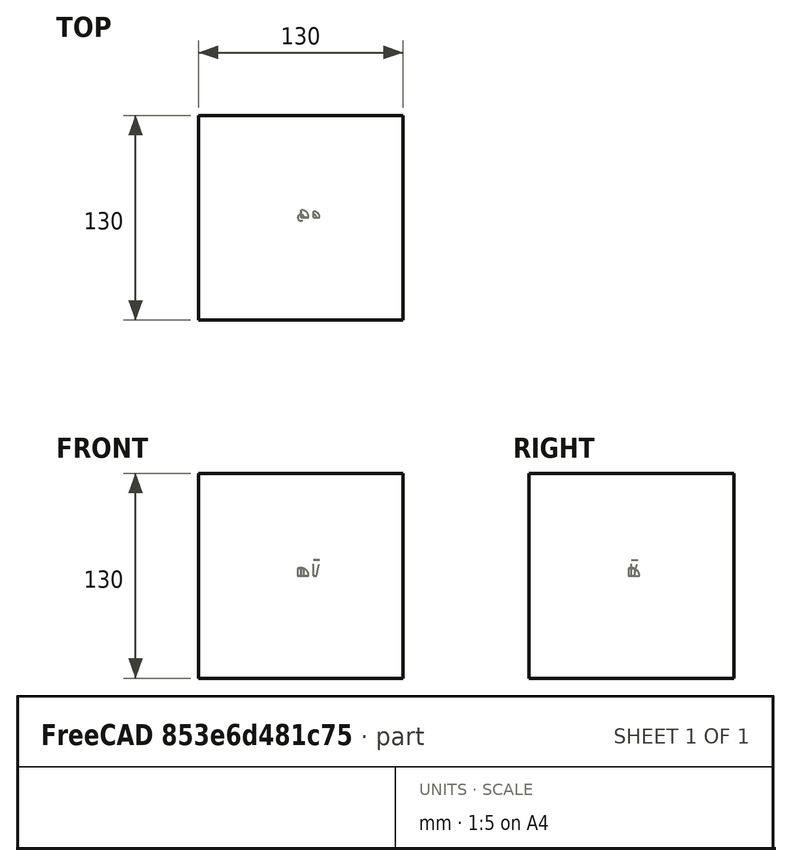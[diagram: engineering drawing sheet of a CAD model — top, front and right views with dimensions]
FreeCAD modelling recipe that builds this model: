
FCSTD DOCUMENT  (FreeCAD 1.0R39109 (Git))
Label: MultiCommon
License: All rights reserved
objects: App::DocumentObjectGroupPython×1252, App::Part×3, Spreadsheet::Sheet×2, Part::Box×2, Part::FeaturePython×1, Part::Cylinder×1, Part::Sphere×1, Part::Cone×1, Part::Common×1, Part::MultiCommon×1
note: 8 computed .brp shape members not serialized (recipe doc carries the construction recipe); baked Part::Feature solids carry a one-line shape summary decoded from their .brp

FEATURE [Spreadsheet::Sheet] defines
  cells = A1='constant; B1='HALFPI; C1(HALFPI)==pi / 2; A2='constant; B2='PI; C2(PI)==1 * pi; A3='constant; B3='TWOPI; C3(TWOPI)==2 * pi
FEATURE [Spreadsheet::Sheet] gdmlInfo
FEATURE [App::DocumentObjectGroupPython] Define  # scripted group (container) (typed FeaturePython)
  Group = -> [defines,gdmlInfo]
FEATURE [App::DocumentObjectGroupPython] HALFPI  # scripted group (container) (typed FeaturePython)
  name = HALFPI
  value = pi/2.
FEATURE [App::DocumentObjectGroupPython] PI  # scripted group (container) (typed FeaturePython)
  name = PI
  value = 1.*pi
FEATURE [App::DocumentObjectGroupPython] TWOPI  # scripted group (container) (typed FeaturePython)
  name = TWOPI
  value = 2.*pi
FEATURE [App::DocumentObjectGroupPython] Constants  # scripted group (container) (typed FeaturePython)
  Group = -> [HALFPI,PI,TWOPI]
FEATURE [App::DocumentObjectGroupPython] Quantities  # scripted group (container) (typed FeaturePython)
FEATURE [App::DocumentObjectGroupPython] Variables  # scripted group (container) (typed FeaturePython)
FEATURE [App::DocumentObjectGroupPython] Isotopes  # scripted group (container) (typed FeaturePython)
FEATURE [App::DocumentObjectGroupPython] Elements  # scripted group (container) (typed FeaturePython)
FEATURE [App::DocumentObjectGroupPython] Matrix  # scripted group (container) (typed FeaturePython)
FEATURE [App::DocumentObjectGroupPython] Surfaces  # scripted group (container) (typed FeaturePython)
FEATURE [App::DocumentObjectGroupPython] Opticals  # scripted group (container) (typed FeaturePython)
  Group = -> [Matrix,Surfaces]
FEATURE [App::DocumentObjectGroupPython] G4Isotopes  # scripted group (container) (typed FeaturePython)
FEATURE [App::DocumentObjectGroupPython] H_element  # scripted group (container) (typed FeaturePython)
  Z = 1
  atom_value = 1.008
  formula = H
  name = H_element
FEATURE [App::DocumentObjectGroupPython] He_element  # scripted group (container) (typed FeaturePython)
  Z = 2
  atom_value = 4.0026
  formula = He
  name = He_element
FEATURE [App::DocumentObjectGroupPython] Li_element  # scripted group (container) (typed FeaturePython)
  Z = 3
  atom_value = 6.94
  formula = Li
  name = Li_element
FEATURE [App::DocumentObjectGroupPython] Be_element  # scripted group (container) (typed FeaturePython)
  Z = 4
  atom_value = 9.01218
  formula = Be
  name = Be_element
FEATURE [App::DocumentObjectGroupPython] B_element  # scripted group (container) (typed FeaturePython)
  Z = 5
  atom_value = 10.81
  formula = B
  name = B_element
FEATURE [App::DocumentObjectGroupPython] C_element  # scripted group (container) (typed FeaturePython)
  Z = 6
  atom_value = 12.011
  formula = C
  name = C_element
FEATURE [App::DocumentObjectGroupPython] N_element  # scripted group (container) (typed FeaturePython)
  Z = 7
  atom_value = 14.007
  formula = N
  name = N_element
FEATURE [App::DocumentObjectGroupPython] O_element  # scripted group (container) (typed FeaturePython)
  Z = 8
  atom_value = 15.999
  formula = O
  name = O_element
FEATURE [App::DocumentObjectGroupPython] F_element  # scripted group (container) (typed FeaturePython)
  Z = 9
  atom_value = 18.9984
  formula = F
  name = F_element
FEATURE [App::DocumentObjectGroupPython] Ne_element  # scripted group (container) (typed FeaturePython)
  Z = 10
  atom_value = 20.1797
  formula = Ne
  name = Ne_element
FEATURE [App::DocumentObjectGroupPython] Na_element  # scripted group (container) (typed FeaturePython)
  Z = 11
  atom_value = 22.9898
  formula = Na
  name = Na_element
FEATURE [App::DocumentObjectGroupPython] Mg_element  # scripted group (container) (typed FeaturePython)
  Z = 12
  atom_value = 24.305
  formula = Mg
  name = Mg_element
FEATURE [App::DocumentObjectGroupPython] Al_element  # scripted group (container) (typed FeaturePython)
  Z = 13
  atom_value = 26.9815
  formula = Al
  name = Al_element
FEATURE [App::DocumentObjectGroupPython] Si_element  # scripted group (container) (typed FeaturePython)
  Z = 14
  atom_value = 28.085
  formula = Si
  name = Si_element
FEATURE [App::DocumentObjectGroupPython] P_element  # scripted group (container) (typed FeaturePython)
  Z = 15
  atom_value = 30.9738
  formula = P
  name = P_element
FEATURE [App::DocumentObjectGroupPython] S_element  # scripted group (container) (typed FeaturePython)
  Z = 16
  atom_value = 32.06
  formula = S
  name = S_element
FEATURE [App::DocumentObjectGroupPython] Cl_element  # scripted group (container) (typed FeaturePython)
  Z = 17
  atom_value = 35.45
  formula = Cl
  name = Cl_element
FEATURE [App::DocumentObjectGroupPython] Ar_element  # scripted group (container) (typed FeaturePython)
  Z = 18
  atom_value = 39.95
  formula = Ar
  name = Ar_element
FEATURE [App::DocumentObjectGroupPython] K_element  # scripted group (container) (typed FeaturePython)
  Z = 19
  atom_value = 39.0983
  formula = K
  name = K_element
FEATURE [App::DocumentObjectGroupPython] Ca_element  # scripted group (container) (typed FeaturePython)
  Z = 20
  atom_value = 40.078
  formula = Ca
  name = Ca_element
FEATURE [App::DocumentObjectGroupPython] Sc_element  # scripted group (container) (typed FeaturePython)
  Z = 21
  atom_value = 44.9559
  formula = Sc
  name = Sc_element
FEATURE [App::DocumentObjectGroupPython] Ti_element  # scripted group (container) (typed FeaturePython)
  Z = 22
  atom_value = 47.867
  formula = Ti
  name = Ti_element
FEATURE [App::DocumentObjectGroupPython] V_element  # scripted group (container) (typed FeaturePython)
  Z = 23
  atom_value = 50.9415
  formula = V
  name = V_element
FEATURE [App::DocumentObjectGroupPython] Cr_element  # scripted group (container) (typed FeaturePython)
  Z = 24
  atom_value = 51.9961
  formula = Cr
  name = Cr_element
FEATURE [App::DocumentObjectGroupPython] Mn_element  # scripted group (container) (typed FeaturePython)
  Z = 25
  atom_value = 54.938
  formula = Mn
  name = Mn_element
FEATURE [App::DocumentObjectGroupPython] Fe_element  # scripted group (container) (typed FeaturePython)
  Z = 26
  atom_value = 55.845
  formula = Fe
  name = Fe_element
FEATURE [App::DocumentObjectGroupPython] Co_element  # scripted group (container) (typed FeaturePython)
  Z = 27
  atom_value = 58.9332
  formula = Co
  name = Co_element
FEATURE [App::DocumentObjectGroupPython] Ni_element  # scripted group (container) (typed FeaturePython)
  Z = 28
  atom_value = 58.6934
  formula = Ni
  name = Ni_element
FEATURE [App::DocumentObjectGroupPython] Cu_element  # scripted group (container) (typed FeaturePython)
  Z = 29
  atom_value = 63.546
  formula = Cu
  name = Cu_element
FEATURE [App::DocumentObjectGroupPython] Zn_element  # scripted group (container) (typed FeaturePython)
  Z = 30
  atom_value = 65.38
  formula = Zn
  name = Zn_element
FEATURE [App::DocumentObjectGroupPython] Ga_element  # scripted group (container) (typed FeaturePython)
  Z = 31
  atom_value = 69.723
  formula = Ga
  name = Ga_element
FEATURE [App::DocumentObjectGroupPython] Ge_element  # scripted group (container) (typed FeaturePython)
  Z = 32
  atom_value = 72.63
  formula = Ge
  name = Ge_element
FEATURE [App::DocumentObjectGroupPython] As_element  # scripted group (container) (typed FeaturePython)
  Z = 33
  atom_value = 74.9216
  formula = As
  name = As_element
FEATURE [App::DocumentObjectGroupPython] Se_element  # scripted group (container) (typed FeaturePython)
  Z = 34
  atom_value = 78.971
  formula = Se
  name = Se_element
FEATURE [App::DocumentObjectGroupPython] Br_element  # scripted group (container) (typed FeaturePython)
  Z = 35
  atom_value = 79.904
  formula = Br
  name = Br_element
FEATURE [App::DocumentObjectGroupPython] Kr_element  # scripted group (container) (typed FeaturePython)
  Z = 36
  atom_value = 83.798
  formula = Kr
  name = Kr_element
FEATURE [App::DocumentObjectGroupPython] Rb_element  # scripted group (container) (typed FeaturePython)
  Z = 37
  atom_value = 85.4678
  formula = Rb
  name = Rb_element
FEATURE [App::DocumentObjectGroupPython] Sr_element  # scripted group (container) (typed FeaturePython)
  Z = 38
  atom_value = 87.62
  formula = Sr
  name = Sr_element
FEATURE [App::DocumentObjectGroupPython] Y_element  # scripted group (container) (typed FeaturePython)
  Z = 39
  atom_value = 88.9058
  formula = Y
  name = Y_element
FEATURE [App::DocumentObjectGroupPython] Zr_element  # scripted group (container) (typed FeaturePython)
  Z = 40
  atom_value = 91.224
  formula = Zr
  name = Zr_element
FEATURE [App::DocumentObjectGroupPython] Nb_element  # scripted group (container) (typed FeaturePython)
  Z = 41
  atom_value = 92.9064
  formula = Nb
  name = Nb_element
FEATURE [App::DocumentObjectGroupPython] Mo_element  # scripted group (container) (typed FeaturePython)
  Z = 42
  atom_value = 95.95
  formula = Mo
  name = Mo_element
FEATURE [App::DocumentObjectGroupPython] Tc_element  # scripted group (container) (typed FeaturePython)
  Z = 43
  atom_value = 97
  formula = Tc
  name = Tc_element
FEATURE [App::DocumentObjectGroupPython] Ru_element  # scripted group (container) (typed FeaturePython)
  Z = 44
  atom_value = 101.07
  formula = Ru
  name = Ru_element
FEATURE [App::DocumentObjectGroupPython] Rh_element  # scripted group (container) (typed FeaturePython)
  Z = 45
  atom_value = 102.905
  formula = Rh
  name = Rh_element
FEATURE [App::DocumentObjectGroupPython] Pd_element  # scripted group (container) (typed FeaturePython)
  Z = 46
  atom_value = 106.42
  formula = Pd
  name = Pd_element
FEATURE [App::DocumentObjectGroupPython] Ag_element  # scripted group (container) (typed FeaturePython)
  Z = 47
  atom_value = 107.868
  formula = Ag
  name = Ag_element
FEATURE [App::DocumentObjectGroupPython] Cd_element  # scripted group (container) (typed FeaturePython)
  Z = 48
  atom_value = 112.414
  formula = Cd
  name = Cd_element
FEATURE [App::DocumentObjectGroupPython] In_element  # scripted group (container) (typed FeaturePython)
  Z = 49
  atom_value = 114.818
  formula = In
  name = In_element
FEATURE [App::DocumentObjectGroupPython] Sn_element  # scripted group (container) (typed FeaturePython)
  Z = 50
  atom_value = 118.71
  formula = Sn
  name = Sn_element
FEATURE [App::DocumentObjectGroupPython] Sb_element  # scripted group (container) (typed FeaturePython)
  Z = 51
  atom_value = 121.76
  formula = Sb
  name = Sb_element
FEATURE [App::DocumentObjectGroupPython] Te_element  # scripted group (container) (typed FeaturePython)
  Z = 52
  atom_value = 127.6
  formula = Te
  name = Te_element
FEATURE [App::DocumentObjectGroupPython] I_element  # scripted group (container) (typed FeaturePython)
  Z = 53
  atom_value = 126.904
  formula = I
  name = I_element
FEATURE [App::DocumentObjectGroupPython] Xe_element  # scripted group (container) (typed FeaturePython)
  Z = 54
  atom_value = 131.293
  formula = Xe
  name = Xe_element
FEATURE [App::DocumentObjectGroupPython] Cs_element  # scripted group (container) (typed FeaturePython)
  Z = 55
  atom_value = 132.905
  formula = Cs
  name = Cs_element
FEATURE [App::DocumentObjectGroupPython] Ba_element  # scripted group (container) (typed FeaturePython)
  Z = 56
  atom_value = 137.327
  formula = Ba
  name = Ba_element
FEATURE [App::DocumentObjectGroupPython] La_element  # scripted group (container) (typed FeaturePython)
  Z = 57
  atom_value = 138.905
  formula = La
  name = La_element
FEATURE [App::DocumentObjectGroupPython] Ce_element  # scripted group (container) (typed FeaturePython)
  Z = 58
  atom_value = 140.116
  formula = Ce
  name = Ce_element
FEATURE [App::DocumentObjectGroupPython] Pr_element  # scripted group (container) (typed FeaturePython)
  Z = 59
  atom_value = 140.908
  formula = Pr
  name = Pr_element
FEATURE [App::DocumentObjectGroupPython] Nd_element  # scripted group (container) (typed FeaturePython)
  Z = 60
  atom_value = 144.242
  formula = Nd
  name = Nd_element
FEATURE [App::DocumentObjectGroupPython] Pm_element  # scripted group (container) (typed FeaturePython)
  Z = 61
  atom_value = 145
  formula = Pm
  name = Pm_element
FEATURE [App::DocumentObjectGroupPython] Sm_element  # scripted group (container) (typed FeaturePython)
  Z = 62
  atom_value = 150.36
  formula = Sm
  name = Sm_element
FEATURE [App::DocumentObjectGroupPython] Eu_element  # scripted group (container) (typed FeaturePython)
  Z = 63
  atom_value = 151.964
  formula = Eu
  name = Eu_element
FEATURE [App::DocumentObjectGroupPython] Gd_element  # scripted group (container) (typed FeaturePython)
  Z = 64
  atom_value = 157.25
  formula = Gd
  name = Gd_element
FEATURE [App::DocumentObjectGroupPython] Tb_element  # scripted group (container) (typed FeaturePython)
  Z = 65
  atom_value = 158.925
  formula = Tb
  name = Tb_element
FEATURE [App::DocumentObjectGroupPython] Dy_element  # scripted group (container) (typed FeaturePython)
  Z = 66
  atom_value = 162.5
  formula = Dy
  name = Dy_element
FEATURE [App::DocumentObjectGroupPython] Ho_element  # scripted group (container) (typed FeaturePython)
  Z = 67
  atom_value = 164.93
  formula = Ho
  name = Ho_element
FEATURE [App::DocumentObjectGroupPython] Er_element  # scripted group (container) (typed FeaturePython)
  Z = 68
  atom_value = 167.259
  formula = Er
  name = Er_element
FEATURE [App::DocumentObjectGroupPython] Tm_element  # scripted group (container) (typed FeaturePython)
  Z = 69
  atom_value = 168.934
  formula = Tm
  name = Tm_element
FEATURE [App::DocumentObjectGroupPython] Yb_element  # scripted group (container) (typed FeaturePython)
  Z = 70
  atom_value = 173.045
  formula = Yb
  name = Yb_element
FEATURE [App::DocumentObjectGroupPython] Lu_element  # scripted group (container) (typed FeaturePython)
  Z = 71
  atom_value = 174.967
  formula = Lu
  name = Lu_element
FEATURE [App::DocumentObjectGroupPython] Hf_element  # scripted group (container) (typed FeaturePython)
  Z = 72
  atom_value = 178.49
  formula = Hf
  name = Hf_element
FEATURE [App::DocumentObjectGroupPython] Ta_element  # scripted group (container) (typed FeaturePython)
  Z = 73
  atom_value = 180.948
  formula = Ta
  name = Ta_element
FEATURE [App::DocumentObjectGroupPython] W_element  # scripted group (container) (typed FeaturePython)
  Z = 74
  atom_value = 183.84
  formula = W
  name = W_element
FEATURE [App::DocumentObjectGroupPython] Re_element  # scripted group (container) (typed FeaturePython)
  Z = 75
  atom_value = 186.207
  formula = Re
  name = Re_element
FEATURE [App::DocumentObjectGroupPython] Os_element  # scripted group (container) (typed FeaturePython)
  Z = 76
  atom_value = 190.23
  formula = Os
  name = Os_element
FEATURE [App::DocumentObjectGroupPython] Ir_element  # scripted group (container) (typed FeaturePython)
  Z = 77
  atom_value = 192.217
  formula = Ir
  name = Ir_element
FEATURE [App::DocumentObjectGroupPython] Pt_element  # scripted group (container) (typed FeaturePython)
  Z = 78
  atom_value = 195.084
  formula = Pt
  name = Pt_element
FEATURE [App::DocumentObjectGroupPython] Au_element  # scripted group (container) (typed FeaturePython)
  Z = 79
  atom_value = 196.967
  formula = Au
  name = Au_element
FEATURE [App::DocumentObjectGroupPython] Hg_element  # scripted group (container) (typed FeaturePython)
  Z = 80
  atom_value = 200.592
  formula = Hg
  name = Hg_element
FEATURE [App::DocumentObjectGroupPython] Tl_element  # scripted group (container) (typed FeaturePython)
  Z = 81
  atom_value = 204.38
  formula = Tl
  name = Tl_element
FEATURE [App::DocumentObjectGroupPython] Pb_element  # scripted group (container) (typed FeaturePython)
  Z = 82
  atom_value = 207.2
  formula = Pb
  name = Pb_element
FEATURE [App::DocumentObjectGroupPython] Bi_element  # scripted group (container) (typed FeaturePython)
  Z = 83
  atom_value = 208.98
  formula = Bi
  name = Bi_element
FEATURE [App::DocumentObjectGroupPython] Po_element  # scripted group (container) (typed FeaturePython)
  Z = 84
  atom_value = 209
  formula = Po
  name = Po_element
FEATURE [App::DocumentObjectGroupPython] At_element  # scripted group (container) (typed FeaturePython)
  Z = 85
  atom_value = 210
  formula = At
  name = At_element
FEATURE [App::DocumentObjectGroupPython] Rn_element  # scripted group (container) (typed FeaturePython)
  Z = 86
  atom_value = 222
  formula = Rn
  name = Rn_element
FEATURE [App::DocumentObjectGroupPython] Fr_element  # scripted group (container) (typed FeaturePython)
  Z = 87
  atom_value = 223
  formula = Fr
  name = Fr_element
FEATURE [App::DocumentObjectGroupPython] Ra_element  # scripted group (container) (typed FeaturePython)
  Z = 88
  atom_value = 226
  formula = Ra
  name = Ra_element
FEATURE [App::DocumentObjectGroupPython] Ac_element  # scripted group (container) (typed FeaturePython)
  Z = 89
  atom_value = 227
  formula = Ac
  name = Ac_element
FEATURE [App::DocumentObjectGroupPython] Th_element  # scripted group (container) (typed FeaturePython)
  Z = 90
  atom_value = 232.038
  formula = Th
  name = Th_element
FEATURE [App::DocumentObjectGroupPython] Pa_element  # scripted group (container) (typed FeaturePython)
  Z = 91
  atom_value = 231.036
  formula = Pa
  name = Pa_element
FEATURE [App::DocumentObjectGroupPython] U_element  # scripted group (container) (typed FeaturePython)
  Z = 92
  atom_value = 238.029
  formula = U
  name = U_element
FEATURE [App::DocumentObjectGroupPython] Np_element  # scripted group (container) (typed FeaturePython)
  Z = 93
  atom_value = 237
  formula = Np
  name = Np_element
FEATURE [App::DocumentObjectGroupPython] Pu_element  # scripted group (container) (typed FeaturePython)
  Z = 94
  atom_value = 244
  formula = Pu
  name = Pu_element
FEATURE [App::DocumentObjectGroupPython] Am_element  # scripted group (container) (typed FeaturePython)
  Z = 95
  atom_value = 243
  formula = Am
  name = Am_element
FEATURE [App::DocumentObjectGroupPython] Cm_element  # scripted group (container) (typed FeaturePython)
  Z = 96
  atom_value = 247
  formula = Cm
  name = Cm_element
FEATURE [App::DocumentObjectGroupPython] Bk_element  # scripted group (container) (typed FeaturePython)
  Z = 97
  atom_value = 247
  formula = Bk
  name = Bk_element
FEATURE [App::DocumentObjectGroupPython] Cf_element  # scripted group (container) (typed FeaturePython)
  Z = 98
  atom_value = 251
  formula = Cf
  name = Cf_element
FEATURE [App::DocumentObjectGroupPython] G4Elements  # scripted group (container) (typed FeaturePython)
  Group = -> [H_element,He_element,Li_element,Be_element,B_element,C_element,N_element,O_element,F_element,Ne_element,Na_element,Mg_element,Al_element,Si_element,P_element,S_element,Cl_element,Ar_element,K_element,Ca_element,Sc_element,Ti_element,V_element,Cr_element,Mn_element,Fe_element,Co_element,Ni_element,Cu_element,Zn_element,Ga_element,Ge_element,As_element,Se_element,Br_element,Kr_element,Rb_element,+61 more]
FEATURE [App::DocumentObjectGroupPython] H_element001  label="H_element : 0.101"  # scripted group (container) (typed FeaturePython)
  n = 0.101327
FEATURE [App::DocumentObjectGroupPython] C_element001  label="C_element : 0.775"  # scripted group (container) (typed FeaturePython)
  n = 0.7755
FEATURE [App::DocumentObjectGroupPython] N_element001  label="N_element : 0.035"  # scripted group (container) (typed FeaturePython)
  n = 0.035057
FEATURE [App::DocumentObjectGroupPython] O_element001  label="O_element : 0.052"  # scripted group (container) (typed FeaturePython)
  n = 0.0523159
FEATURE [App::DocumentObjectGroupPython] F_element001  label="F_element : 0.017"  # scripted group (container) (typed FeaturePython)
  n = 0.017422
FEATURE [App::DocumentObjectGroupPython] Ca_element001  label="Ca_element : 0.018"  # scripted group (container) (typed FeaturePython)
  n = 0.018378
FEATURE [App::DocumentObjectGroupPython] G4_A_150_TISSUE  label="G4_A-150_TISSUE"  # scripted group (container) (typed FeaturePython)
  Dunit = g/cm3
  Dvalue = 1.127
  Group = -> [H_element001,C_element001,N_element001,O_element001,F_element001,Ca_element001]
  conduct = 2
  density = 1
  expand = 3
  formula = G4_A-150_TISSUE
  name = G4_A-150_TISSUE
  specific = 4
FEATURE [App::DocumentObjectGroupPython] C_element002  label="C_element : 3"  # scripted group (container) (typed FeaturePython)
  n = 3
  ref = C_element
FEATURE [App::DocumentObjectGroupPython] H_element002  label="H_element : 6"  # scripted group (container) (typed FeaturePython)
  n = 6
  ref = H_element
FEATURE [App::DocumentObjectGroupPython] O_element002  label="O_element : 1"  # scripted group (container) (typed FeaturePython)
  n = 1
  ref = O_element
FEATURE [App::DocumentObjectGroupPython] G4_ACETONE  # scripted group (container) (typed FeaturePython)
  Dunit = g/cm3
  Dvalue = 0.7899
  Group = -> [C_element002,H_element002,O_element002]
  conduct = 2
  density = 1
  expand = 3
  formula = G4_ACETONE
  name = G4_ACETONE
  specific = 4
FEATURE [App::DocumentObjectGroupPython] C_element003  label="C_element : 2"  # scripted group (container) (typed FeaturePython)
  n = 2
  ref = C_element
FEATURE [App::DocumentObjectGroupPython] H_element003  label="H_element : 2"  # scripted group (container) (typed FeaturePython)
  n = 2
  ref = H_element
FEATURE [App::DocumentObjectGroupPython] G4_ACETYLENE  # scripted group (container) (typed FeaturePython)
  Dunit = g/cm3
  Dvalue = 0.0010967
  Group = -> [C_element003,H_element003]
  conduct = 2
  density = 1
  expand = 3
  formula = G4_ACETYLENE
  name = G4_ACETYLENE
  specific = 4
FEATURE [App::DocumentObjectGroupPython] C_element004  label="C_element : 5"  # scripted group (container) (typed FeaturePython)
  n = 5
  ref = C_element
FEATURE [App::DocumentObjectGroupPython] H_element004  label="H_element : 5"  # scripted group (container) (typed FeaturePython)
  n = 5
  ref = H_element
FEATURE [App::DocumentObjectGroupPython] N_element002  label="N_element : 5"  # scripted group (container) (typed FeaturePython)
  n = 5
  ref = N_element
FEATURE [App::DocumentObjectGroupPython] G4_ADENINE  # scripted group (container) (typed FeaturePython)
  Dunit = g/cm3
  Dvalue = 1.6
  Group = -> [C_element004,H_element004,N_element002]
  conduct = 2
  density = 1
  expand = 3
  formula = G4_ADENINE
  name = G4_ADENINE
  specific = 4
FEATURE [App::DocumentObjectGroupPython] H_element005  label="H_element : 0.114"  # scripted group (container) (typed FeaturePython)
  n = 0.114
FEATURE [App::DocumentObjectGroupPython] C_element005  label="C_element : 0.598"  # scripted group (container) (typed FeaturePython)
  n = 0.598
FEATURE [App::DocumentObjectGroupPython] N_element003  label="N_element : 0.007"  # scripted group (container) (typed FeaturePython)
  n = 0.007
FEATURE [App::DocumentObjectGroupPython] O_element003  label="O_element : 0.278"  # scripted group (container) (typed FeaturePython)
  n = 0.278
FEATURE [App::DocumentObjectGroupPython] Na_element001  label="Na_element : 0.001"  # scripted group (container) (typed FeaturePython)
  n = 0.001
FEATURE [App::DocumentObjectGroupPython] S_element001  label="S_element : 0.001"  # scripted group (container) (typed FeaturePython)
  n = 0.001
FEATURE [App::DocumentObjectGroupPython] Cl_element001  label="Cl_element : 0.001"  # scripted group (container) (typed FeaturePython)
  n = 0.001
FEATURE [App::DocumentObjectGroupPython] G4_ADIPOSE_TISSUE_ICRP  # scripted group (container) (typed FeaturePython)
  Dunit = g/cm3
  Dvalue = 0.95
  Group = -> [H_element005,C_element005,N_element003,O_element003,Na_element001,S_element001,Cl_element001]
  conduct = 2
  density = 1
  expand = 3
  formula = G4_ADIPOSE_TISSUE_ICRP
  name = G4_ADIPOSE_TISSUE_ICRP
  specific = 4
FEATURE [App::DocumentObjectGroupPython] C_element006  label="C_element : 0.000"  # scripted group (container) (typed FeaturePython)
  n = 0.000124
FEATURE [App::DocumentObjectGroupPython] N_element004  label="N_element : 0.755"  # scripted group (container) (typed FeaturePython)
  n = 0.755268
FEATURE [App::DocumentObjectGroupPython] O_element004  label="O_element : 0.232"  # scripted group (container) (typed FeaturePython)
  n = 0.231781
FEATURE [App::DocumentObjectGroupPython] Ar_element001  label="Ar_element : 0.013"  # scripted group (container) (typed FeaturePython)
  n = 0.012827
FEATURE [App::DocumentObjectGroupPython] G4_AIR  # scripted group (container) (typed FeaturePython)
  Dunit = g/cm3
  Dvalue = 0.00120479
  Group = -> [C_element006,N_element004,O_element004,Ar_element001]
  conduct = 2
  density = 1
  expand = 3
  formula = G4_AIR
  name = G4_AIR
  specific = 4
FEATURE [App::DocumentObjectGroupPython] C_element007  label="C_element : 006"  # scripted group (container) (typed FeaturePython)
  n = 3
  ref = C_element
FEATURE [App::DocumentObjectGroupPython] H_element006  label="H_element : 7"  # scripted group (container) (typed FeaturePython)
  n = 7
  ref = H_element
FEATURE [App::DocumentObjectGroupPython] N_element005  label="N_element : 1"  # scripted group (container) (typed FeaturePython)
  n = 1
  ref = N_element
FEATURE [App::DocumentObjectGroupPython] O_element005  label="O_element : 2"  # scripted group (container) (typed FeaturePython)
  n = 2
  ref = O_element
FEATURE [App::DocumentObjectGroupPython] G4_ALANINE  # scripted group (container) (typed FeaturePython)
  Dunit = g/cm3
  Dvalue = 1.42
  Group = -> [C_element007,H_element006,N_element005,O_element005]
  conduct = 2
  density = 1
  expand = 3
  formula = G4_ALANINE
  name = G4_ALANINE
  specific = 4
FEATURE [App::DocumentObjectGroupPython] Al_element001  label="Al_element : 2"  # scripted group (container) (typed FeaturePython)
  n = 2
  ref = Al_element
FEATURE [App::DocumentObjectGroupPython] O_element006  label="O_element : 3"  # scripted group (container) (typed FeaturePython)
  n = 3
  ref = O_element
FEATURE [App::DocumentObjectGroupPython] G4_ALUMINUM_OXIDE  # scripted group (container) (typed FeaturePython)
  Dunit = g/cm3
  Dvalue = 3.97
  Group = -> [Al_element001,O_element006]
  conduct = 2
  density = 1
  expand = 3
  formula = G4_ALUMINUM_OXIDE
  name = G4_ALUMINUM_OXIDE
  specific = 4
FEATURE [App::DocumentObjectGroupPython] H_element007  label="H_element : 0.106"  # scripted group (container) (typed FeaturePython)
  n = 0.10593
FEATURE [App::DocumentObjectGroupPython] C_element008  label="C_element : 0.789"  # scripted group (container) (typed FeaturePython)
  n = 0.788974
FEATURE [App::DocumentObjectGroupPython] O_element007  label="O_element : 0.105"  # scripted group (container) (typed FeaturePython)
  n = 0.105096
FEATURE [App::DocumentObjectGroupPython] G4_AMBER  # scripted group (container) (typed FeaturePython)
  Dunit = g/cm3
  Dvalue = 1.1
  Group = -> [H_element007,C_element008,O_element007]
  conduct = 2
  density = 1
  expand = 3
  formula = G4_AMBER
  name = G4_AMBER
  specific = 4
FEATURE [App::DocumentObjectGroupPython] N_element006  label="N_element : 006"  # scripted group (container) (typed FeaturePython)
  n = 1
  ref = N_element
FEATURE [App::DocumentObjectGroupPython] H_element008  label="H_element : 3"  # scripted group (container) (typed FeaturePython)
  n = 3
  ref = H_element
FEATURE [App::DocumentObjectGroupPython] G4_AMMONIA  # scripted group (container) (typed FeaturePython)
  Dunit = g/cm3
  Dvalue = 0.000826019
  Group = -> [N_element006,H_element008]
  conduct = 2
  density = 1
  expand = 3
  formula = G4_AMMONIA
  name = G4_AMMONIA
  specific = 4
FEATURE [App::DocumentObjectGroupPython] C_element009  label="C_element : 6"  # scripted group (container) (typed FeaturePython)
  n = 6
  ref = C_element
FEATURE [App::DocumentObjectGroupPython] H_element009  label="H_element : 008"  # scripted group (container) (typed FeaturePython)
  n = 7
  ref = H_element
FEATURE [App::DocumentObjectGroupPython] N_element007  label="N_element : 007"  # scripted group (container) (typed FeaturePython)
  n = 1
  ref = N_element
FEATURE [App::DocumentObjectGroupPython] G4_ANILINE  # scripted group (container) (typed FeaturePython)
  Dunit = g/cm3
  Dvalue = 1.0235
  Group = -> [C_element009,H_element009,N_element007]
  conduct = 2
  density = 1
  expand = 3
  formula = G4_ANILINE
  name = G4_ANILINE
  specific = 4
FEATURE [App::DocumentObjectGroupPython] C_element010  label="C_element : 14"  # scripted group (container) (typed FeaturePython)
  n = 14
  ref = C_element
FEATURE [App::DocumentObjectGroupPython] H_element010  label="H_element : 10"  # scripted group (container) (typed FeaturePython)
  n = 10
  ref = H_element
FEATURE [App::DocumentObjectGroupPython] G4_ANTHRACENE  # scripted group (container) (typed FeaturePython)
  Dunit = g/cm3
  Dvalue = 1.283
  Group = -> [C_element010,H_element010]
  conduct = 2
  density = 1
  expand = 3
  formula = G4_ANTHRACENE
  name = G4_ANTHRACENE
  specific = 4
FEATURE [App::DocumentObjectGroupPython] H_element011  label="H_element : 0.065"  # scripted group (container) (typed FeaturePython)
  n = 0.0654709
FEATURE [App::DocumentObjectGroupPython] C_element011  label="C_element : 0.537"  # scripted group (container) (typed FeaturePython)
  n = 0.536944
FEATURE [App::DocumentObjectGroupPython] N_element008  label="N_element : 0.021"  # scripted group (container) (typed FeaturePython)
  n = 0.0215
FEATURE [App::DocumentObjectGroupPython] O_element008  label="O_element : 0.032"  # scripted group (container) (typed FeaturePython)
  n = 0.032085
FEATURE [App::DocumentObjectGroupPython] F_element002  label="F_element : 0.167"  # scripted group (container) (typed FeaturePython)
  n = 0.167411
FEATURE [App::DocumentObjectGroupPython] Ca_element002  label="Ca_element : 0.177"  # scripted group (container) (typed FeaturePython)
  n = 0.176589
FEATURE [App::DocumentObjectGroupPython] G4_B_100_BONE  label="G4_B-100_BONE"  # scripted group (container) (typed FeaturePython)
  Dunit = g/cm3
  Dvalue = 1.45
  Group = -> [H_element011,C_element011,N_element008,O_element008,F_element002,Ca_element002]
  conduct = 2
  density = 1
  expand = 3
  formula = G4_B-100_BONE
  name = G4_B-100_BONE
  specific = 4
FEATURE [App::DocumentObjectGroupPython] H_element012  label="H_element : 0.057"  # scripted group (container) (typed FeaturePython)
  n = 0.057441
FEATURE [App::DocumentObjectGroupPython] C_element012  label="C_element : 0.790"  # scripted group (container) (typed FeaturePython)
  n = 0.774591
FEATURE [App::DocumentObjectGroupPython] O_element009  label="O_element : 0.168"  # scripted group (container) (typed FeaturePython)
  n = 0.167968
FEATURE [App::DocumentObjectGroupPython] G4_BAKELITE  # scripted group (container) (typed FeaturePython)
  Dunit = g/cm3
  Dvalue = 1.25
  Group = -> [H_element012,C_element012,O_element009]
  conduct = 2
  density = 1
  expand = 3
  formula = G4_BAKELITE
  name = G4_BAKELITE
  specific = 4
FEATURE [App::DocumentObjectGroupPython] Ba_element001  label="Ba_element : 1"  # scripted group (container) (typed FeaturePython)
  n = 1
  ref = Ba_element
FEATURE [App::DocumentObjectGroupPython] F_element003  label="F_element : 2"  # scripted group (container) (typed FeaturePython)
  n = 2
  ref = F_element
FEATURE [App::DocumentObjectGroupPython] G4_BARIUM_FLUORIDE  # scripted group (container) (typed FeaturePython)
  Dunit = g/cm3
  Dvalue = 4.89
  Group = -> [Ba_element001,F_element003]
  conduct = 2
  density = 1
  expand = 3
  formula = G4_BARIUM_FLUORIDE
  name = G4_BARIUM_FLUORIDE
  specific = 4
FEATURE [App::DocumentObjectGroupPython] Ba_element002  label="Ba_element : 002"  # scripted group (container) (typed FeaturePython)
  n = 1
  ref = Ba_element
FEATURE [App::DocumentObjectGroupPython] S_element002  label="S_element : 1"  # scripted group (container) (typed FeaturePython)
  n = 1
  ref = S_element
FEATURE [App::DocumentObjectGroupPython] O_element010  label="O_element : 4"  # scripted group (container) (typed FeaturePython)
  n = 4
  ref = O_element
FEATURE [App::DocumentObjectGroupPython] G4_BARIUM_SULFATE  # scripted group (container) (typed FeaturePython)
  Dunit = g/cm3
  Dvalue = 4.5
  Group = -> [Ba_element002,S_element002,O_element010]
  conduct = 2
  density = 1
  expand = 3
  formula = G4_BARIUM_SULFATE
  name = G4_BARIUM_SULFATE
  specific = 4
FEATURE [App::DocumentObjectGroupPython] C_element013  label="C_element : 007"  # scripted group (container) (typed FeaturePython)
  n = 6
  ref = C_element
FEATURE [App::DocumentObjectGroupPython] H_element013  label="H_element : 009"  # scripted group (container) (typed FeaturePython)
  n = 6
  ref = H_element
FEATURE [App::DocumentObjectGroupPython] G4_BENZENE  # scripted group (container) (typed FeaturePython)
  Dunit = g/cm3
  Dvalue = 0.87865
  Group = -> [C_element013,H_element013]
  conduct = 2
  density = 1
  expand = 3
  formula = G4_BENZENE
  name = G4_BENZENE
  specific = 4
FEATURE [App::DocumentObjectGroupPython] Be_element001  label="Be_element : 1"  # scripted group (container) (typed FeaturePython)
  n = 1
  ref = Be_element
FEATURE [App::DocumentObjectGroupPython] O_element011  label="O_element : 005"  # scripted group (container) (typed FeaturePython)
  n = 1
  ref = O_element
FEATURE [App::DocumentObjectGroupPython] G4_BERYLLIUM_OXIDE  # scripted group (container) (typed FeaturePython)
  Dunit = g/cm3
  Dvalue = 3.01
  Group = -> [Be_element001,O_element011]
  conduct = 2
  density = 1
  expand = 3
  formula = G4_BERYLLIUM_OXIDE
  name = G4_BERYLLIUM_OXIDE
  specific = 4
FEATURE [App::DocumentObjectGroupPython] Bi_element001  label="Bi_element : 4"  # scripted group (container) (typed FeaturePython)
  n = 4
  ref = Bi_element
FEATURE [App::DocumentObjectGroupPython] Ge_element001  label="Ge_element : 3"  # scripted group (container) (typed FeaturePython)
  n = 3
  ref = Ge_element
FEATURE [App::DocumentObjectGroupPython] O_element012  label="O_element : 12"  # scripted group (container) (typed FeaturePython)
  n = 12
  ref = O_element
FEATURE [App::DocumentObjectGroupPython] G4_BGO  # scripted group (container) (typed FeaturePython)
  Dunit = g/cm3
  Dvalue = 7.13
  Group = -> [Bi_element001,Ge_element001,O_element012]
  conduct = 2
  density = 1
  expand = 3
  formula = G4_BGO
  name = G4_BGO
  specific = 4
FEATURE [App::DocumentObjectGroupPython] H_element014  label="H_element : 0.102"  # scripted group (container) (typed FeaturePython)
  n = 0.102
FEATURE [App::DocumentObjectGroupPython] C_element014  label="C_element : 0.110"  # scripted group (container) (typed FeaturePython)
  n = 0.11
FEATURE [App::DocumentObjectGroupPython] N_element009  label="N_element : 0.033"  # scripted group (container) (typed FeaturePython)
  n = 0.033
FEATURE [App::DocumentObjectGroupPython] O_element013  label="O_element : 0.745"  # scripted group (container) (typed FeaturePython)
  n = 0.745
FEATURE [App::DocumentObjectGroupPython] Na_element002  label="Na_element : 0.002"  # scripted group (container) (typed FeaturePython)
  n = 0.001
FEATURE [App::DocumentObjectGroupPython] P_element001  label="P_element : 0.001"  # scripted group (container) (typed FeaturePython)
  n = 0.001
FEATURE [App::DocumentObjectGroupPython] S_element003  label="S_element : 0.002"  # scripted group (container) (typed FeaturePython)
  n = 0.002
FEATURE [App::DocumentObjectGroupPython] Cl_element002  label="Cl_element : 0.003"  # scripted group (container) (typed FeaturePython)
  n = 0.003
FEATURE [App::DocumentObjectGroupPython] K_element001  label="K_element : 0.002"  # scripted group (container) (typed FeaturePython)
  n = 0.002
FEATURE [App::DocumentObjectGroupPython] Fe_element001  label="Fe_element : 0.001"  # scripted group (container) (typed FeaturePython)
  n = 0.001
FEATURE [App::DocumentObjectGroupPython] G4_BLOOD_ICRP  # scripted group (container) (typed FeaturePython)
  Dunit = g/cm3
  Dvalue = 1.06
  Group = -> [H_element014,C_element014,N_element009,O_element013,Na_element002,P_element001,S_element003,Cl_element002,K_element001,Fe_element001]
  conduct = 2
  density = 1
  expand = 3
  formula = G4_BLOOD_ICRP
  name = G4_BLOOD_ICRP
  specific = 4
FEATURE [App::DocumentObjectGroupPython] H_element015  label="H_element : 0.064"  # scripted group (container) (typed FeaturePython)
  n = 0.064
FEATURE [App::DocumentObjectGroupPython] C_element015  label="C_element : 0.278"  # scripted group (container) (typed FeaturePython)
  n = 0.278
FEATURE [App::DocumentObjectGroupPython] N_element010  label="N_element : 0.027"  # scripted group (container) (typed FeaturePython)
  n = 0.027
FEATURE [App::DocumentObjectGroupPython] O_element014  label="O_element : 0.410"  # scripted group (container) (typed FeaturePython)
  n = 0.41
FEATURE [App::DocumentObjectGroupPython] Mg_element001  label="Mg_element : 0.002"  # scripted group (container) (typed FeaturePython)
  n = 0.002
FEATURE [App::DocumentObjectGroupPython] P_element002  label="P_element : 0.070"  # scripted group (container) (typed FeaturePython)
  n = 0.07
FEATURE [App::DocumentObjectGroupPython] S_element004  label="S_element : 0.003"  # scripted group (container) (typed FeaturePython)
  n = 0.002
FEATURE [App::DocumentObjectGroupPython] Ca_element003  label="Ca_element : 0.147"  # scripted group (container) (typed FeaturePython)
  n = 0.147
FEATURE [App::DocumentObjectGroupPython] G4_BONE_COMPACT_ICRU  # scripted group (container) (typed FeaturePython)
  Dunit = g/cm3
  Dvalue = 1.85
  Group = -> [H_element015,C_element015,N_element010,O_element014,Mg_element001,P_element002,S_element004,Ca_element003]
  conduct = 2
  density = 1
  expand = 3
  formula = G4_BONE_COMPACT_ICRU
  name = G4_BONE_COMPACT_ICRU
  specific = 4
FEATURE [App::DocumentObjectGroupPython] H_element016  label="H_element : 0.034"  # scripted group (container) (typed FeaturePython)
  n = 0.034
FEATURE [App::DocumentObjectGroupPython] C_element016  label="C_element : 0.155"  # scripted group (container) (typed FeaturePython)
  n = 0.155
FEATURE [App::DocumentObjectGroupPython] N_element011  label="N_element : 0.042"  # scripted group (container) (typed FeaturePython)
  n = 0.042
FEATURE [App::DocumentObjectGroupPython] O_element015  label="O_element : 0.435"  # scripted group (container) (typed FeaturePython)
  n = 0.435
FEATURE [App::DocumentObjectGroupPython] Na_element003  label="Na_element : 0.003"  # scripted group (container) (typed FeaturePython)
  n = 0.001
FEATURE [App::DocumentObjectGroupPython] Mg_element002  label="Mg_element : 0.003"  # scripted group (container) (typed FeaturePython)
  n = 0.002
FEATURE [App::DocumentObjectGroupPython] P_element003  label="P_element : 0.103"  # scripted group (container) (typed FeaturePython)
  n = 0.103
FEATURE [App::DocumentObjectGroupPython] S_element005  label="S_element : 0.004"  # scripted group (container) (typed FeaturePython)
  n = 0.003
FEATURE [App::DocumentObjectGroupPython] Ca_element004  label="Ca_element : 0.225"  # scripted group (container) (typed FeaturePython)
  n = 0.225
FEATURE [App::DocumentObjectGroupPython] G4_BONE_CORTICAL_ICRP  # scripted group (container) (typed FeaturePython)
  Dunit = g/cm3
  Dvalue = 1.92
  Group = -> [H_element016,C_element016,N_element011,O_element015,Na_element003,Mg_element002,P_element003,S_element005,Ca_element004]
  conduct = 2
  density = 1
  expand = 3
  formula = G4_BONE_CORTICAL_ICRP
  name = G4_BONE_CORTICAL_ICRP
  specific = 4
FEATURE [App::DocumentObjectGroupPython] B_element001  label="B_element : 4"  # scripted group (container) (typed FeaturePython)
  n = 4
  ref = B_element
FEATURE [App::DocumentObjectGroupPython] C_element017  label="C_element : 1"  # scripted group (container) (typed FeaturePython)
  n = 1
  ref = C_element
FEATURE [App::DocumentObjectGroupPython] G4_BORON_CARBIDE  # scripted group (container) (typed FeaturePython)
  Dunit = g/cm3
  Dvalue = 2.52
  Group = -> [B_element001,C_element017]
  conduct = 2
  density = 1
  expand = 3
  formula = G4_BORON_CARBIDE
  name = G4_BORON_CARBIDE
  specific = 4
FEATURE [App::DocumentObjectGroupPython] B_element002  label="B_element : 2"  # scripted group (container) (typed FeaturePython)
  n = 2
  ref = B_element
FEATURE [App::DocumentObjectGroupPython] O_element016  label="O_element : 006"  # scripted group (container) (typed FeaturePython)
  n = 3
  ref = O_element
FEATURE [App::DocumentObjectGroupPython] G4_BORON_OXIDE  # scripted group (container) (typed FeaturePython)
  Dunit = g/cm3
  Dvalue = 1.812
  Group = -> [B_element002,O_element016]
  conduct = 2
  density = 1
  expand = 3
  formula = G4_BORON_OXIDE
  name = G4_BORON_OXIDE
  specific = 4
FEATURE [App::DocumentObjectGroupPython] H_element017  label="H_element : 0.107"  # scripted group (container) (typed FeaturePython)
  n = 0.107
FEATURE [App::DocumentObjectGroupPython] C_element018  label="C_element : 0.145"  # scripted group (container) (typed FeaturePython)
  n = 0.145
FEATURE [App::DocumentObjectGroupPython] N_element012  label="N_element : 0.022"  # scripted group (container) (typed FeaturePython)
  n = 0.022
FEATURE [App::DocumentObjectGroupPython] O_element017  label="O_element : 0.712"  # scripted group (container) (typed FeaturePython)
  n = 0.712
FEATURE [App::DocumentObjectGroupPython] Na_element004  label="Na_element : 0.004"  # scripted group (container) (typed FeaturePython)
  n = 0.002
FEATURE [App::DocumentObjectGroupPython] P_element004  label="P_element : 0.004"  # scripted group (container) (typed FeaturePython)
  n = 0.004
FEATURE [App::DocumentObjectGroupPython] S_element006  label="S_element : 0.005"  # scripted group (container) (typed FeaturePython)
  n = 0.002
FEATURE [App::DocumentObjectGroupPython] Cl_element003  label="Cl_element : 0.004"  # scripted group (container) (typed FeaturePython)
  n = 0.003
FEATURE [App::DocumentObjectGroupPython] K_element002  label="K_element : 0.003"  # scripted group (container) (typed FeaturePython)
  n = 0.003
FEATURE [App::DocumentObjectGroupPython] G4_BRAIN_ICRP  # scripted group (container) (typed FeaturePython)
  Dunit = g/cm3
  Dvalue = 1.04
  Group = -> [H_element017,C_element018,N_element012,O_element017,Na_element004,P_element004,S_element006,Cl_element003,K_element002]
  conduct = 2
  density = 1
  expand = 3
  formula = G4_BRAIN_ICRP
  name = G4_BRAIN_ICRP
  specific = 4
FEATURE [App::DocumentObjectGroupPython] C_element019  label="C_element : 4"  # scripted group (container) (typed FeaturePython)
  n = 4
  ref = C_element
FEATURE [App::DocumentObjectGroupPython] H_element018  label="H_element : 010"  # scripted group (container) (typed FeaturePython)
  n = 10
  ref = H_element
FEATURE [App::DocumentObjectGroupPython] G4_BUTANE  # scripted group (container) (typed FeaturePython)
  Dunit = g/cm3
  Dvalue = 0.00249343
  Group = -> [C_element019,H_element018]
  conduct = 2
  density = 1
  expand = 3
  formula = G4_BUTANE
  name = G4_BUTANE
  specific = 4
FEATURE [App::DocumentObjectGroupPython] C_element020  label="C_element : 008"  # scripted group (container) (typed FeaturePython)
  n = 4
  ref = C_element
FEATURE [App::DocumentObjectGroupPython] H_element019  label="H_element : 011"  # scripted group (container) (typed FeaturePython)
  n = 10
  ref = H_element
FEATURE [App::DocumentObjectGroupPython] O_element018  label="O_element : 007"  # scripted group (container) (typed FeaturePython)
  n = 1
  ref = O_element
FEATURE [App::DocumentObjectGroupPython] G4_N_BUTYL_ALCOHOL  label="G4_N-BUTYL_ALCOHOL"  # scripted group (container) (typed FeaturePython)
  Dunit = g/cm3
  Dvalue = 0.8098
  Group = -> [C_element020,H_element019,O_element018]
  conduct = 2
  density = 1
  expand = 3
  formula = G4_N-BUTYL_ALCOHOL
  name = G4_N-BUTYL_ALCOHOL
  specific = 4
FEATURE [App::DocumentObjectGroupPython] H_element020  label="H_element : 0.025"  # scripted group (container) (typed FeaturePython)
  n = 0.02468
FEATURE [App::DocumentObjectGroupPython] C_element021  label="C_element : 0.502"  # scripted group (container) (typed FeaturePython)
  n = 0.501611
FEATURE [App::DocumentObjectGroupPython] O_element019  label="O_element : 0.005"  # scripted group (container) (typed FeaturePython)
  n = 0.004527
FEATURE [App::DocumentObjectGroupPython] F_element004  label="F_element : 0.465"  # scripted group (container) (typed FeaturePython)
  n = 0.465209
FEATURE [App::DocumentObjectGroupPython] Si_element001  label="Si_element : 0.004"  # scripted group (container) (typed FeaturePython)
  n = 0.003973
FEATURE [App::DocumentObjectGroupPython] G4_C_552  label="G4_C-552"  # scripted group (container) (typed FeaturePython)
  Dunit = g/cm3
  Dvalue = 1.76
  Group = -> [H_element020,C_element021,O_element019,F_element004,Si_element001]
  conduct = 2
  density = 1
  expand = 3
  formula = G4_C-552
  name = G4_C-552
  specific = 4
FEATURE [App::DocumentObjectGroupPython] Cd_element001  label="Cd_element : 1"  # scripted group (container) (typed FeaturePython)
  n = 1
  ref = Cd_element
FEATURE [App::DocumentObjectGroupPython] Te_element001  label="Te_element : 1"  # scripted group (container) (typed FeaturePython)
  n = 1
  ref = Te_element
FEATURE [App::DocumentObjectGroupPython] G4_CADMIUM_TELLURIDE  # scripted group (container) (typed FeaturePython)
  Dunit = g/cm3
  Dvalue = 6.2
  Group = -> [Cd_element001,Te_element001]
  conduct = 2
  density = 1
  expand = 3
  formula = G4_CADMIUM_TELLURIDE
  name = G4_CADMIUM_TELLURIDE
  specific = 4
FEATURE [App::DocumentObjectGroupPython] Cd_element002  label="Cd_element : 002"  # scripted group (container) (typed FeaturePython)
  n = 1
  ref = Cd_element
FEATURE [App::DocumentObjectGroupPython] W_element001  label="W_element : 1"  # scripted group (container) (typed FeaturePython)
  n = 1
  ref = W_element
FEATURE [App::DocumentObjectGroupPython] O_element020  label="O_element : 008"  # scripted group (container) (typed FeaturePython)
  n = 4
  ref = O_element
FEATURE [App::DocumentObjectGroupPython] G4_CADMIUM_TUNGSTATE  # scripted group (container) (typed FeaturePython)
  Dunit = g/cm3
  Dvalue = 7.9
  Group = -> [Cd_element002,W_element001,O_element020]
  conduct = 2
  density = 1
  expand = 3
  formula = G4_CADMIUM_TUNGSTATE
  name = G4_CADMIUM_TUNGSTATE
  specific = 4
FEATURE [App::DocumentObjectGroupPython] Ca_element005  label="Ca_element : 1"  # scripted group (container) (typed FeaturePython)
  n = 1
  ref = Ca_element
FEATURE [App::DocumentObjectGroupPython] C_element022  label="C_element : 009"  # scripted group (container) (typed FeaturePython)
  n = 1
  ref = C_element
FEATURE [App::DocumentObjectGroupPython] O_element021  label="O_element : 009"  # scripted group (container) (typed FeaturePython)
  n = 3
  ref = O_element
FEATURE [App::DocumentObjectGroupPython] G4_CALCIUM_CARBONATE  # scripted group (container) (typed FeaturePython)
  Dunit = g/cm3
  Dvalue = 2.8
  Group = -> [Ca_element005,C_element022,O_element021]
  conduct = 2
  density = 1
  expand = 3
  formula = G4_CALCIUM_CARBONATE
  name = G4_CALCIUM_CARBONATE
  specific = 4
FEATURE [App::DocumentObjectGroupPython] Ca_element006  label="Ca_element : 002"  # scripted group (container) (typed FeaturePython)
  n = 1
  ref = Ca_element
FEATURE [App::DocumentObjectGroupPython] F_element005  label="F_element : 003"  # scripted group (container) (typed FeaturePython)
  n = 2
  ref = F_element
FEATURE [App::DocumentObjectGroupPython] G4_CALCIUM_FLUORIDE  # scripted group (container) (typed FeaturePython)
  Dunit = g/cm3
  Dvalue = 3.18
  Group = -> [Ca_element006,F_element005]
  conduct = 2
  density = 1
  expand = 3
  formula = G4_CALCIUM_FLUORIDE
  name = G4_CALCIUM_FLUORIDE
  specific = 4
FEATURE [App::DocumentObjectGroupPython] Ca_element007  label="Ca_element : 003"  # scripted group (container) (typed FeaturePython)
  n = 1
  ref = Ca_element
FEATURE [App::DocumentObjectGroupPython] O_element022  label="O_element : 010"  # scripted group (container) (typed FeaturePython)
  n = 1
  ref = O_element
FEATURE [App::DocumentObjectGroupPython] G4_CALCIUM_OXIDE  # scripted group (container) (typed FeaturePython)
  Dunit = g/cm3
  Dvalue = 3.3
  Group = -> [Ca_element007,O_element022]
  conduct = 2
  density = 1
  expand = 3
  formula = G4_CALCIUM_OXIDE
  name = G4_CALCIUM_OXIDE
  specific = 4
FEATURE [App::DocumentObjectGroupPython] Ca_element008  label="Ca_element : 004"  # scripted group (container) (typed FeaturePython)
  n = 1
  ref = Ca_element
FEATURE [App::DocumentObjectGroupPython] S_element007  label="S_element : 002"  # scripted group (container) (typed FeaturePython)
  n = 1
  ref = S_element
FEATURE [App::DocumentObjectGroupPython] O_element023  label="O_element : 011"  # scripted group (container) (typed FeaturePython)
  n = 4
  ref = O_element
FEATURE [App::DocumentObjectGroupPython] G4_CALCIUM_SULFATE  # scripted group (container) (typed FeaturePython)
  Dunit = g/cm3
  Dvalue = 2.96
  Group = -> [Ca_element008,S_element007,O_element023]
  conduct = 2
  density = 1
  expand = 3
  formula = G4_CALCIUM_SULFATE
  name = G4_CALCIUM_SULFATE
  specific = 4
FEATURE [App::DocumentObjectGroupPython] Ca_element009  label="Ca_element : 005"  # scripted group (container) (typed FeaturePython)
  n = 1
  ref = Ca_element
FEATURE [App::DocumentObjectGroupPython] W_element002  label="W_element : 002"  # scripted group (container) (typed FeaturePython)
  n = 1
  ref = W_element
FEATURE [App::DocumentObjectGroupPython] O_element024  label="O_element : 012"  # scripted group (container) (typed FeaturePython)
  n = 4
  ref = O_element
FEATURE [App::DocumentObjectGroupPython] G4_CALCIUM_TUNGSTATE  # scripted group (container) (typed FeaturePython)
  Dunit = g/cm3
  Dvalue = 6.062
  Group = -> [Ca_element009,W_element002,O_element024]
  conduct = 2
  density = 1
  expand = 3
  formula = G4_CALCIUM_TUNGSTATE
  name = G4_CALCIUM_TUNGSTATE
  specific = 4
FEATURE [App::DocumentObjectGroupPython] C_element023  label="C_element : 010"  # scripted group (container) (typed FeaturePython)
  n = 1
  ref = C_element
FEATURE [App::DocumentObjectGroupPython] O_element025  label="O_element : 013"  # scripted group (container) (typed FeaturePython)
  n = 2
  ref = O_element
FEATURE [App::DocumentObjectGroupPython] G4_CARBON_DIOXIDE  # scripted group (container) (typed FeaturePython)
  Dunit = g/cm3
  Dvalue = 0.00184212
  Group = -> [C_element023,O_element025]
  conduct = 2
  density = 1
  expand = 3
  formula = G4_CARBON_DIOXIDE
  name = G4_CARBON_DIOXIDE
  specific = 4
FEATURE [App::DocumentObjectGroupPython] C_element024  label="C_element : 011"  # scripted group (container) (typed FeaturePython)
  n = 1
  ref = C_element
FEATURE [App::DocumentObjectGroupPython] Cl_element004  label="Cl_element : 4"  # scripted group (container) (typed FeaturePython)
  n = 4
  ref = Cl_element
FEATURE [App::DocumentObjectGroupPython] G4_CARBON_TETRACHLORIDE  # scripted group (container) (typed FeaturePython)
  Dunit = g/cm3
  Dvalue = 1.594
  Group = -> [C_element024,Cl_element004]
  conduct = 2
  density = 1
  expand = 3
  formula = G4_CARBON_TETRACHLORIDE
  name = G4_CARBON_TETRACHLORIDE
  specific = 4
FEATURE [App::DocumentObjectGroupPython] C_element025  label="C_element : 012"  # scripted group (container) (typed FeaturePython)
  n = 6
  ref = C_element
FEATURE [App::DocumentObjectGroupPython] H_element021  label="H_element : 012"  # scripted group (container) (typed FeaturePython)
  n = 10
  ref = H_element
FEATURE [App::DocumentObjectGroupPython] O_element026  label="O_element : 5"  # scripted group (container) (typed FeaturePython)
  n = 5
  ref = O_element
FEATURE [App::DocumentObjectGroupPython] G4_CELLULOSE_CELLOPHANE  # scripted group (container) (typed FeaturePython)
  Dunit = g/cm3
  Dvalue = 1.42
  Group = -> [C_element025,H_element021,O_element026]
  conduct = 2
  density = 1
  expand = 3
  formula = G4_CELLULOSE_CELLOPHANE
  name = G4_CELLULOSE_CELLOPHANE
  specific = 4
FEATURE [App::DocumentObjectGroupPython] H_element022  label="H_element : 0.067"  # scripted group (container) (typed FeaturePython)
  n = 0.067125
FEATURE [App::DocumentObjectGroupPython] C_element026  label="C_element : 0.545"  # scripted group (container) (typed FeaturePython)
  n = 0.545403
FEATURE [App::DocumentObjectGroupPython] O_element027  label="O_element : 0.387"  # scripted group (container) (typed FeaturePython)
  n = 0.387472
FEATURE [App::DocumentObjectGroupPython] G4_CELLULOSE_BUTYRATE  # scripted group (container) (typed FeaturePython)
  Dunit = g/cm3
  Dvalue = 1.2
  Group = -> [H_element022,C_element026,O_element027]
  conduct = 2
  density = 1
  expand = 3
  formula = G4_CELLULOSE_BUTYRATE
  name = G4_CELLULOSE_BUTYRATE
  specific = 4
FEATURE [App::DocumentObjectGroupPython] H_element023  label="H_element : 0.029"  # scripted group (container) (typed FeaturePython)
  n = 0.029216
FEATURE [App::DocumentObjectGroupPython] C_element027  label="C_element : 0.271"  # scripted group (container) (typed FeaturePython)
  n = 0.271296
FEATURE [App::DocumentObjectGroupPython] N_element013  label="N_element : 0.121"  # scripted group (container) (typed FeaturePython)
  n = 0.121276
FEATURE [App::DocumentObjectGroupPython] O_element028  label="O_element : 0.578"  # scripted group (container) (typed FeaturePython)
  n = 0.578212
FEATURE [App::DocumentObjectGroupPython] G4_CELLULOSE_NITRATE  # scripted group (container) (typed FeaturePython)
  Dunit = g/cm3
  Dvalue = 1.49
  Group = -> [H_element023,C_element027,N_element013,O_element028]
  conduct = 2
  density = 1
  expand = 3
  formula = G4_CELLULOSE_NITRATE
  name = G4_CELLULOSE_NITRATE
  specific = 4
FEATURE [App::DocumentObjectGroupPython] H_element024  label="H_element : 0.108"  # scripted group (container) (typed FeaturePython)
  n = 0.107596
FEATURE [App::DocumentObjectGroupPython] N_element014  label="N_element : 0.001"  # scripted group (container) (typed FeaturePython)
  n = 0.0008
FEATURE [App::DocumentObjectGroupPython] O_element029  label="O_element : 0.875"  # scripted group (container) (typed FeaturePython)
  n = 0.874976
FEATURE [App::DocumentObjectGroupPython] S_element008  label="S_element : 0.015"  # scripted group (container) (typed FeaturePython)
  n = 0.014627
FEATURE [App::DocumentObjectGroupPython] Ce_element001  label="Ce_element : 0.002"  # scripted group (container) (typed FeaturePython)
  n = 0.002001
FEATURE [App::DocumentObjectGroupPython] G4_CERIC_SULFATE  # scripted group (container) (typed FeaturePython)
  Dunit = g/cm3
  Dvalue = 1.03
  Group = -> [H_element024,N_element014,O_element029,S_element008,Ce_element001]
  conduct = 2
  density = 1
  expand = 3
  formula = G4_CERIC_SULFATE
  name = G4_CERIC_SULFATE
  specific = 4
FEATURE [App::DocumentObjectGroupPython] Cs_element001  label="Cs_element : 1"  # scripted group (container) (typed FeaturePython)
  n = 1
  ref = Cs_element
FEATURE [App::DocumentObjectGroupPython] F_element006  label="F_element : 1"  # scripted group (container) (typed FeaturePython)
  n = 1
  ref = F_element
FEATURE [App::DocumentObjectGroupPython] G4_CESIUM_FLUORIDE  # scripted group (container) (typed FeaturePython)
  Dunit = g/cm3
  Dvalue = 4.115
  Group = -> [Cs_element001,F_element006]
  conduct = 2
  density = 1
  expand = 3
  formula = G4_CESIUM_FLUORIDE
  name = G4_CESIUM_FLUORIDE
  specific = 4
FEATURE [App::DocumentObjectGroupPython] Cs_element002  label="Cs_element : 002"  # scripted group (container) (typed FeaturePython)
  n = 1
  ref = Cs_element
FEATURE [App::DocumentObjectGroupPython] I_element001  label="I_element : 1"  # scripted group (container) (typed FeaturePython)
  n = 1
  ref = I_element
FEATURE [App::DocumentObjectGroupPython] G4_CESIUM_IODIDE  # scripted group (container) (typed FeaturePython)
  Dunit = g/cm3
  Dvalue = 4.51
  Group = -> [Cs_element002,I_element001]
  conduct = 2
  density = 1
  expand = 3
  formula = G4_CESIUM_IODIDE
  name = G4_CESIUM_IODIDE
  specific = 4
FEATURE [App::DocumentObjectGroupPython] C_element028  label="C_element : 013"  # scripted group (container) (typed FeaturePython)
  n = 6
  ref = C_element
FEATURE [App::DocumentObjectGroupPython] H_element025  label="H_element : 013"  # scripted group (container) (typed FeaturePython)
  n = 5
  ref = H_element
FEATURE [App::DocumentObjectGroupPython] Cl_element005  label="Cl_element : 1"  # scripted group (container) (typed FeaturePython)
  n = 1
  ref = Cl_element
FEATURE [App::DocumentObjectGroupPython] G4_CHLOROBENZENE  # scripted group (container) (typed FeaturePython)
  Dunit = g/cm3
  Dvalue = 1.1058
  Group = -> [C_element028,H_element025,Cl_element005]
  conduct = 2
  density = 1
  expand = 3
  formula = G4_CHLOROBENZENE
  name = G4_CHLOROBENZENE
  specific = 4
FEATURE [App::DocumentObjectGroupPython] C_element029  label="C_element : 014"  # scripted group (container) (typed FeaturePython)
  n = 1
  ref = C_element
FEATURE [App::DocumentObjectGroupPython] H_element026  label="H_element : 1"  # scripted group (container) (typed FeaturePython)
  n = 1
  ref = H_element
FEATURE [App::DocumentObjectGroupPython] Cl_element006  label="Cl_element : 3"  # scripted group (container) (typed FeaturePython)
  n = 3
  ref = Cl_element
FEATURE [App::DocumentObjectGroupPython] G4_CHLOROFORM  # scripted group (container) (typed FeaturePython)
  Dunit = g/cm3
  Dvalue = 1.4832
  Group = -> [C_element029,H_element026,Cl_element006]
  conduct = 2
  density = 1
  expand = 3
  formula = G4_CHLOROFORM
  name = G4_CHLOROFORM
  specific = 4
FEATURE [App::DocumentObjectGroupPython] H_element027  label="H_element : 0.010"  # scripted group (container) (typed FeaturePython)
  n = 0.01
FEATURE [App::DocumentObjectGroupPython] C_element030  label="C_element : 0.001"  # scripted group (container) (typed FeaturePython)
  n = 0.001
FEATURE [App::DocumentObjectGroupPython] O_element030  label="O_element : 0.529"  # scripted group (container) (typed FeaturePython)
  n = 0.529107
FEATURE [App::DocumentObjectGroupPython] Na_element005  label="Na_element : 0.016"  # scripted group (container) (typed FeaturePython)
  n = 0.016
FEATURE [App::DocumentObjectGroupPython] Mg_element003  label="Mg_element : 0.004"  # scripted group (container) (typed FeaturePython)
  n = 0.002
FEATURE [App::DocumentObjectGroupPython] Al_element002  label="Al_element : 0.034"  # scripted group (container) (typed FeaturePython)
  n = 0.033872
FEATURE [App::DocumentObjectGroupPython] Si_element002  label="Si_element : 0.337"  # scripted group (container) (typed FeaturePython)
  n = 0.337021
FEATURE [App::DocumentObjectGroupPython] K_element003  label="K_element : 0.013"  # scripted group (container) (typed FeaturePython)
  n = 0.013
FEATURE [App::DocumentObjectGroupPython] Ca_element010  label="Ca_element : 0.044"  # scripted group (container) (typed FeaturePython)
  n = 0.044
FEATURE [App::DocumentObjectGroupPython] Fe_element002  label="Fe_element : 0.014"  # scripted group (container) (typed FeaturePython)
  n = 0.014
FEATURE [App::DocumentObjectGroupPython] G4_CONCRETE  # scripted group (container) (typed FeaturePython)
  Dunit = g/cm3
  Dvalue = 2.3
  Group = -> [H_element027,C_element030,O_element030,Na_element005,Mg_element003,Al_element002,Si_element002,K_element003,Ca_element010,Fe_element002]
  conduct = 2
  density = 1
  expand = 3
  formula = G4_CONCRETE
  name = G4_CONCRETE
  specific = 4
FEATURE [App::DocumentObjectGroupPython] C_element031  label="C_element : 015"  # scripted group (container) (typed FeaturePython)
  n = 6
  ref = C_element
FEATURE [App::DocumentObjectGroupPython] H_element028  label="H_element : 12"  # scripted group (container) (typed FeaturePython)
  n = 12
  ref = H_element
FEATURE [App::DocumentObjectGroupPython] G4_CYCLOHEXANE  # scripted group (container) (typed FeaturePython)
  Dunit = g/cm3
  Dvalue = 0.779
  Group = -> [C_element031,H_element028]
  conduct = 2
  density = 1
  expand = 3
  formula = G4_CYCLOHEXANE
  name = G4_CYCLOHEXANE
  specific = 4
FEATURE [App::DocumentObjectGroupPython] C_element032  label="C_element : 016"  # scripted group (container) (typed FeaturePython)
  n = 6
  ref = C_element
FEATURE [App::DocumentObjectGroupPython] H_element029  label="H_element : 4"  # scripted group (container) (typed FeaturePython)
  n = 4
  ref = H_element
FEATURE [App::DocumentObjectGroupPython] Cl_element007  label="Cl_element : 2"  # scripted group (container) (typed FeaturePython)
  n = 2
  ref = Cl_element
FEATURE [App::DocumentObjectGroupPython] G4_1_2_DICHLOROBENZENE  label="G4_1.2-DICHLOROBENZENE"  # scripted group (container) (typed FeaturePython)
  Dunit = g/cm3
  Dvalue = 1.3048
  Group = -> [C_element032,H_element029,Cl_element007]
  conduct = 2
  density = 1
  expand = 3
  formula = G4_1.2-DICHLOROBENZENE
  name = G4_1.2-DICHLOROBENZENE
  specific = 4
FEATURE [App::DocumentObjectGroupPython] C_element033  label="C_element : 017"  # scripted group (container) (typed FeaturePython)
  n = 4
  ref = C_element
FEATURE [App::DocumentObjectGroupPython] H_element030  label="H_element : 8"  # scripted group (container) (typed FeaturePython)
  n = 8
  ref = H_element
FEATURE [App::DocumentObjectGroupPython] O_element031  label="O_element : 014"  # scripted group (container) (typed FeaturePython)
  n = 1
  ref = O_element
FEATURE [App::DocumentObjectGroupPython] Cl_element008  label="Cl_element : 005"  # scripted group (container) (typed FeaturePython)
  n = 2
  ref = Cl_element
FEATURE [App::DocumentObjectGroupPython] G4_DICHLORODIETHYL_ETHER  # scripted group (container) (typed FeaturePython)
  Dunit = g/cm3
  Dvalue = 1.2199
  Group = -> [C_element033,H_element030,O_element031,Cl_element008]
  conduct = 2
  density = 1
  expand = 3
  formula = G4_DICHLORODIETHYL_ETHER
  name = G4_DICHLORODIETHYL_ETHER
  specific = 4
FEATURE [App::DocumentObjectGroupPython] C_element034  label="C_element : 018"  # scripted group (container) (typed FeaturePython)
  n = 2
  ref = C_element
FEATURE [App::DocumentObjectGroupPython] H_element031  label="H_element : 014"  # scripted group (container) (typed FeaturePython)
  n = 4
  ref = H_element
FEATURE [App::DocumentObjectGroupPython] Cl_element009  label="Cl_element : 006"  # scripted group (container) (typed FeaturePython)
  n = 2
  ref = Cl_element
FEATURE [App::DocumentObjectGroupPython] G4_1_2_DICHLOROETHANE  label="G4_1.2-DICHLOROETHANE"  # scripted group (container) (typed FeaturePython)
  Dunit = g/cm3
  Dvalue = 1.2351
  Group = -> [C_element034,H_element031,Cl_element009]
  conduct = 2
  density = 1
  expand = 3
  formula = G4_1.2-DICHLOROETHANE
  name = G4_1.2-DICHLOROETHANE
  specific = 4
FEATURE [App::DocumentObjectGroupPython] C_element035  label="C_element : 019"  # scripted group (container) (typed FeaturePython)
  n = 4
  ref = C_element
FEATURE [App::DocumentObjectGroupPython] H_element032  label="H_element : 015"  # scripted group (container) (typed FeaturePython)
  n = 10
  ref = H_element
FEATURE [App::DocumentObjectGroupPython] O_element032  label="O_element : 015"  # scripted group (container) (typed FeaturePython)
  n = 1
  ref = O_element
FEATURE [App::DocumentObjectGroupPython] G4_DIETHYL_ETHER  # scripted group (container) (typed FeaturePython)
  Dunit = g/cm3
  Dvalue = 0.71378
  Group = -> [C_element035,H_element032,O_element032]
  conduct = 2
  density = 1
  expand = 3
  formula = G4_DIETHYL_ETHER
  name = G4_DIETHYL_ETHER
  specific = 4
FEATURE [App::DocumentObjectGroupPython] C_element036  label="C_element : 020"  # scripted group (container) (typed FeaturePython)
  n = 3
  ref = C_element
FEATURE [App::DocumentObjectGroupPython] H_element033  label="H_element : 016"  # scripted group (container) (typed FeaturePython)
  n = 7
  ref = H_element
FEATURE [App::DocumentObjectGroupPython] N_element015  label="N_element : 008"  # scripted group (container) (typed FeaturePython)
  n = 1
  ref = N_element
FEATURE [App::DocumentObjectGroupPython] O_element033  label="O_element : 016"  # scripted group (container) (typed FeaturePython)
  n = 1
  ref = O_element
FEATURE [App::DocumentObjectGroupPython] G4_N_N_DIMETHYL_FORMAMIDE  label="G4_N.N-DIMETHYL_FORMAMIDE"  # scripted group (container) (typed FeaturePython)
  Dunit = g/cm3
  Dvalue = 0.9487
  Group = -> [C_element036,H_element033,N_element015,O_element033]
  conduct = 2
  density = 1
  expand = 3
  formula = G4_N.N-DIMETHYL_FORMAMIDE
  name = G4_N.N-DIMETHYL_FORMAMIDE
  specific = 4
FEATURE [App::DocumentObjectGroupPython] C_element037  label="C_element : 021"  # scripted group (container) (typed FeaturePython)
  n = 2
  ref = C_element
FEATURE [App::DocumentObjectGroupPython] H_element034  label="H_element : 017"  # scripted group (container) (typed FeaturePython)
  n = 6
  ref = H_element
FEATURE [App::DocumentObjectGroupPython] O_element034  label="O_element : 017"  # scripted group (container) (typed FeaturePython)
  n = 1
  ref = O_element
FEATURE [App::DocumentObjectGroupPython] S_element009  label="S_element : 003"  # scripted group (container) (typed FeaturePython)
  n = 1
  ref = S_element
FEATURE [App::DocumentObjectGroupPython] G4_DIMETHYL_SULFOXIDE  # scripted group (container) (typed FeaturePython)
  Dunit = g/cm3
  Dvalue = 1.1014
  Group = -> [C_element037,H_element034,O_element034,S_element009]
  conduct = 2
  density = 1
  expand = 3
  formula = G4_DIMETHYL_SULFOXIDE
  name = G4_DIMETHYL_SULFOXIDE
  specific = 4
FEATURE [App::DocumentObjectGroupPython] C_element038  label="C_element : 022"  # scripted group (container) (typed FeaturePython)
  n = 2
  ref = C_element
FEATURE [App::DocumentObjectGroupPython] H_element035  label="H_element : 018"  # scripted group (container) (typed FeaturePython)
  n = 6
  ref = H_element
FEATURE [App::DocumentObjectGroupPython] G4_ETHANE  # scripted group (container) (typed FeaturePython)
  Dunit = g/cm3
  Dvalue = 0.00125324
  Group = -> [C_element038,H_element035]
  conduct = 2
  density = 1
  expand = 3
  formula = G4_ETHANE
  name = G4_ETHANE
  specific = 4
FEATURE [App::DocumentObjectGroupPython] C_element039  label="C_element : 023"  # scripted group (container) (typed FeaturePython)
  n = 2
  ref = C_element
FEATURE [App::DocumentObjectGroupPython] H_element036  label="H_element : 019"  # scripted group (container) (typed FeaturePython)
  n = 6
  ref = H_element
FEATURE [App::DocumentObjectGroupPython] O_element035  label="O_element : 018"  # scripted group (container) (typed FeaturePython)
  n = 1
  ref = O_element
FEATURE [App::DocumentObjectGroupPython] G4_ETHYL_ALCOHOL  # scripted group (container) (typed FeaturePython)
  Dunit = g/cm3
  Dvalue = 0.7893
  Group = -> [C_element039,H_element036,O_element035]
  conduct = 2
  density = 1
  expand = 3
  formula = G4_ETHYL_ALCOHOL
  name = G4_ETHYL_ALCOHOL
  specific = 4
FEATURE [App::DocumentObjectGroupPython] H_element037  label="H_element : 0.090"  # scripted group (container) (typed FeaturePython)
  n = 0.090027
FEATURE [App::DocumentObjectGroupPython] C_element040  label="C_element : 0.585"  # scripted group (container) (typed FeaturePython)
  n = 0.585182
FEATURE [App::DocumentObjectGroupPython] O_element036  label="O_element : 0.325"  # scripted group (container) (typed FeaturePython)
  n = 0.324791
FEATURE [App::DocumentObjectGroupPython] G4_ETHYL_CELLULOSE  # scripted group (container) (typed FeaturePython)
  Dunit = g/cm3
  Dvalue = 1.13
  Group = -> [H_element037,C_element040,O_element036]
  conduct = 2
  density = 1
  expand = 3
  formula = G4_ETHYL_CELLULOSE
  name = G4_ETHYL_CELLULOSE
  specific = 4
FEATURE [App::DocumentObjectGroupPython] C_element041  label="C_element : 024"  # scripted group (container) (typed FeaturePython)
  n = 2
  ref = C_element
FEATURE [App::DocumentObjectGroupPython] H_element038  label="H_element : 020"  # scripted group (container) (typed FeaturePython)
  n = 4
  ref = H_element
FEATURE [App::DocumentObjectGroupPython] G4_ETHYLENE  # scripted group (container) (typed FeaturePython)
  Dunit = g/cm3
  Dvalue = 0.00117497
  Group = -> [C_element041,H_element038]
  conduct = 2
  density = 1
  expand = 3
  formula = G4_ETHYLENE
  name = G4_ETHYLENE
  specific = 4
FEATURE [App::DocumentObjectGroupPython] H_element039  label="H_element : 0.096"  # scripted group (container) (typed FeaturePython)
  n = 0.096
FEATURE [App::DocumentObjectGroupPython] C_element042  label="C_element : 0.195"  # scripted group (container) (typed FeaturePython)
  n = 0.195
FEATURE [App::DocumentObjectGroupPython] N_element016  label="N_element : 0.057"  # scripted group (container) (typed FeaturePython)
  n = 0.057
FEATURE [App::DocumentObjectGroupPython] O_element037  label="O_element : 0.646"  # scripted group (container) (typed FeaturePython)
  n = 0.646
FEATURE [App::DocumentObjectGroupPython] Na_element006  label="Na_element : 0.017"  # scripted group (container) (typed FeaturePython)
  n = 0.001
FEATURE [App::DocumentObjectGroupPython] P_element005  label="P_element : 0.104"  # scripted group (container) (typed FeaturePython)
  n = 0.001
FEATURE [App::DocumentObjectGroupPython] S_element010  label="S_element : 0.016"  # scripted group (container) (typed FeaturePython)
  n = 0.003
FEATURE [App::DocumentObjectGroupPython] Cl_element010  label="Cl_element : 0.005"  # scripted group (container) (typed FeaturePython)
  n = 0.001
FEATURE [App::DocumentObjectGroupPython] G4_EYE_LENS_ICRP  # scripted group (container) (typed FeaturePython)
  Dunit = g/cm3
  Dvalue = 1.07
  Group = -> [H_element039,C_element042,N_element016,O_element037,Na_element006,P_element005,S_element010,Cl_element010]
  conduct = 2
  density = 1
  expand = 3
  formula = G4_EYE_LENS_ICRP
  name = G4_EYE_LENS_ICRP
  specific = 4
FEATURE [App::DocumentObjectGroupPython] Fe_element003  label="Fe_element : 2"  # scripted group (container) (typed FeaturePython)
  n = 2
  ref = Fe_element
FEATURE [App::DocumentObjectGroupPython] O_element038  label="O_element : 019"  # scripted group (container) (typed FeaturePython)
  n = 3
  ref = O_element
FEATURE [App::DocumentObjectGroupPython] G4_FERRIC_OXIDE  # scripted group (container) (typed FeaturePython)
  Dunit = g/cm3
  Dvalue = 5.2
  Group = -> [Fe_element003,O_element038]
  conduct = 2
  density = 1
  expand = 3
  formula = G4_FERRIC_OXIDE
  name = G4_FERRIC_OXIDE
  specific = 4
FEATURE [App::DocumentObjectGroupPython] Fe_element004  label="Fe_element : 1"  # scripted group (container) (typed FeaturePython)
  n = 1
  ref = Fe_element
FEATURE [App::DocumentObjectGroupPython] B_element003  label="B_element : 1"  # scripted group (container) (typed FeaturePython)
  n = 1
  ref = B_element
FEATURE [App::DocumentObjectGroupPython] G4_FERROBORIDE  # scripted group (container) (typed FeaturePython)
  Dunit = g/cm3
  Dvalue = 7.15
  Group = -> [Fe_element004,B_element003]
  conduct = 2
  density = 1
  expand = 3
  formula = G4_FERROBORIDE
  name = G4_FERROBORIDE
  specific = 4
FEATURE [App::DocumentObjectGroupPython] Fe_element005  label="Fe_element : 003"  # scripted group (container) (typed FeaturePython)
  n = 1
  ref = Fe_element
FEATURE [App::DocumentObjectGroupPython] O_element039  label="O_element : 020"  # scripted group (container) (typed FeaturePython)
  n = 1
  ref = O_element
FEATURE [App::DocumentObjectGroupPython] G4_FERROUS_OXIDE  # scripted group (container) (typed FeaturePython)
  Dunit = g/cm3
  Dvalue = 5.7
  Group = -> [Fe_element005,O_element039]
  conduct = 2
  density = 1
  expand = 3
  formula = G4_FERROUS_OXIDE
  name = G4_FERROUS_OXIDE
  specific = 4
FEATURE [App::DocumentObjectGroupPython] H_element040  label="H_element : 0.115"  # scripted group (container) (typed FeaturePython)
  n = 0.108259
FEATURE [App::DocumentObjectGroupPython] N_element017  label="N_element : 0.000"  # scripted group (container) (typed FeaturePython)
  n = 2.7e-05
FEATURE [App::DocumentObjectGroupPython] O_element040  label="O_element : 0.879"  # scripted group (container) (typed FeaturePython)
  n = 0.878636
FEATURE [App::DocumentObjectGroupPython] Na_element007  label="Na_element : 0.000"  # scripted group (container) (typed FeaturePython)
  n = 2.2e-05
FEATURE [App::DocumentObjectGroupPython] S_element011  label="S_element : 0.013"  # scripted group (container) (typed FeaturePython)
  n = 0.012968
FEATURE [App::DocumentObjectGroupPython] Cl_element011  label="Cl_element : 0.000"  # scripted group (container) (typed FeaturePython)
  n = 3.4e-05
FEATURE [App::DocumentObjectGroupPython] Fe_element006  label="Fe_element : 0.000"  # scripted group (container) (typed FeaturePython)
  n = 5.4e-05
FEATURE [App::DocumentObjectGroupPython] G4_FERROUS_SULFATE  # scripted group (container) (typed FeaturePython)
  Dunit = g/cm3
  Dvalue = 1.024
  Group = -> [H_element040,N_element017,O_element040,Na_element007,S_element011,Cl_element011,Fe_element006]
  conduct = 2
  density = 1
  expand = 3
  formula = G4_FERROUS_SULFATE
  name = G4_FERROUS_SULFATE
  specific = 4
FEATURE [App::DocumentObjectGroupPython] C_element043  label="C_element : 0.099"  # scripted group (container) (typed FeaturePython)
  n = 0.099335
FEATURE [App::DocumentObjectGroupPython] F_element007  label="F_element : 0.314"  # scripted group (container) (typed FeaturePython)
  n = 0.314247
FEATURE [App::DocumentObjectGroupPython] Cl_element012  label="Cl_element : 0.586"  # scripted group (container) (typed FeaturePython)
  n = 0.586418
FEATURE [App::DocumentObjectGroupPython] G4_FREON_12  label="G4_FREON-12"  # scripted group (container) (typed FeaturePython)
  Dunit = g/cm3
  Dvalue = 1.12
  Group = -> [C_element043,F_element007,Cl_element012]
  conduct = 2
  density = 1
  expand = 3
  formula = G4_FREON-12
  name = G4_FREON-12
  specific = 4
FEATURE [App::DocumentObjectGroupPython] C_element044  label="C_element : 0.057"  # scripted group (container) (typed FeaturePython)
  n = 0.057245
FEATURE [App::DocumentObjectGroupPython] F_element008  label="F_element : 0.181"  # scripted group (container) (typed FeaturePython)
  n = 0.181096
FEATURE [App::DocumentObjectGroupPython] Br_element001  label="Br_element : 0.762"  # scripted group (container) (typed FeaturePython)
  n = 0.761659
FEATURE [App::DocumentObjectGroupPython] G4_FREON_12B2  label="G4_FREON-12B2"  # scripted group (container) (typed FeaturePython)
  Dunit = g/cm3
  Dvalue = 1.8
  Group = -> [C_element044,F_element008,Br_element001]
  conduct = 2
  density = 1
  expand = 3
  formula = G4_FREON-12B2
  name = G4_FREON-12B2
  specific = 4
FEATURE [App::DocumentObjectGroupPython] C_element045  label="C_element : 0.115"  # scripted group (container) (typed FeaturePython)
  n = 0.114983
FEATURE [App::DocumentObjectGroupPython] F_element009  label="F_element : 0.546"  # scripted group (container) (typed FeaturePython)
  n = 0.545621
FEATURE [App::DocumentObjectGroupPython] Cl_element013  label="Cl_element : 0.339"  # scripted group (container) (typed FeaturePython)
  n = 0.339396
FEATURE [App::DocumentObjectGroupPython] G4_FREON_13  label="G4_FREON-13"  # scripted group (container) (typed FeaturePython)
  Dunit = g/cm3
  Dvalue = 0.95
  Group = -> [C_element045,F_element009,Cl_element013]
  conduct = 2
  density = 1
  expand = 3
  formula = G4_FREON-13
  name = G4_FREON-13
  specific = 4
FEATURE [App::DocumentObjectGroupPython] C_element046  label="C_element : 025"  # scripted group (container) (typed FeaturePython)
  n = 1
  ref = C_element
FEATURE [App::DocumentObjectGroupPython] F_element010  label="F_element : 3"  # scripted group (container) (typed FeaturePython)
  n = 3
  ref = F_element
FEATURE [App::DocumentObjectGroupPython] Br_element002  label="Br_element : 1"  # scripted group (container) (typed FeaturePython)
  n = 1
  ref = Br_element
FEATURE [App::DocumentObjectGroupPython] G4_FREON_13B1  label="G4_FREON-13B1"  # scripted group (container) (typed FeaturePython)
  Dunit = g/cm3
  Dvalue = 1.5
  Group = -> [C_element046,F_element010,Br_element002]
  conduct = 2
  density = 1
  expand = 3
  formula = G4_FREON-13B1
  name = G4_FREON-13B1
  specific = 4
FEATURE [App::DocumentObjectGroupPython] C_element047  label="C_element : 0.061"  # scripted group (container) (typed FeaturePython)
  n = 0.061309
FEATURE [App::DocumentObjectGroupPython] F_element011  label="F_element : 0.291"  # scripted group (container) (typed FeaturePython)
  n = 0.290924
FEATURE [App::DocumentObjectGroupPython] I_element002  label="I_element : 0.648"  # scripted group (container) (typed FeaturePython)
  n = 0.647767
FEATURE [App::DocumentObjectGroupPython] G4_FREON_13I1  label="G4_FREON-13I1"  # scripted group (container) (typed FeaturePython)
  Dunit = g/cm3
  Dvalue = 1.8
  Group = -> [C_element047,F_element011,I_element002]
  conduct = 2
  density = 1
  expand = 3
  formula = G4_FREON-13I1
  name = G4_FREON-13I1
  specific = 4
FEATURE [App::DocumentObjectGroupPython] Gd_element001  label="Gd_element : 2"  # scripted group (container) (typed FeaturePython)
  n = 2
  ref = Gd_element
FEATURE [App::DocumentObjectGroupPython] O_element041  label="O_element : 021"  # scripted group (container) (typed FeaturePython)
  n = 2
  ref = O_element
FEATURE [App::DocumentObjectGroupPython] S_element012  label="S_element : 004"  # scripted group (container) (typed FeaturePython)
  n = 1
  ref = S_element
FEATURE [App::DocumentObjectGroupPython] G4_GADOLINIUM_OXYSULFIDE  # scripted group (container) (typed FeaturePython)
  Dunit = g/cm3
  Dvalue = 7.44
  Group = -> [Gd_element001,O_element041,S_element012]
  conduct = 2
  density = 1
  expand = 3
  formula = G4_GADOLINIUM_OXYSULFIDE
  name = G4_GADOLINIUM_OXYSULFIDE
  specific = 4
FEATURE [App::DocumentObjectGroupPython] Ga_element001  label="Ga_element : 1"  # scripted group (container) (typed FeaturePython)
  n = 1
  ref = Ga_element
FEATURE [App::DocumentObjectGroupPython] As_element001  label="As_element : 1"  # scripted group (container) (typed FeaturePython)
  n = 1
  ref = As_element
FEATURE [App::DocumentObjectGroupPython] G4_GALLIUM_ARSENIDE  # scripted group (container) (typed FeaturePython)
  Dunit = g/cm3
  Dvalue = 5.31
  Group = -> [Ga_element001,As_element001]
  conduct = 2
  density = 1
  expand = 3
  formula = G4_GALLIUM_ARSENIDE
  name = G4_GALLIUM_ARSENIDE
  specific = 4
FEATURE [App::DocumentObjectGroupPython] H_element041  label="H_element : 0.081"  # scripted group (container) (typed FeaturePython)
  n = 0.08118
FEATURE [App::DocumentObjectGroupPython] C_element048  label="C_element : 0.416"  # scripted group (container) (typed FeaturePython)
  n = 0.41606
FEATURE [App::DocumentObjectGroupPython] N_element018  label="N_element : 0.111"  # scripted group (container) (typed FeaturePython)
  n = 0.11124
FEATURE [App::DocumentObjectGroupPython] O_element042  label="O_element : 0.381"  # scripted group (container) (typed FeaturePython)
  n = 0.38064
FEATURE [App::DocumentObjectGroupPython] S_element013  label="S_element : 0.011"  # scripted group (container) (typed FeaturePython)
  n = 0.01088
FEATURE [App::DocumentObjectGroupPython] G4_GEL_PHOTO_EMULSION  # scripted group (container) (typed FeaturePython)
  Dunit = g/cm3
  Dvalue = 1.2914
  Group = -> [H_element041,C_element048,N_element018,O_element042,S_element013]
  conduct = 2
  density = 1
  expand = 3
  formula = G4_GEL_PHOTO_EMULSION
  name = G4_GEL_PHOTO_EMULSION
  specific = 4
FEATURE [App::DocumentObjectGroupPython] B_element004  label="B_element : 0.040"  # scripted group (container) (typed FeaturePython)
  n = 0.0400639
FEATURE [App::DocumentObjectGroupPython] O_element043  label="O_element : 0.540"  # scripted group (container) (typed FeaturePython)
  n = 0.539561
FEATURE [App::DocumentObjectGroupPython] Na_element008  label="Na_element : 0.028"  # scripted group (container) (typed FeaturePython)
  n = 0.0281909
FEATURE [App::DocumentObjectGroupPython] Al_element003  label="Al_element : 0.012"  # scripted group (container) (typed FeaturePython)
  n = 0.011644
FEATURE [App::DocumentObjectGroupPython] Si_element003  label="Si_element : 0.377"  # scripted group (container) (typed FeaturePython)
  n = 0.377219
FEATURE [App::DocumentObjectGroupPython] K_element004  label="K_element : 0.014"  # scripted group (container) (typed FeaturePython)
  n = 0.00332099
FEATURE [App::DocumentObjectGroupPython] G4_Pyrex_Glass  # scripted group (container) (typed FeaturePython)
  Dunit = g/cm3
  Dvalue = 2.23
  Group = -> [B_element004,O_element043,Na_element008,Al_element003,Si_element003,K_element004]
  conduct = 2
  density = 1
  expand = 3
  formula = G4_Pyrex_Glass
  name = G4_Pyrex_Glass
  specific = 4
FEATURE [App::DocumentObjectGroupPython] O_element044  label="O_element : 0.156"  # scripted group (container) (typed FeaturePython)
  n = 0.156453
FEATURE [App::DocumentObjectGroupPython] Si_element004  label="Si_element : 0.081"  # scripted group (container) (typed FeaturePython)
  n = 0.080866
FEATURE [App::DocumentObjectGroupPython] Ti_element001  label="Ti_element : 0.008"  # scripted group (container) (typed FeaturePython)
  n = 0.008092
FEATURE [App::DocumentObjectGroupPython] As_element002  label="As_element : 0.003"  # scripted group (container) (typed FeaturePython)
  n = 0.002651
FEATURE [App::DocumentObjectGroupPython] Pb_element001  label="Pb_element : 0.752"  # scripted group (container) (typed FeaturePython)
  n = 0.751938
FEATURE [App::DocumentObjectGroupPython] G4_GLASS_LEAD  # scripted group (container) (typed FeaturePython)
  Dunit = g/cm3
  Dvalue = 6.22
  Group = -> [O_element044,Si_element004,Ti_element001,As_element002,Pb_element001]
  conduct = 2
  density = 1
  expand = 3
  formula = G4_GLASS_LEAD
  name = G4_GLASS_LEAD
  specific = 4
FEATURE [App::DocumentObjectGroupPython] O_element045  label="O_element : 0.460"  # scripted group (container) (typed FeaturePython)
  n = 0.4598
FEATURE [App::DocumentObjectGroupPython] Na_element009  label="Na_element : 0.096"  # scripted group (container) (typed FeaturePython)
  n = 0.0964411
FEATURE [App::DocumentObjectGroupPython] Si_element005  label="Si_element : 0.378"  # scripted group (container) (typed FeaturePython)
  n = 0.336553
FEATURE [App::DocumentObjectGroupPython] Ca_element011  label="Ca_element : 0.107"  # scripted group (container) (typed FeaturePython)
  n = 0.107205
FEATURE [App::DocumentObjectGroupPython] G4_GLASS_PLATE  # scripted group (container) (typed FeaturePython)
  Dunit = g/cm3
  Dvalue = 2.4
  Group = -> [O_element045,Na_element009,Si_element005,Ca_element011]
  conduct = 2
  density = 1
  expand = 3
  formula = G4_GLASS_PLATE
  name = G4_GLASS_PLATE
  specific = 4
FEATURE [App::DocumentObjectGroupPython] C_element049  label="C_element : 026"  # scripted group (container) (typed FeaturePython)
  n = 5
  ref = C_element
FEATURE [App::DocumentObjectGroupPython] H_element042  label="H_element : 021"  # scripted group (container) (typed FeaturePython)
  n = 10
  ref = H_element
FEATURE [App::DocumentObjectGroupPython] N_element019  label="N_element : 2"  # scripted group (container) (typed FeaturePython)
  n = 2
  ref = N_element
FEATURE [App::DocumentObjectGroupPython] O_element046  label="O_element : 022"  # scripted group (container) (typed FeaturePython)
  n = 3
  ref = O_element
FEATURE [App::DocumentObjectGroupPython] G4_GLUTAMINE  # scripted group (container) (typed FeaturePython)
  Dunit = g/cm3
  Dvalue = 1.46
  Group = -> [C_element049,H_element042,N_element019,O_element046]
  conduct = 2
  density = 1
  expand = 3
  formula = G4_GLUTAMINE
  name = G4_GLUTAMINE
  specific = 4
FEATURE [App::DocumentObjectGroupPython] C_element050  label="C_element : 027"  # scripted group (container) (typed FeaturePython)
  n = 3
  ref = C_element
FEATURE [App::DocumentObjectGroupPython] H_element043  label="H_element : 022"  # scripted group (container) (typed FeaturePython)
  n = 8
  ref = H_element
FEATURE [App::DocumentObjectGroupPython] O_element047  label="O_element : 023"  # scripted group (container) (typed FeaturePython)
  n = 3
  ref = O_element
FEATURE [App::DocumentObjectGroupPython] G4_GLYCEROL  # scripted group (container) (typed FeaturePython)
  Dunit = g/cm3
  Dvalue = 1.2613
  Group = -> [C_element050,H_element043,O_element047]
  conduct = 2
  density = 1
  expand = 3
  formula = G4_GLYCEROL
  name = G4_GLYCEROL
  specific = 4
FEATURE [App::DocumentObjectGroupPython] C_element051  label="C_element : 028"  # scripted group (container) (typed FeaturePython)
  n = 5
  ref = C_element
FEATURE [App::DocumentObjectGroupPython] H_element044  label="H_element : 023"  # scripted group (container) (typed FeaturePython)
  n = 5
  ref = H_element
FEATURE [App::DocumentObjectGroupPython] N_element020  label="N_element : 009"  # scripted group (container) (typed FeaturePython)
  n = 5
  ref = N_element
FEATURE [App::DocumentObjectGroupPython] O_element048  label="O_element : 024"  # scripted group (container) (typed FeaturePython)
  n = 1
  ref = O_element
FEATURE [App::DocumentObjectGroupPython] G4_GUANINE  # scripted group (container) (typed FeaturePython)
  Dunit = g/cm3
  Dvalue = 2.2
  Group = -> [C_element051,H_element044,N_element020,O_element048]
  conduct = 2
  density = 1
  expand = 3
  formula = G4_GUANINE
  name = G4_GUANINE
  specific = 4
FEATURE [App::DocumentObjectGroupPython] Ca_element012  label="Ca_element : 006"  # scripted group (container) (typed FeaturePython)
  n = 1
  ref = Ca_element
FEATURE [App::DocumentObjectGroupPython] S_element014  label="S_element : 005"  # scripted group (container) (typed FeaturePython)
  n = 1
  ref = S_element
FEATURE [App::DocumentObjectGroupPython] O_element049  label="O_element : 6"  # scripted group (container) (typed FeaturePython)
  n = 6
  ref = O_element
FEATURE [App::DocumentObjectGroupPython] H_element045  label="H_element : 024"  # scripted group (container) (typed FeaturePython)
  n = 4
  ref = H_element
FEATURE [App::DocumentObjectGroupPython] G4_GYPSUM  # scripted group (container) (typed FeaturePython)
  Dunit = g/cm3
  Dvalue = 2.32
  Group = -> [Ca_element012,S_element014,O_element049,H_element045]
  conduct = 2
  density = 1
  expand = 3
  formula = G4_GYPSUM
  name = G4_GYPSUM
  specific = 4
FEATURE [App::DocumentObjectGroupPython] C_element052  label="C_element : 7"  # scripted group (container) (typed FeaturePython)
  n = 7
  ref = C_element
FEATURE [App::DocumentObjectGroupPython] H_element046  label="H_element : 16"  # scripted group (container) (typed FeaturePython)
  n = 16
  ref = H_element
FEATURE [App::DocumentObjectGroupPython] G4_N_HEPTANE  label="G4_N-HEPTANE"  # scripted group (container) (typed FeaturePython)
  Dunit = g/cm3
  Dvalue = 0.68376
  Group = -> [C_element052,H_element046]
  conduct = 2
  density = 1
  expand = 3
  formula = G4_N-HEPTANE
  name = G4_N-HEPTANE
  specific = 4
FEATURE [App::DocumentObjectGroupPython] C_element053  label="C_element : 029"  # scripted group (container) (typed FeaturePython)
  n = 6
  ref = C_element
FEATURE [App::DocumentObjectGroupPython] H_element047  label="H_element : 14"  # scripted group (container) (typed FeaturePython)
  n = 14
  ref = H_element
FEATURE [App::DocumentObjectGroupPython] G4_N_HEXANE  label="G4_N-HEXANE"  # scripted group (container) (typed FeaturePython)
  Dunit = g/cm3
  Dvalue = 0.6603
  Group = -> [C_element053,H_element047]
  conduct = 2
  density = 1
  expand = 3
  formula = G4_N-HEXANE
  name = G4_N-HEXANE
  specific = 4
FEATURE [App::DocumentObjectGroupPython] C_element054  label="C_element : 22"  # scripted group (container) (typed FeaturePython)
  n = 22
  ref = C_element
FEATURE [App::DocumentObjectGroupPython] H_element048  label="H_element : 025"  # scripted group (container) (typed FeaturePython)
  n = 10
  ref = H_element
FEATURE [App::DocumentObjectGroupPython] N_element021  label="N_element : 010"  # scripted group (container) (typed FeaturePython)
  n = 2
  ref = N_element
FEATURE [App::DocumentObjectGroupPython] O_element050  label="O_element : 025"  # scripted group (container) (typed FeaturePython)
  n = 5
  ref = O_element
FEATURE [App::DocumentObjectGroupPython] G4_KAPTON  # scripted group (container) (typed FeaturePython)
  Dunit = g/cm3
  Dvalue = 1.42
  Group = -> [C_element054,H_element048,N_element021,O_element050]
  conduct = 2
  density = 1
  expand = 3
  formula = G4_KAPTON
  name = G4_KAPTON
  specific = 4
FEATURE [App::DocumentObjectGroupPython] La_element001  label="La_element : 1"  # scripted group (container) (typed FeaturePython)
  n = 1
  ref = La_element
FEATURE [App::DocumentObjectGroupPython] Br_element003  label="Br_element : 002"  # scripted group (container) (typed FeaturePython)
  n = 1
  ref = Br_element
FEATURE [App::DocumentObjectGroupPython] O_element051  label="O_element : 026"  # scripted group (container) (typed FeaturePython)
  n = 1
  ref = O_element
FEATURE [App::DocumentObjectGroupPython] G4_LANTHANUM_OXYBROMIDE  # scripted group (container) (typed FeaturePython)
  Dunit = g/cm3
  Dvalue = 6.28
  Group = -> [La_element001,Br_element003,O_element051]
  conduct = 2
  density = 1
  expand = 3
  formula = G4_LANTHANUM_OXYBROMIDE
  name = G4_LANTHANUM_OXYBROMIDE
  specific = 4
FEATURE [App::DocumentObjectGroupPython] La_element002  label="La_element : 2"  # scripted group (container) (typed FeaturePython)
  n = 2
  ref = La_element
FEATURE [App::DocumentObjectGroupPython] O_element052  label="O_element : 027"  # scripted group (container) (typed FeaturePython)
  n = 2
  ref = O_element
FEATURE [App::DocumentObjectGroupPython] S_element015  label="S_element : 006"  # scripted group (container) (typed FeaturePython)
  n = 1
  ref = S_element
FEATURE [App::DocumentObjectGroupPython] G4_LANTHANUM_OXYSULFIDE  # scripted group (container) (typed FeaturePython)
  Dunit = g/cm3
  Dvalue = 5.86
  Group = -> [La_element002,O_element052,S_element015]
  conduct = 2
  density = 1
  expand = 3
  formula = G4_LANTHANUM_OXYSULFIDE
  name = G4_LANTHANUM_OXYSULFIDE
  specific = 4
FEATURE [App::DocumentObjectGroupPython] O_element053  label="O_element : 0.072"  # scripted group (container) (typed FeaturePython)
  n = 0.071682
FEATURE [App::DocumentObjectGroupPython] Pb_element002  label="Pb_element : 0.928"  # scripted group (container) (typed FeaturePython)
  n = 0.928318
FEATURE [App::DocumentObjectGroupPython] G4_LEAD_OXIDE  # scripted group (container) (typed FeaturePython)
  Dunit = g/cm3
  Dvalue = 9.53
  Group = -> [O_element053,Pb_element002]
  conduct = 2
  density = 1
  expand = 3
  formula = G4_LEAD_OXIDE
  name = G4_LEAD_OXIDE
  specific = 4
FEATURE [App::DocumentObjectGroupPython] Li_element001  label="Li_element : 1"  # scripted group (container) (typed FeaturePython)
  n = 1
  ref = Li_element
FEATURE [App::DocumentObjectGroupPython] N_element022  label="N_element : 011"  # scripted group (container) (typed FeaturePython)
  n = 1
  ref = N_element
FEATURE [App::DocumentObjectGroupPython] H_element049  label="H_element : 026"  # scripted group (container) (typed FeaturePython)
  n = 2
  ref = H_element
FEATURE [App::DocumentObjectGroupPython] G4_LITHIUM_AMIDE  # scripted group (container) (typed FeaturePython)
  Dunit = g/cm3
  Dvalue = 1.178
  Group = -> [Li_element001,N_element022,H_element049]
  conduct = 2
  density = 1
  expand = 3
  formula = G4_LITHIUM_AMIDE
  name = G4_LITHIUM_AMIDE
  specific = 4
FEATURE [App::DocumentObjectGroupPython] Li_element002  label="Li_element : 2"  # scripted group (container) (typed FeaturePython)
  n = 2
  ref = Li_element
FEATURE [App::DocumentObjectGroupPython] C_element055  label="C_element : 030"  # scripted group (container) (typed FeaturePython)
  n = 1
  ref = C_element
FEATURE [App::DocumentObjectGroupPython] O_element054  label="O_element : 028"  # scripted group (container) (typed FeaturePython)
  n = 3
  ref = O_element
FEATURE [App::DocumentObjectGroupPython] G4_LITHIUM_CARBONATE  # scripted group (container) (typed FeaturePython)
  Dunit = g/cm3
  Dvalue = 2.11
  Group = -> [Li_element002,C_element055,O_element054]
  conduct = 2
  density = 1
  expand = 3
  formula = G4_LITHIUM_CARBONATE
  name = G4_LITHIUM_CARBONATE
  specific = 4
FEATURE [App::DocumentObjectGroupPython] Li_element003  label="Li_element : 003"  # scripted group (container) (typed FeaturePython)
  n = 1
  ref = Li_element
FEATURE [App::DocumentObjectGroupPython] F_element012  label="F_element : 004"  # scripted group (container) (typed FeaturePython)
  n = 1
  ref = F_element
FEATURE [App::DocumentObjectGroupPython] G4_LITHIUM_FLUORIDE  # scripted group (container) (typed FeaturePython)
  Dunit = g/cm3
  Dvalue = 2.635
  Group = -> [Li_element003,F_element012]
  conduct = 2
  density = 1
  expand = 3
  formula = G4_LITHIUM_FLUORIDE
  name = G4_LITHIUM_FLUORIDE
  specific = 4
FEATURE [App::DocumentObjectGroupPython] Li_element004  label="Li_element : 004"  # scripted group (container) (typed FeaturePython)
  n = 1
  ref = Li_element
FEATURE [App::DocumentObjectGroupPython] H_element050  label="H_element : 027"  # scripted group (container) (typed FeaturePython)
  n = 1
  ref = H_element
FEATURE [App::DocumentObjectGroupPython] G4_LITHIUM_HYDRIDE  # scripted group (container) (typed FeaturePython)
  Dunit = g/cm3
  Dvalue = 0.82
  Group = -> [Li_element004,H_element050]
  conduct = 2
  density = 1
  expand = 3
  formula = G4_LITHIUM_HYDRIDE
  name = G4_LITHIUM_HYDRIDE
  specific = 4
FEATURE [App::DocumentObjectGroupPython] Li_element005  label="Li_element : 005"  # scripted group (container) (typed FeaturePython)
  n = 1
  ref = Li_element
FEATURE [App::DocumentObjectGroupPython] I_element003  label="I_element : 002"  # scripted group (container) (typed FeaturePython)
  n = 1
  ref = I_element
FEATURE [App::DocumentObjectGroupPython] G4_LITHIUM_IODIDE  # scripted group (container) (typed FeaturePython)
  Dunit = g/cm3
  Dvalue = 3.494
  Group = -> [Li_element005,I_element003]
  conduct = 2
  density = 1
  expand = 3
  formula = G4_LITHIUM_IODIDE
  name = G4_LITHIUM_IODIDE
  specific = 4
FEATURE [App::DocumentObjectGroupPython] Li_element006  label="Li_element : 006"  # scripted group (container) (typed FeaturePython)
  n = 2
  ref = Li_element
FEATURE [App::DocumentObjectGroupPython] O_element055  label="O_element : 029"  # scripted group (container) (typed FeaturePython)
  n = 1
  ref = O_element
FEATURE [App::DocumentObjectGroupPython] G4_LITHIUM_OXIDE  # scripted group (container) (typed FeaturePython)
  Dunit = g/cm3
  Dvalue = 2.013
  Group = -> [Li_element006,O_element055]
  conduct = 2
  density = 1
  expand = 3
  formula = G4_LITHIUM_OXIDE
  name = G4_LITHIUM_OXIDE
  specific = 4
FEATURE [App::DocumentObjectGroupPython] Li_element007  label="Li_element : 007"  # scripted group (container) (typed FeaturePython)
  n = 2
  ref = Li_element
FEATURE [App::DocumentObjectGroupPython] B_element005  label="B_element : 005"  # scripted group (container) (typed FeaturePython)
  n = 4
  ref = B_element
FEATURE [App::DocumentObjectGroupPython] O_element056  label="O_element : 7"  # scripted group (container) (typed FeaturePython)
  n = 7
  ref = O_element
FEATURE [App::DocumentObjectGroupPython] G4_LITHIUM_TETRABORATE  # scripted group (container) (typed FeaturePython)
  Dunit = g/cm3
  Dvalue = 2.44
  Group = -> [Li_element007,B_element005,O_element056]
  conduct = 2
  density = 1
  expand = 3
  formula = G4_LITHIUM_TETRABORATE
  name = G4_LITHIUM_TETRABORATE
  specific = 4
FEATURE [App::DocumentObjectGroupPython] H_element051  label="H_element : 0.105"  # scripted group (container) (typed FeaturePython)
  n = 0.105
FEATURE [App::DocumentObjectGroupPython] C_element056  label="C_element : 0.083"  # scripted group (container) (typed FeaturePython)
  n = 0.083
FEATURE [App::DocumentObjectGroupPython] N_element023  label="N_element : 0.023"  # scripted group (container) (typed FeaturePython)
  n = 0.023
FEATURE [App::DocumentObjectGroupPython] O_element057  label="O_element : 0.779"  # scripted group (container) (typed FeaturePython)
  n = 0.779
FEATURE [App::DocumentObjectGroupPython] Na_element010  label="Na_element : 0.097"  # scripted group (container) (typed FeaturePython)
  n = 0.002
FEATURE [App::DocumentObjectGroupPython] P_element006  label="P_element : 0.105"  # scripted group (container) (typed FeaturePython)
  n = 0.001
FEATURE [App::DocumentObjectGroupPython] S_element016  label="S_element : 0.017"  # scripted group (container) (typed FeaturePython)
  n = 0.002
FEATURE [App::DocumentObjectGroupPython] Cl_element014  label="Cl_element : 0.587"  # scripted group (container) (typed FeaturePython)
  n = 0.003
FEATURE [App::DocumentObjectGroupPython] K_element005  label="K_element : 0.015"  # scripted group (container) (typed FeaturePython)
  n = 0.002
FEATURE [App::DocumentObjectGroupPython] G4_LUNG_ICRP  # scripted group (container) (typed FeaturePython)
  Dunit = g/cm3
  Dvalue = 1.04
  Group = -> [H_element051,C_element056,N_element023,O_element057,Na_element010,P_element006,S_element016,Cl_element014,K_element005]
  conduct = 2
  density = 1
  expand = 3
  formula = G4_LUNG_ICRP
  name = G4_LUNG_ICRP
  specific = 4
FEATURE [App::DocumentObjectGroupPython] H_element052  label="H_element : 0.116"  # scripted group (container) (typed FeaturePython)
  n = 0.114318
FEATURE [App::DocumentObjectGroupPython] C_element057  label="C_element : 0.656"  # scripted group (container) (typed FeaturePython)
  n = 0.655824
FEATURE [App::DocumentObjectGroupPython] O_element058  label="O_element : 0.092"  # scripted group (container) (typed FeaturePython)
  n = 0.0921831
FEATURE [App::DocumentObjectGroupPython] Mg_element004  label="Mg_element : 0.135"  # scripted group (container) (typed FeaturePython)
  n = 0.134792
FEATURE [App::DocumentObjectGroupPython] Ca_element013  label="Ca_element : 0.003"  # scripted group (container) (typed FeaturePython)
  n = 0.002883
FEATURE [App::DocumentObjectGroupPython] G4_M3_WAX  # scripted group (container) (typed FeaturePython)
  Dunit = g/cm3
  Dvalue = 1.05
  Group = -> [H_element052,C_element057,O_element058,Mg_element004,Ca_element013]
  conduct = 2
  density = 1
  expand = 3
  formula = G4_M3_WAX
  name = G4_M3_WAX
  specific = 4
FEATURE [App::DocumentObjectGroupPython] Mg_element005  label="Mg_element : 1"  # scripted group (container) (typed FeaturePython)
  n = 1
  ref = Mg_element
FEATURE [App::DocumentObjectGroupPython] C_element058  label="C_element : 031"  # scripted group (container) (typed FeaturePython)
  n = 1
  ref = C_element
FEATURE [App::DocumentObjectGroupPython] O_element059  label="O_element : 030"  # scripted group (container) (typed FeaturePython)
  n = 3
  ref = O_element
FEATURE [App::DocumentObjectGroupPython] G4_MAGNESIUM_CARBONATE  # scripted group (container) (typed FeaturePython)
  Dunit = g/cm3
  Dvalue = 2.958
  Group = -> [Mg_element005,C_element058,O_element059]
  conduct = 2
  density = 1
  expand = 3
  formula = G4_MAGNESIUM_CARBONATE
  name = G4_MAGNESIUM_CARBONATE
  specific = 4
FEATURE [App::DocumentObjectGroupPython] Mg_element006  label="Mg_element : 002"  # scripted group (container) (typed FeaturePython)
  n = 1
  ref = Mg_element
FEATURE [App::DocumentObjectGroupPython] F_element013  label="F_element : 005"  # scripted group (container) (typed FeaturePython)
  n = 2
  ref = F_element
FEATURE [App::DocumentObjectGroupPython] G4_MAGNESIUM_FLUORIDE  # scripted group (container) (typed FeaturePython)
  Dunit = g/cm3
  Dvalue = 3
  Group = -> [Mg_element006,F_element013]
  conduct = 2
  density = 1
  expand = 3
  formula = G4_MAGNESIUM_FLUORIDE
  name = G4_MAGNESIUM_FLUORIDE
  specific = 4
FEATURE [App::DocumentObjectGroupPython] Mg_element007  label="Mg_element : 003"  # scripted group (container) (typed FeaturePython)
  n = 1
  ref = Mg_element
FEATURE [App::DocumentObjectGroupPython] O_element060  label="O_element : 031"  # scripted group (container) (typed FeaturePython)
  n = 1
  ref = O_element
FEATURE [App::DocumentObjectGroupPython] G4_MAGNESIUM_OXIDE  # scripted group (container) (typed FeaturePython)
  Dunit = g/cm3
  Dvalue = 3.58
  Group = -> [Mg_element007,O_element060]
  conduct = 2
  density = 1
  expand = 3
  formula = G4_MAGNESIUM_OXIDE
  name = G4_MAGNESIUM_OXIDE
  specific = 4
FEATURE [App::DocumentObjectGroupPython] Mg_element008  label="Mg_element : 004"  # scripted group (container) (typed FeaturePython)
  n = 1
  ref = Mg_element
FEATURE [App::DocumentObjectGroupPython] B_element006  label="B_element : 006"  # scripted group (container) (typed FeaturePython)
  n = 4
  ref = B_element
FEATURE [App::DocumentObjectGroupPython] O_element061  label="O_element : 032"  # scripted group (container) (typed FeaturePython)
  n = 7
  ref = O_element
FEATURE [App::DocumentObjectGroupPython] G4_MAGNESIUM_TETRABORATE  # scripted group (container) (typed FeaturePython)
  Dunit = g/cm3
  Dvalue = 2.53
  Group = -> [Mg_element008,B_element006,O_element061]
  conduct = 2
  density = 1
  expand = 3
  formula = G4_MAGNESIUM_TETRABORATE
  name = G4_MAGNESIUM_TETRABORATE
  specific = 4
FEATURE [App::DocumentObjectGroupPython] Hg_element001  label="Hg_element : 1"  # scripted group (container) (typed FeaturePython)
  n = 1
  ref = Hg_element
FEATURE [App::DocumentObjectGroupPython] I_element004  label="I_element : 2"  # scripted group (container) (typed FeaturePython)
  n = 2
  ref = I_element
FEATURE [App::DocumentObjectGroupPython] G4_MERCURIC_IODIDE  # scripted group (container) (typed FeaturePython)
  Dunit = g/cm3
  Dvalue = 6.36
  Group = -> [Hg_element001,I_element004]
  conduct = 2
  density = 1
  expand = 3
  formula = G4_MERCURIC_IODIDE
  name = G4_MERCURIC_IODIDE
  specific = 4
FEATURE [App::DocumentObjectGroupPython] C_element059  label="C_element : 032"  # scripted group (container) (typed FeaturePython)
  n = 1
  ref = C_element
FEATURE [App::DocumentObjectGroupPython] H_element053  label="H_element : 028"  # scripted group (container) (typed FeaturePython)
  n = 4
  ref = H_element
FEATURE [App::DocumentObjectGroupPython] G4_METHANE  # scripted group (container) (typed FeaturePython)
  Dunit = g/cm3
  Dvalue = 0.000667151
  Group = -> [C_element059,H_element053]
  conduct = 2
  density = 1
  expand = 3
  formula = G4_METHANE
  name = G4_METHANE
  specific = 4
FEATURE [App::DocumentObjectGroupPython] C_element060  label="C_element : 033"  # scripted group (container) (typed FeaturePython)
  n = 1
  ref = C_element
FEATURE [App::DocumentObjectGroupPython] H_element054  label="H_element : 029"  # scripted group (container) (typed FeaturePython)
  n = 4
  ref = H_element
FEATURE [App::DocumentObjectGroupPython] O_element062  label="O_element : 033"  # scripted group (container) (typed FeaturePython)
  n = 1
  ref = O_element
FEATURE [App::DocumentObjectGroupPython] G4_METHANOL  # scripted group (container) (typed FeaturePython)
  Dunit = g/cm3
  Dvalue = 0.7914
  Group = -> [C_element060,H_element054,O_element062]
  conduct = 2
  density = 1
  expand = 3
  formula = G4_METHANOL
  name = G4_METHANOL
  specific = 4
FEATURE [App::DocumentObjectGroupPython] H_element055  label="H_element : 0.134"  # scripted group (container) (typed FeaturePython)
  n = 0.13404
FEATURE [App::DocumentObjectGroupPython] C_element061  label="C_element : 0.778"  # scripted group (container) (typed FeaturePython)
  n = 0.77796
FEATURE [App::DocumentObjectGroupPython] O_element063  label="O_element : 0.035"  # scripted group (container) (typed FeaturePython)
  n = 0.03502
FEATURE [App::DocumentObjectGroupPython] Mg_element009  label="Mg_element : 0.039"  # scripted group (container) (typed FeaturePython)
  n = 0.038594
FEATURE [App::DocumentObjectGroupPython] Ti_element002  label="Ti_element : 0.014"  # scripted group (container) (typed FeaturePython)
  n = 0.014386
FEATURE [App::DocumentObjectGroupPython] G4_MIX_D_WAX  # scripted group (container) (typed FeaturePython)
  Dunit = g/cm3
  Dvalue = 0.99
  Group = -> [H_element055,C_element061,O_element063,Mg_element009,Ti_element002]
  conduct = 2
  density = 1
  expand = 3
  formula = G4_MIX_D_WAX
  name = G4_MIX_D_WAX
  specific = 4
FEATURE [App::DocumentObjectGroupPython] H_element056  label="H_element : 0.135"  # scripted group (container) (typed FeaturePython)
  n = 0.081192
FEATURE [App::DocumentObjectGroupPython] C_element062  label="C_element : 0.583"  # scripted group (container) (typed FeaturePython)
  n = 0.583442
FEATURE [App::DocumentObjectGroupPython] N_element024  label="N_element : 0.018"  # scripted group (container) (typed FeaturePython)
  n = 0.017798
FEATURE [App::DocumentObjectGroupPython] O_element064  label="O_element : 0.186"  # scripted group (container) (typed FeaturePython)
  n = 0.186381
FEATURE [App::DocumentObjectGroupPython] Mg_element010  label="Mg_element : 0.130"  # scripted group (container) (typed FeaturePython)
  n = 0.130287
FEATURE [App::DocumentObjectGroupPython] Cl_element015  label="Cl_element : 0.588"  # scripted group (container) (typed FeaturePython)
  n = 0.0009
FEATURE [App::DocumentObjectGroupPython] G4_MS20_TISSUE  # scripted group (container) (typed FeaturePython)
  Dunit = g/cm3
  Dvalue = 1
  Group = -> [H_element056,C_element062,N_element024,O_element064,Mg_element010,Cl_element015]
  conduct = 2
  density = 1
  expand = 3
  formula = G4_MS20_TISSUE
  name = G4_MS20_TISSUE
  specific = 4
FEATURE [App::DocumentObjectGroupPython] H_element057  label="H_element : 0.136"  # scripted group (container) (typed FeaturePython)
  n = 0.102
FEATURE [App::DocumentObjectGroupPython] C_element063  label="C_element : 0.143"  # scripted group (container) (typed FeaturePython)
  n = 0.143
FEATURE [App::DocumentObjectGroupPython] N_element025  label="N_element : 0.034"  # scripted group (container) (typed FeaturePython)
  n = 0.034
FEATURE [App::DocumentObjectGroupPython] O_element065  label="O_element : 0.710"  # scripted group (container) (typed FeaturePython)
  n = 0.71
FEATURE [App::DocumentObjectGroupPython] Na_element011  label="Na_element : 0.098"  # scripted group (container) (typed FeaturePython)
  n = 0.001
FEATURE [App::DocumentObjectGroupPython] P_element007  label="P_element : 0.002"  # scripted group (container) (typed FeaturePython)
  n = 0.002
FEATURE [App::DocumentObjectGroupPython] S_element017  label="S_element : 0.018"  # scripted group (container) (typed FeaturePython)
  n = 0.003
FEATURE [App::DocumentObjectGroupPython] Cl_element016  label="Cl_element : 0.589"  # scripted group (container) (typed FeaturePython)
  n = 0.001
FEATURE [App::DocumentObjectGroupPython] K_element006  label="K_element : 0.004"  # scripted group (container) (typed FeaturePython)
  n = 0.004
FEATURE [App::DocumentObjectGroupPython] G4_MUSCLE_SKELETAL_ICRP  # scripted group (container) (typed FeaturePython)
  Dunit = g/cm3
  Dvalue = 1.05
  Group = -> [H_element057,C_element063,N_element025,O_element065,Na_element011,P_element007,S_element017,Cl_element016,K_element006]
  conduct = 2
  density = 1
  expand = 3
  formula = G4_MUSCLE_SKELETAL_ICRP
  name = G4_MUSCLE_SKELETAL_ICRP
  specific = 4
FEATURE [App::DocumentObjectGroupPython] H_element058  label="H_element : 0.137"  # scripted group (container) (typed FeaturePython)
  n = 0.102102
FEATURE [App::DocumentObjectGroupPython] C_element064  label="C_element : 0.123"  # scripted group (container) (typed FeaturePython)
  n = 0.123123
FEATURE [App::DocumentObjectGroupPython] N_element026  label="N_element : 0.756"  # scripted group (container) (typed FeaturePython)
  n = 0.035035
FEATURE [App::DocumentObjectGroupPython] O_element066  label="O_element : 0.730"  # scripted group (container) (typed FeaturePython)
  n = 0.72973
FEATURE [App::DocumentObjectGroupPython] Na_element012  label="Na_element : 0.099"  # scripted group (container) (typed FeaturePython)
  n = 0.001001
FEATURE [App::DocumentObjectGroupPython] P_element008  label="P_element : 0.106"  # scripted group (container) (typed FeaturePython)
  n = 0.002002
FEATURE [App::DocumentObjectGroupPython] S_element018  label="S_element : 0.019"  # scripted group (container) (typed FeaturePython)
  n = 0.004004
FEATURE [App::DocumentObjectGroupPython] K_element007  label="K_element : 0.016"  # scripted group (container) (typed FeaturePython)
  n = 0.003003
FEATURE [App::DocumentObjectGroupPython] G4_MUSCLE_STRIATED_ICRU  # scripted group (container) (typed FeaturePython)
  Dunit = g/cm3
  Dvalue = 1.04
  Group = -> [H_element058,C_element064,N_element026,O_element066,Na_element012,P_element008,S_element018,K_element007]
  conduct = 2
  density = 1
  expand = 3
  formula = G4_MUSCLE_STRIATED_ICRU
  name = G4_MUSCLE_STRIATED_ICRU
  specific = 4
FEATURE [App::DocumentObjectGroupPython] H_element059  label="H_element : 0.098"  # scripted group (container) (typed FeaturePython)
  n = 0.0982341
FEATURE [App::DocumentObjectGroupPython] C_element065  label="C_element : 0.156"  # scripted group (container) (typed FeaturePython)
  n = 0.156214
FEATURE [App::DocumentObjectGroupPython] N_element027  label="N_element : 0.757"  # scripted group (container) (typed FeaturePython)
  n = 0.035451
FEATURE [App::DocumentObjectGroupPython] O_element067  label="O_element : 0.880"  # scripted group (container) (typed FeaturePython)
  n = 0.710101
FEATURE [App::DocumentObjectGroupPython] G4_MUSCLE_WITH_SUCROSE  # scripted group (container) (typed FeaturePython)
  Dunit = g/cm3
  Dvalue = 1.11
  Group = -> [H_element059,C_element065,N_element027,O_element067]
  conduct = 2
  density = 1
  expand = 3
  formula = G4_MUSCLE_WITH_SUCROSE
  name = G4_MUSCLE_WITH_SUCROSE
  specific = 4
FEATURE [App::DocumentObjectGroupPython] H_element060  label="H_element : 0.138"  # scripted group (container) (typed FeaturePython)
  n = 0.101969
FEATURE [App::DocumentObjectGroupPython] C_element066  label="C_element : 0.120"  # scripted group (container) (typed FeaturePython)
  n = 0.120058
FEATURE [App::DocumentObjectGroupPython] N_element028  label="N_element : 0.758"  # scripted group (container) (typed FeaturePython)
  n = 0.035451
FEATURE [App::DocumentObjectGroupPython] O_element068  label="O_element : 0.743"  # scripted group (container) (typed FeaturePython)
  n = 0.742522
FEATURE [App::DocumentObjectGroupPython] G4_MUSCLE_WITHOUT_SUCROSE  # scripted group (container) (typed FeaturePython)
  Dunit = g/cm3
  Dvalue = 1.07
  Group = -> [H_element060,C_element066,N_element028,O_element068]
  conduct = 2
  density = 1
  expand = 3
  formula = G4_MUSCLE_WITHOUT_SUCROSE
  name = G4_MUSCLE_WITHOUT_SUCROSE
  specific = 4
FEATURE [App::DocumentObjectGroupPython] C_element067  label="C_element : 10"  # scripted group (container) (typed FeaturePython)
  n = 10
  ref = C_element
FEATURE [App::DocumentObjectGroupPython] H_element061  label="H_element : 030"  # scripted group (container) (typed FeaturePython)
  n = 8
  ref = H_element
FEATURE [App::DocumentObjectGroupPython] G4_NAPHTHALENE  # scripted group (container) (typed FeaturePython)
  Dunit = g/cm3
  Dvalue = 1.145
  Group = -> [C_element067,H_element061]
  conduct = 2
  density = 1
  expand = 3
  formula = G4_NAPHTHALENE
  name = G4_NAPHTHALENE
  specific = 4
FEATURE [App::DocumentObjectGroupPython] C_element068  label="C_element : 034"  # scripted group (container) (typed FeaturePython)
  n = 6
  ref = C_element
FEATURE [App::DocumentObjectGroupPython] H_element062  label="H_element : 031"  # scripted group (container) (typed FeaturePython)
  n = 5
  ref = H_element
FEATURE [App::DocumentObjectGroupPython] N_element029  label="N_element : 012"  # scripted group (container) (typed FeaturePython)
  n = 1
  ref = N_element
FEATURE [App::DocumentObjectGroupPython] O_element069  label="O_element : 034"  # scripted group (container) (typed FeaturePython)
  n = 2
  ref = O_element
FEATURE [App::DocumentObjectGroupPython] G4_NITROBENZENE  # scripted group (container) (typed FeaturePython)
  Dunit = g/cm3
  Dvalue = 1.19867
  Group = -> [C_element068,H_element062,N_element029,O_element069]
  conduct = 2
  density = 1
  expand = 3
  formula = G4_NITROBENZENE
  name = G4_NITROBENZENE
  specific = 4
FEATURE [App::DocumentObjectGroupPython] N_element030  label="N_element : 013"  # scripted group (container) (typed FeaturePython)
  n = 2
  ref = N_element
FEATURE [App::DocumentObjectGroupPython] O_element070  label="O_element : 035"  # scripted group (container) (typed FeaturePython)
  n = 1
  ref = O_element
FEATURE [App::DocumentObjectGroupPython] G4_NITROUS_OXIDE  # scripted group (container) (typed FeaturePython)
  Dunit = g/cm3
  Dvalue = 0.00183094
  Group = -> [N_element030,O_element070]
  conduct = 2
  density = 1
  expand = 3
  formula = G4_NITROUS_OXIDE
  name = G4_NITROUS_OXIDE
  specific = 4
FEATURE [App::DocumentObjectGroupPython] H_element063  label="H_element : 0.104"  # scripted group (container) (typed FeaturePython)
  n = 0.103509
FEATURE [App::DocumentObjectGroupPython] C_element069  label="C_element : 0.648"  # scripted group (container) (typed FeaturePython)
  n = 0.648416
FEATURE [App::DocumentObjectGroupPython] N_element031  label="N_element : 0.100"  # scripted group (container) (typed FeaturePython)
  n = 0.0995361
FEATURE [App::DocumentObjectGroupPython] O_element071  label="O_element : 0.149"  # scripted group (container) (typed FeaturePython)
  n = 0.148539
FEATURE [App::DocumentObjectGroupPython] G4_NYLON_8062  label="G4_NYLON-8062"  # scripted group (container) (typed FeaturePython)
  Dunit = g/cm3
  Dvalue = 1.08
  Group = -> [H_element063,C_element069,N_element031,O_element071]
  conduct = 2
  density = 1
  expand = 3
  formula = G4_NYLON-8062
  name = G4_NYLON-8062
  specific = 4
FEATURE [App::DocumentObjectGroupPython] C_element070  label="C_element : 035"  # scripted group (container) (typed FeaturePython)
  n = 6
  ref = C_element
FEATURE [App::DocumentObjectGroupPython] H_element064  label="H_element : 11"  # scripted group (container) (typed FeaturePython)
  n = 11
  ref = H_element
FEATURE [App::DocumentObjectGroupPython] N_element032  label="N_element : 014"  # scripted group (container) (typed FeaturePython)
  n = 1
  ref = N_element
FEATURE [App::DocumentObjectGroupPython] O_element072  label="O_element : 036"  # scripted group (container) (typed FeaturePython)
  n = 1
  ref = O_element
FEATURE [App::DocumentObjectGroupPython] G4_NYLON_6_6  label="G4_NYLON-6-6"  # scripted group (container) (typed FeaturePython)
  Dunit = g/cm3
  Dvalue = 1.14
  Group = -> [C_element070,H_element064,N_element032,O_element072]
  conduct = 2
  density = 1
  expand = 3
  formula = G4_NYLON-6-6
  name = G4_NYLON-6-6
  specific = 4
FEATURE [App::DocumentObjectGroupPython] H_element065  label="H_element : 0.139"  # scripted group (container) (typed FeaturePython)
  n = 0.107062
FEATURE [App::DocumentObjectGroupPython] C_element071  label="C_element : 0.680"  # scripted group (container) (typed FeaturePython)
  n = 0.680449
FEATURE [App::DocumentObjectGroupPython] N_element033  label="N_element : 0.099"  # scripted group (container) (typed FeaturePython)
  n = 0.099189
FEATURE [App::DocumentObjectGroupPython] O_element073  label="O_element : 0.113"  # scripted group (container) (typed FeaturePython)
  n = 0.1133
FEATURE [App::DocumentObjectGroupPython] G4_NYLON_6_10  label="G4_NYLON-6-10"  # scripted group (container) (typed FeaturePython)
  Dunit = g/cm3
  Dvalue = 1.14
  Group = -> [H_element065,C_element071,N_element033,O_element073]
  conduct = 2
  density = 1
  expand = 3
  formula = G4_NYLON-6-10
  name = G4_NYLON-6-10
  specific = 4
FEATURE [App::DocumentObjectGroupPython] H_element066  label="H_element : 0.140"  # scripted group (container) (typed FeaturePython)
  n = 0.115476
FEATURE [App::DocumentObjectGroupPython] C_element072  label="C_element : 0.721"  # scripted group (container) (typed FeaturePython)
  n = 0.720818
FEATURE [App::DocumentObjectGroupPython] N_element034  label="N_element : 0.076"  # scripted group (container) (typed FeaturePython)
  n = 0.0764169
FEATURE [App::DocumentObjectGroupPython] O_element074  label="O_element : 0.087"  # scripted group (container) (typed FeaturePython)
  n = 0.0872889
FEATURE [App::DocumentObjectGroupPython] G4_NYLON_11_RILSAN  label="G4_NYLON-11_RILSAN"  # scripted group (container) (typed FeaturePython)
  Dunit = g/cm3
  Dvalue = 1.425
  Group = -> [H_element066,C_element072,N_element034,O_element074]
  conduct = 2
  density = 1
  expand = 3
  formula = G4_NYLON-11_RILSAN
  name = G4_NYLON-11_RILSAN
  specific = 4
FEATURE [App::DocumentObjectGroupPython] C_element073  label="C_element : 8"  # scripted group (container) (typed FeaturePython)
  n = 8
  ref = C_element
FEATURE [App::DocumentObjectGroupPython] H_element067  label="H_element : 18"  # scripted group (container) (typed FeaturePython)
  n = 18
  ref = H_element
FEATURE [App::DocumentObjectGroupPython] G4_OCTANE  # scripted group (container) (typed FeaturePython)
  Dunit = g/cm3
  Dvalue = 0.7026
  Group = -> [C_element073,H_element067]
  conduct = 2
  density = 1
  expand = 3
  formula = G4_OCTANE
  name = G4_OCTANE
  specific = 4
FEATURE [App::DocumentObjectGroupPython] C_element074  label="C_element : 25"  # scripted group (container) (typed FeaturePython)
  n = 25
  ref = C_element
FEATURE [App::DocumentObjectGroupPython] H_element068  label="H_element : 52"  # scripted group (container) (typed FeaturePython)
  n = 52
  ref = H_element
FEATURE [App::DocumentObjectGroupPython] G4_PARAFFIN  # scripted group (container) (typed FeaturePython)
  Dunit = g/cm3
  Dvalue = 0.93
  Group = -> [C_element074,H_element068]
  conduct = 2
  density = 1
  expand = 3
  formula = G4_PARAFFIN
  name = G4_PARAFFIN
  specific = 4
FEATURE [App::DocumentObjectGroupPython] C_element075  label="C_element : 036"  # scripted group (container) (typed FeaturePython)
  n = 5
  ref = C_element
FEATURE [App::DocumentObjectGroupPython] H_element069  label="H_element : 032"  # scripted group (container) (typed FeaturePython)
  n = 12
  ref = H_element
FEATURE [App::DocumentObjectGroupPython] G4_N_PENTANE  label="G4_N-PENTANE"  # scripted group (container) (typed FeaturePython)
  Dunit = g/cm3
  Dvalue = 0.6262
  Group = -> [C_element075,H_element069]
  conduct = 2
  density = 1
  expand = 3
  formula = G4_N-PENTANE
  name = G4_N-PENTANE
  specific = 4
FEATURE [App::DocumentObjectGroupPython] H_element070  label="H_element : 0.014"  # scripted group (container) (typed FeaturePython)
  n = 0.0141
FEATURE [App::DocumentObjectGroupPython] C_element076  label="C_element : 0.072"  # scripted group (container) (typed FeaturePython)
  n = 0.072261
FEATURE [App::DocumentObjectGroupPython] N_element035  label="N_element : 0.019"  # scripted group (container) (typed FeaturePython)
  n = 0.01932
FEATURE [App::DocumentObjectGroupPython] O_element075  label="O_element : 0.066"  # scripted group (container) (typed FeaturePython)
  n = 0.066101
FEATURE [App::DocumentObjectGroupPython] S_element019  label="S_element : 0.020"  # scripted group (container) (typed FeaturePython)
  n = 0.00189
FEATURE [App::DocumentObjectGroupPython] Br_element004  label="Br_element : 0.349"  # scripted group (container) (typed FeaturePython)
  n = 0.349103
FEATURE [App::DocumentObjectGroupPython] Ag_element001  label="Ag_element : 0.474"  # scripted group (container) (typed FeaturePython)
  n = 0.474105
FEATURE [App::DocumentObjectGroupPython] I_element005  label="I_element : 0.003"  # scripted group (container) (typed FeaturePython)
  n = 0.00312
FEATURE [App::DocumentObjectGroupPython] G4_PHOTO_EMULSION  # scripted group (container) (typed FeaturePython)
  Dunit = g/cm3
  Dvalue = 3.815
  Group = -> [H_element070,C_element076,N_element035,O_element075,S_element019,Br_element004,Ag_element001,I_element005]
  conduct = 2
  density = 1
  expand = 3
  formula = G4_PHOTO_EMULSION
  name = G4_PHOTO_EMULSION
  specific = 4
FEATURE [App::DocumentObjectGroupPython] C_element077  label="C_element : 9"  # scripted group (container) (typed FeaturePython)
  n = 9
  ref = C_element
FEATURE [App::DocumentObjectGroupPython] H_element071  label="H_element : 033"  # scripted group (container) (typed FeaturePython)
  n = 10
  ref = H_element
FEATURE [App::DocumentObjectGroupPython] G4_PLASTIC_SC_VINYLTOLUENE  # scripted group (container) (typed FeaturePython)
  Dunit = g/cm3
  Dvalue = 1.032
  Group = -> [C_element077,H_element071]
  conduct = 2
  density = 1
  expand = 3
  formula = G4_PLASTIC_SC_VINYLTOLUENE
  name = G4_PLASTIC_SC_VINYLTOLUENE
  specific = 4
FEATURE [App::DocumentObjectGroupPython] Pu_element001  label="Pu_element : 1"  # scripted group (container) (typed FeaturePython)
  n = 1
  ref = Pu_element
FEATURE [App::DocumentObjectGroupPython] O_element076  label="O_element : 037"  # scripted group (container) (typed FeaturePython)
  n = 2
  ref = O_element
FEATURE [App::DocumentObjectGroupPython] G4_PLUTONIUM_DIOXIDE  # scripted group (container) (typed FeaturePython)
  Dunit = g/cm3
  Dvalue = 11.46
  Group = -> [Pu_element001,O_element076]
  conduct = 2
  density = 1
  expand = 3
  formula = G4_PLUTONIUM_DIOXIDE
  name = G4_PLUTONIUM_DIOXIDE
  specific = 4
FEATURE [App::DocumentObjectGroupPython] C_element078  label="C_element : 037"  # scripted group (container) (typed FeaturePython)
  n = 3
  ref = C_element
FEATURE [App::DocumentObjectGroupPython] H_element072  label="H_element : 034"  # scripted group (container) (typed FeaturePython)
  n = 3
  ref = H_element
FEATURE [App::DocumentObjectGroupPython] N_element036  label="N_element : 015"  # scripted group (container) (typed FeaturePython)
  n = 1
  ref = N_element
FEATURE [App::DocumentObjectGroupPython] G4_POLYACRYLONITRILE  # scripted group (container) (typed FeaturePython)
  Dunit = g/cm3
  Dvalue = 1.17
  Group = -> [C_element078,H_element072,N_element036]
  conduct = 2
  density = 1
  expand = 3
  formula = G4_POLYACRYLONITRILE
  name = G4_POLYACRYLONITRILE
  specific = 4
FEATURE [App::DocumentObjectGroupPython] C_element079  label="C_element : 16"  # scripted group (container) (typed FeaturePython)
  n = 16
  ref = C_element
FEATURE [App::DocumentObjectGroupPython] H_element073  label="H_element : 035"  # scripted group (container) (typed FeaturePython)
  n = 14
  ref = H_element
FEATURE [App::DocumentObjectGroupPython] O_element077  label="O_element : 038"  # scripted group (container) (typed FeaturePython)
  n = 3
  ref = O_element
FEATURE [App::DocumentObjectGroupPython] G4_POLYCARBONATE  # scripted group (container) (typed FeaturePython)
  Dunit = g/cm3
  Dvalue = 1.2
  Group = -> [C_element079,H_element073,O_element077]
  conduct = 2
  density = 1
  expand = 3
  formula = G4_POLYCARBONATE
  name = G4_POLYCARBONATE
  specific = 4
FEATURE [App::DocumentObjectGroupPython] C_element080  label="C_element : 038"  # scripted group (container) (typed FeaturePython)
  n = 8
  ref = C_element
FEATURE [App::DocumentObjectGroupPython] H_element074  label="H_element : 036"  # scripted group (container) (typed FeaturePython)
  n = 7
  ref = H_element
FEATURE [App::DocumentObjectGroupPython] Cl_element017  label="Cl_element : 007"  # scripted group (container) (typed FeaturePython)
  n = 1
  ref = Cl_element
FEATURE [App::DocumentObjectGroupPython] G4_POLYCHLOROSTYRENE  # scripted group (container) (typed FeaturePython)
  Dunit = g/cm3
  Dvalue = 1.3
  Group = -> [C_element080,H_element074,Cl_element017]
  conduct = 2
  density = 1
  expand = 3
  formula = G4_POLYCHLOROSTYRENE
  name = G4_POLYCHLOROSTYRENE
  specific = 4
FEATURE [App::DocumentObjectGroupPython] C_element081  label="C_element : 039"  # scripted group (container) (typed FeaturePython)
  n = 1
  ref = C_element
FEATURE [App::DocumentObjectGroupPython] H_element075  label="H_element : 037"  # scripted group (container) (typed FeaturePython)
  n = 2
  ref = H_element
FEATURE [App::DocumentObjectGroupPython] G4_POLYETHYLENE  # scripted group (container) (typed FeaturePython)
  Dunit = g/cm3
  Dvalue = 0.94
  Group = -> [C_element081,H_element075]
  conduct = 2
  density = 1
  expand = 3
  formula = G4_POLYETHYLENE
  name = G4_POLYETHYLENE
  specific = 4
FEATURE [App::DocumentObjectGroupPython] C_element082  label="C_element : 040"  # scripted group (container) (typed FeaturePython)
  n = 10
  ref = C_element
FEATURE [App::DocumentObjectGroupPython] H_element076  label="H_element : 038"  # scripted group (container) (typed FeaturePython)
  n = 8
  ref = H_element
FEATURE [App::DocumentObjectGroupPython] O_element078  label="O_element : 039"  # scripted group (container) (typed FeaturePython)
  n = 4
  ref = O_element
FEATURE [App::DocumentObjectGroupPython] G4_MYLAR  # scripted group (container) (typed FeaturePython)
  Dunit = g/cm3
  Dvalue = 1.4
  Group = -> [C_element082,H_element076,O_element078]
  conduct = 2
  density = 1
  expand = 3
  formula = G4_MYLAR
  name = G4_MYLAR
  specific = 4
FEATURE [App::DocumentObjectGroupPython] C_element083  label="C_element : 041"  # scripted group (container) (typed FeaturePython)
  n = 5
  ref = C_element
FEATURE [App::DocumentObjectGroupPython] H_element077  label="H_element : 039"  # scripted group (container) (typed FeaturePython)
  n = 8
  ref = H_element
FEATURE [App::DocumentObjectGroupPython] O_element079  label="O_element : 040"  # scripted group (container) (typed FeaturePython)
  n = 2
  ref = O_element
FEATURE [App::DocumentObjectGroupPython] G4_PLEXIGLASS  # scripted group (container) (typed FeaturePython)
  Dunit = g/cm3
  Dvalue = 1.19
  Group = -> [C_element083,H_element077,O_element079]
  conduct = 2
  density = 1
  expand = 3
  formula = G4_PLEXIGLASS
  name = G4_PLEXIGLASS
  specific = 4
FEATURE [App::DocumentObjectGroupPython] C_element084  label="C_element : 042"  # scripted group (container) (typed FeaturePython)
  n = 1
  ref = C_element
FEATURE [App::DocumentObjectGroupPython] H_element078  label="H_element : 040"  # scripted group (container) (typed FeaturePython)
  n = 2
  ref = H_element
FEATURE [App::DocumentObjectGroupPython] O_element080  label="O_element : 041"  # scripted group (container) (typed FeaturePython)
  n = 1
  ref = O_element
FEATURE [App::DocumentObjectGroupPython] G4_POLYOXYMETHYLENE  # scripted group (container) (typed FeaturePython)
  Dunit = g/cm3
  Dvalue = 1.425
  Group = -> [C_element084,H_element078,O_element080]
  conduct = 2
  density = 1
  expand = 3
  formula = G4_POLYOXYMETHYLENE
  name = G4_POLYOXYMETHYLENE
  specific = 4
FEATURE [App::DocumentObjectGroupPython] C_element085  label="C_element : 043"  # scripted group (container) (typed FeaturePython)
  n = 2
  ref = C_element
FEATURE [App::DocumentObjectGroupPython] H_element079  label="H_element : 041"  # scripted group (container) (typed FeaturePython)
  n = 4
  ref = H_element
FEATURE [App::DocumentObjectGroupPython] G4_POLYPROPYLENE  # scripted group (container) (typed FeaturePython)
  Dunit = g/cm3
  Dvalue = 0.9
  Group = -> [C_element085,H_element079]
  conduct = 2
  density = 1
  expand = 3
  formula = G4_POLYPROPYLENE
  name = G4_POLYPROPYLENE
  specific = 4
FEATURE [App::DocumentObjectGroupPython] C_element086  label="C_element : 044"  # scripted group (container) (typed FeaturePython)
  n = 8
  ref = C_element
FEATURE [App::DocumentObjectGroupPython] H_element080  label="H_element : 042"  # scripted group (container) (typed FeaturePython)
  n = 8
  ref = H_element
FEATURE [App::DocumentObjectGroupPython] G4_POLYSTYRENE  # scripted group (container) (typed FeaturePython)
  Dunit = g/cm3
  Dvalue = 1.06
  Group = -> [C_element086,H_element080]
  conduct = 2
  density = 1
  expand = 3
  formula = G4_POLYSTYRENE
  name = G4_POLYSTYRENE
  specific = 4
FEATURE [App::DocumentObjectGroupPython] C_element087  label="C_element : 045"  # scripted group (container) (typed FeaturePython)
  n = 2
  ref = C_element
FEATURE [App::DocumentObjectGroupPython] F_element014  label="F_element : 4"  # scripted group (container) (typed FeaturePython)
  n = 4
  ref = F_element
FEATURE [App::DocumentObjectGroupPython] G4_TEFLON  # scripted group (container) (typed FeaturePython)
  Dunit = g/cm3
  Dvalue = 2.2
  Group = -> [C_element087,F_element014]
  conduct = 2
  density = 1
  expand = 3
  formula = G4_TEFLON
  name = G4_TEFLON
  specific = 4
FEATURE [App::DocumentObjectGroupPython] C_element088  label="C_element : 046"  # scripted group (container) (typed FeaturePython)
  n = 2
  ref = C_element
FEATURE [App::DocumentObjectGroupPython] F_element015  label="F_element : 006"  # scripted group (container) (typed FeaturePython)
  n = 3
  ref = F_element
FEATURE [App::DocumentObjectGroupPython] Cl_element018  label="Cl_element : 008"  # scripted group (container) (typed FeaturePython)
  n = 1
  ref = Cl_element
FEATURE [App::DocumentObjectGroupPython] G4_POLYTRIFLUOROCHLOROETHYLENE  # scripted group (container) (typed FeaturePython)
  Dunit = g/cm3
  Dvalue = 2.1
  Group = -> [C_element088,F_element015,Cl_element018]
  conduct = 2
  density = 1
  expand = 3
  formula = G4_POLYTRIFLUOROCHLOROETHYLENE
  name = G4_POLYTRIFLUOROCHLOROETHYLENE
  specific = 4
FEATURE [App::DocumentObjectGroupPython] C_element089  label="C_element : 047"  # scripted group (container) (typed FeaturePython)
  n = 4
  ref = C_element
FEATURE [App::DocumentObjectGroupPython] H_element081  label="H_element : 043"  # scripted group (container) (typed FeaturePython)
  n = 6
  ref = H_element
FEATURE [App::DocumentObjectGroupPython] O_element081  label="O_element : 042"  # scripted group (container) (typed FeaturePython)
  n = 2
  ref = O_element
FEATURE [App::DocumentObjectGroupPython] G4_POLYVINYL_ACETATE  # scripted group (container) (typed FeaturePython)
  Dunit = g/cm3
  Dvalue = 1.19
  Group = -> [C_element089,H_element081,O_element081]
  conduct = 2
  density = 1
  expand = 3
  formula = G4_POLYVINYL_ACETATE
  name = G4_POLYVINYL_ACETATE
  specific = 4
FEATURE [App::DocumentObjectGroupPython] C_element090  label="C_element : 048"  # scripted group (container) (typed FeaturePython)
  n = 2
  ref = C_element
FEATURE [App::DocumentObjectGroupPython] H_element082  label="H_element : 044"  # scripted group (container) (typed FeaturePython)
  n = 4
  ref = H_element
FEATURE [App::DocumentObjectGroupPython] O_element082  label="O_element : 043"  # scripted group (container) (typed FeaturePython)
  n = 1
  ref = O_element
FEATURE [App::DocumentObjectGroupPython] G4_POLYVINYL_ALCOHOL  # scripted group (container) (typed FeaturePython)
  Dunit = g/cm3
  Dvalue = 1.3
  Group = -> [C_element090,H_element082,O_element082]
  conduct = 2
  density = 1
  expand = 3
  formula = G4_POLYVINYL_ALCOHOL
  name = G4_POLYVINYL_ALCOHOL
  specific = 4
FEATURE [App::DocumentObjectGroupPython] C_element091  label="C_element : 049"  # scripted group (container) (typed FeaturePython)
  n = 8
  ref = C_element
FEATURE [App::DocumentObjectGroupPython] H_element083  label="H_element : 045"  # scripted group (container) (typed FeaturePython)
  n = 14
  ref = H_element
FEATURE [App::DocumentObjectGroupPython] O_element083  label="O_element : 044"  # scripted group (container) (typed FeaturePython)
  n = 2
  ref = O_element
FEATURE [App::DocumentObjectGroupPython] G4_POLYVINYL_BUTYRAL  # scripted group (container) (typed FeaturePython)
  Dunit = g/cm3
  Dvalue = 1.12
  Group = -> [C_element091,H_element083,O_element083]
  conduct = 2
  density = 1
  expand = 3
  formula = G4_POLYVINYL_BUTYRAL
  name = G4_POLYVINYL_BUTYRAL
  specific = 4
FEATURE [App::DocumentObjectGroupPython] C_element092  label="C_element : 050"  # scripted group (container) (typed FeaturePython)
  n = 2
  ref = C_element
FEATURE [App::DocumentObjectGroupPython] H_element084  label="H_element : 046"  # scripted group (container) (typed FeaturePython)
  n = 3
  ref = H_element
FEATURE [App::DocumentObjectGroupPython] Cl_element019  label="Cl_element : 009"  # scripted group (container) (typed FeaturePython)
  n = 1
  ref = Cl_element
FEATURE [App::DocumentObjectGroupPython] G4_POLYVINYL_CHLORIDE  # scripted group (container) (typed FeaturePython)
  Dunit = g/cm3
  Dvalue = 1.3
  Group = -> [C_element092,H_element084,Cl_element019]
  conduct = 2
  density = 1
  expand = 3
  formula = G4_POLYVINYL_CHLORIDE
  name = G4_POLYVINYL_CHLORIDE
  specific = 4
FEATURE [App::DocumentObjectGroupPython] C_element093  label="C_element : 051"  # scripted group (container) (typed FeaturePython)
  n = 2
  ref = C_element
FEATURE [App::DocumentObjectGroupPython] H_element085  label="H_element : 047"  # scripted group (container) (typed FeaturePython)
  n = 2
  ref = H_element
FEATURE [App::DocumentObjectGroupPython] Cl_element020  label="Cl_element : 010"  # scripted group (container) (typed FeaturePython)
  n = 2
  ref = Cl_element
FEATURE [App::DocumentObjectGroupPython] G4_POLYVINYLIDENE_CHLORIDE  # scripted group (container) (typed FeaturePython)
  Dunit = g/cm3
  Dvalue = 1.7
  Group = -> [C_element093,H_element085,Cl_element020]
  conduct = 2
  density = 1
  expand = 3
  formula = G4_POLYVINYLIDENE_CHLORIDE
  name = G4_POLYVINYLIDENE_CHLORIDE
  specific = 4
FEATURE [App::DocumentObjectGroupPython] C_element094  label="C_element : 052"  # scripted group (container) (typed FeaturePython)
  n = 2
  ref = C_element
FEATURE [App::DocumentObjectGroupPython] H_element086  label="H_element : 048"  # scripted group (container) (typed FeaturePython)
  n = 2
  ref = H_element
FEATURE [App::DocumentObjectGroupPython] F_element016  label="F_element : 007"  # scripted group (container) (typed FeaturePython)
  n = 2
  ref = F_element
FEATURE [App::DocumentObjectGroupPython] G4_POLYVINYLIDENE_FLUORIDE  # scripted group (container) (typed FeaturePython)
  Dunit = g/cm3
  Dvalue = 1.76
  Group = -> [C_element094,H_element086,F_element016]
  conduct = 2
  density = 1
  expand = 3
  formula = G4_POLYVINYLIDENE_FLUORIDE
  name = G4_POLYVINYLIDENE_FLUORIDE
  specific = 4
FEATURE [App::DocumentObjectGroupPython] C_element095  label="C_element : 053"  # scripted group (container) (typed FeaturePython)
  n = 6
  ref = C_element
FEATURE [App::DocumentObjectGroupPython] H_element087  label="H_element : 9"  # scripted group (container) (typed FeaturePython)
  n = 9
  ref = H_element
FEATURE [App::DocumentObjectGroupPython] N_element037  label="N_element : 016"  # scripted group (container) (typed FeaturePython)
  n = 1
  ref = N_element
FEATURE [App::DocumentObjectGroupPython] O_element084  label="O_element : 045"  # scripted group (container) (typed FeaturePython)
  n = 1
  ref = O_element
FEATURE [App::DocumentObjectGroupPython] G4_POLYVINYL_PYRROLIDONE  # scripted group (container) (typed FeaturePython)
  Dunit = g/cm3
  Dvalue = 1.25
  Group = -> [C_element095,H_element087,N_element037,O_element084]
  conduct = 2
  density = 1
  expand = 3
  formula = G4_POLYVINYL_PYRROLIDONE
  name = G4_POLYVINYL_PYRROLIDONE
  specific = 4
FEATURE [App::DocumentObjectGroupPython] K_element008  label="K_element : 1"  # scripted group (container) (typed FeaturePython)
  n = 1
  ref = K_element
FEATURE [App::DocumentObjectGroupPython] I_element006  label="I_element : 003"  # scripted group (container) (typed FeaturePython)
  n = 1
  ref = I_element
FEATURE [App::DocumentObjectGroupPython] G4_POTASSIUM_IODIDE  # scripted group (container) (typed FeaturePython)
  Dunit = g/cm3
  Dvalue = 3.13
  Group = -> [K_element008,I_element006]
  conduct = 2
  density = 1
  expand = 3
  formula = G4_POTASSIUM_IODIDE
  name = G4_POTASSIUM_IODIDE
  specific = 4
FEATURE [App::DocumentObjectGroupPython] K_element009  label="K_element : 2"  # scripted group (container) (typed FeaturePython)
  n = 2
  ref = K_element
FEATURE [App::DocumentObjectGroupPython] O_element085  label="O_element : 046"  # scripted group (container) (typed FeaturePython)
  n = 1
  ref = O_element
FEATURE [App::DocumentObjectGroupPython] G4_POTASSIUM_OXIDE  # scripted group (container) (typed FeaturePython)
  Dunit = g/cm3
  Dvalue = 2.32
  Group = -> [K_element009,O_element085]
  conduct = 2
  density = 1
  expand = 3
  formula = G4_POTASSIUM_OXIDE
  name = G4_POTASSIUM_OXIDE
  specific = 4
FEATURE [App::DocumentObjectGroupPython] C_element096  label="C_element : 054"  # scripted group (container) (typed FeaturePython)
  n = 3
  ref = C_element
FEATURE [App::DocumentObjectGroupPython] H_element088  label="H_element : 049"  # scripted group (container) (typed FeaturePython)
  n = 8
  ref = H_element
FEATURE [App::DocumentObjectGroupPython] G4_PROPANE  # scripted group (container) (typed FeaturePython)
  Dunit = g/cm3
  Dvalue = 0.00187939
  Group = -> [C_element096,H_element088]
  conduct = 2
  density = 1
  expand = 3
  formula = G4_PROPANE
  name = G4_PROPANE
  specific = 4
FEATURE [App::DocumentObjectGroupPython] C_element097  label="C_element : 055"  # scripted group (container) (typed FeaturePython)
  n = 3
  ref = C_element
FEATURE [App::DocumentObjectGroupPython] H_element089  label="H_element : 050"  # scripted group (container) (typed FeaturePython)
  n = 8
  ref = H_element
FEATURE [App::DocumentObjectGroupPython] G4_lPROPANE  # scripted group (container) (typed FeaturePython)
  Dunit = g/cm3
  Dvalue = 0.43
  Group = -> [C_element097,H_element089]
  conduct = 2
  density = 1
  expand = 3
  formula = G4_lPROPANE
  name = G4_lPROPANE
  specific = 4
FEATURE [App::DocumentObjectGroupPython] C_element098  label="C_element : 056"  # scripted group (container) (typed FeaturePython)
  n = 3
  ref = C_element
FEATURE [App::DocumentObjectGroupPython] H_element090  label="H_element : 051"  # scripted group (container) (typed FeaturePython)
  n = 8
  ref = H_element
FEATURE [App::DocumentObjectGroupPython] O_element086  label="O_element : 047"  # scripted group (container) (typed FeaturePython)
  n = 1
  ref = O_element
FEATURE [App::DocumentObjectGroupPython] G4_N_PROPYL_ALCOHOL  label="G4_N-PROPYL_ALCOHOL"  # scripted group (container) (typed FeaturePython)
  Dunit = g/cm3
  Dvalue = 0.8035
  Group = -> [C_element098,H_element090,O_element086]
  conduct = 2
  density = 1
  expand = 3
  formula = G4_N-PROPYL_ALCOHOL
  name = G4_N-PROPYL_ALCOHOL
  specific = 4
FEATURE [App::DocumentObjectGroupPython] C_element099  label="C_element : 057"  # scripted group (container) (typed FeaturePython)
  n = 5
  ref = C_element
FEATURE [App::DocumentObjectGroupPython] H_element091  label="H_element : 052"  # scripted group (container) (typed FeaturePython)
  n = 5
  ref = H_element
FEATURE [App::DocumentObjectGroupPython] N_element038  label="N_element : 017"  # scripted group (container) (typed FeaturePython)
  n = 1
  ref = N_element
FEATURE [App::DocumentObjectGroupPython] G4_PYRIDINE  # scripted group (container) (typed FeaturePython)
  Dunit = g/cm3
  Dvalue = 0.9819
  Group = -> [C_element099,H_element091,N_element038]
  conduct = 2
  density = 1
  expand = 3
  formula = G4_PYRIDINE
  name = G4_PYRIDINE
  specific = 4
FEATURE [App::DocumentObjectGroupPython] H_element092  label="H_element : 0.144"  # scripted group (container) (typed FeaturePython)
  n = 0.143711
FEATURE [App::DocumentObjectGroupPython] C_element100  label="C_element : 0.856"  # scripted group (container) (typed FeaturePython)
  n = 0.856289
FEATURE [App::DocumentObjectGroupPython] G4_RUBBER_BUTYL  # scripted group (container) (typed FeaturePython)
  Dunit = g/cm3
  Dvalue = 0.92
  Group = -> [H_element092,C_element100]
  conduct = 2
  density = 1
  expand = 3
  formula = G4_RUBBER_BUTYL
  name = G4_RUBBER_BUTYL
  specific = 4
FEATURE [App::DocumentObjectGroupPython] H_element093  label="H_element : 0.118"  # scripted group (container) (typed FeaturePython)
  n = 0.118371
FEATURE [App::DocumentObjectGroupPython] C_element101  label="C_element : 0.882"  # scripted group (container) (typed FeaturePython)
  n = 0.881629
FEATURE [App::DocumentObjectGroupPython] G4_RUBBER_NATURAL  # scripted group (container) (typed FeaturePython)
  Dunit = g/cm3
  Dvalue = 0.92
  Group = -> [H_element093,C_element101]
  conduct = 2
  density = 1
  expand = 3
  formula = G4_RUBBER_NATURAL
  name = G4_RUBBER_NATURAL
  specific = 4
FEATURE [App::DocumentObjectGroupPython] H_element094  label="H_element : 0.145"  # scripted group (container) (typed FeaturePython)
  n = 0.05692
FEATURE [App::DocumentObjectGroupPython] C_element102  label="C_element : 0.543"  # scripted group (container) (typed FeaturePython)
  n = 0.542646
FEATURE [App::DocumentObjectGroupPython] Cl_element021  label="Cl_element : 0.400"  # scripted group (container) (typed FeaturePython)
  n = 0.400434
FEATURE [App::DocumentObjectGroupPython] G4_RUBBER_NEOPRENE  # scripted group (container) (typed FeaturePython)
  Dunit = g/cm3
  Dvalue = 1.23
  Group = -> [H_element094,C_element102,Cl_element021]
  conduct = 2
  density = 1
  expand = 3
  formula = G4_RUBBER_NEOPRENE
  name = G4_RUBBER_NEOPRENE
  specific = 4
FEATURE [App::DocumentObjectGroupPython] Si_element006  label="Si_element : 1"  # scripted group (container) (typed FeaturePython)
  n = 1
  ref = Si_element
FEATURE [App::DocumentObjectGroupPython] O_element087  label="O_element : 048"  # scripted group (container) (typed FeaturePython)
  n = 2
  ref = O_element
FEATURE [App::DocumentObjectGroupPython] G4_SILICON_DIOXIDE  # scripted group (container) (typed FeaturePython)
  Dunit = g/cm3
  Dvalue = 2.32
  Group = -> [Si_element006,O_element087]
  conduct = 2
  density = 1
  expand = 3
  formula = G4_SILICON_DIOXIDE
  name = G4_SILICON_DIOXIDE
  specific = 4
FEATURE [App::DocumentObjectGroupPython] Ag_element002  label="Ag_element : 1"  # scripted group (container) (typed FeaturePython)
  n = 1
  ref = Ag_element
FEATURE [App::DocumentObjectGroupPython] Br_element005  label="Br_element : 003"  # scripted group (container) (typed FeaturePython)
  n = 1
  ref = Br_element
FEATURE [App::DocumentObjectGroupPython] G4_SILVER_BROMIDE  # scripted group (container) (typed FeaturePython)
  Dunit = g/cm3
  Dvalue = 6.473
  Group = -> [Ag_element002,Br_element005]
  conduct = 2
  density = 1
  expand = 3
  formula = G4_SILVER_BROMIDE
  name = G4_SILVER_BROMIDE
  specific = 4
FEATURE [App::DocumentObjectGroupPython] Ag_element003  label="Ag_element : 002"  # scripted group (container) (typed FeaturePython)
  n = 1
  ref = Ag_element
FEATURE [App::DocumentObjectGroupPython] Cl_element022  label="Cl_element : 011"  # scripted group (container) (typed FeaturePython)
  n = 1
  ref = Cl_element
FEATURE [App::DocumentObjectGroupPython] G4_SILVER_CHLORIDE  # scripted group (container) (typed FeaturePython)
  Dunit = g/cm3
  Dvalue = 5.56
  Group = -> [Ag_element003,Cl_element022]
  conduct = 2
  density = 1
  expand = 3
  formula = G4_SILVER_CHLORIDE
  name = G4_SILVER_CHLORIDE
  specific = 4
FEATURE [App::DocumentObjectGroupPython] Br_element006  label="Br_element : 0.423"  # scripted group (container) (typed FeaturePython)
  n = 0.422895
FEATURE [App::DocumentObjectGroupPython] Ag_element004  label="Ag_element : 0.574"  # scripted group (container) (typed FeaturePython)
  n = 0.573748
FEATURE [App::DocumentObjectGroupPython] I_element007  label="I_element : 0.649"  # scripted group (container) (typed FeaturePython)
  n = 0.003357
FEATURE [App::DocumentObjectGroupPython] G4_SILVER_HALIDES  # scripted group (container) (typed FeaturePython)
  Dunit = g/cm3
  Dvalue = 6.47
  Group = -> [Br_element006,Ag_element004,I_element007]
  conduct = 2
  density = 1
  expand = 3
  formula = G4_SILVER_HALIDES
  name = G4_SILVER_HALIDES
  specific = 4
FEATURE [App::DocumentObjectGroupPython] Ag_element005  label="Ag_element : 003"  # scripted group (container) (typed FeaturePython)
  n = 1
  ref = Ag_element
FEATURE [App::DocumentObjectGroupPython] I_element008  label="I_element : 004"  # scripted group (container) (typed FeaturePython)
  n = 1
  ref = I_element
FEATURE [App::DocumentObjectGroupPython] G4_SILVER_IODIDE  # scripted group (container) (typed FeaturePython)
  Dunit = g/cm3
  Dvalue = 6.01
  Group = -> [Ag_element005,I_element008]
  conduct = 2
  density = 1
  expand = 3
  formula = G4_SILVER_IODIDE
  name = G4_SILVER_IODIDE
  specific = 4
FEATURE [App::DocumentObjectGroupPython] H_element095  label="H_element : 0.100"  # scripted group (container) (typed FeaturePython)
  n = 0.1
FEATURE [App::DocumentObjectGroupPython] C_element103  label="C_element : 0.204"  # scripted group (container) (typed FeaturePython)
  n = 0.204
FEATURE [App::DocumentObjectGroupPython] N_element039  label="N_element : 0.759"  # scripted group (container) (typed FeaturePython)
  n = 0.042
FEATURE [App::DocumentObjectGroupPython] O_element088  label="O_element : 0.645"  # scripted group (container) (typed FeaturePython)
  n = 0.645
FEATURE [App::DocumentObjectGroupPython] Na_element013  label="Na_element : 0.100"  # scripted group (container) (typed FeaturePython)
  n = 0.002
FEATURE [App::DocumentObjectGroupPython] P_element009  label="P_element : 0.107"  # scripted group (container) (typed FeaturePython)
  n = 0.001
FEATURE [App::DocumentObjectGroupPython] S_element020  label="S_element : 0.021"  # scripted group (container) (typed FeaturePython)
  n = 0.002
FEATURE [App::DocumentObjectGroupPython] Cl_element023  label="Cl_element : 0.590"  # scripted group (container) (typed FeaturePython)
  n = 0.003
FEATURE [App::DocumentObjectGroupPython] K_element010  label="K_element : 0.001"  # scripted group (container) (typed FeaturePython)
  n = 0.001
FEATURE [App::DocumentObjectGroupPython] G4_SKIN_ICRP  # scripted group (container) (typed FeaturePython)
  Dunit = g/cm3
  Dvalue = 1.09
  Group = -> [H_element095,C_element103,N_element039,O_element088,Na_element013,P_element009,S_element020,Cl_element023,K_element010]
  conduct = 2
  density = 1
  expand = 3
  formula = G4_SKIN_ICRP
  name = G4_SKIN_ICRP
  specific = 4
FEATURE [App::DocumentObjectGroupPython] Na_element014  label="Na_element : 2"  # scripted group (container) (typed FeaturePython)
  n = 2
  ref = Na_element
FEATURE [App::DocumentObjectGroupPython] C_element104  label="C_element : 058"  # scripted group (container) (typed FeaturePython)
  n = 1
  ref = C_element
FEATURE [App::DocumentObjectGroupPython] O_element089  label="O_element : 049"  # scripted group (container) (typed FeaturePython)
  n = 3
  ref = O_element
FEATURE [App::DocumentObjectGroupPython] G4_SODIUM_CARBONATE  # scripted group (container) (typed FeaturePython)
  Dunit = g/cm3
  Dvalue = 2.532
  Group = -> [Na_element014,C_element104,O_element089]
  conduct = 2
  density = 1
  expand = 3
  formula = G4_SODIUM_CARBONATE
  name = G4_SODIUM_CARBONATE
  specific = 4
FEATURE [App::DocumentObjectGroupPython] Na_element015  label="Na_element : 1"  # scripted group (container) (typed FeaturePython)
  n = 1
  ref = Na_element
FEATURE [App::DocumentObjectGroupPython] I_element009  label="I_element : 005"  # scripted group (container) (typed FeaturePython)
  n = 1
  ref = I_element
FEATURE [App::DocumentObjectGroupPython] G4_SODIUM_IODIDE  # scripted group (container) (typed FeaturePython)
  Dunit = g/cm3
  Dvalue = 3.667
  Group = -> [Na_element015,I_element009]
  conduct = 2
  density = 1
  expand = 3
  formula = G4_SODIUM_IODIDE
  name = G4_SODIUM_IODIDE
  specific = 4
FEATURE [App::DocumentObjectGroupPython] Na_element016  label="Na_element : 003"  # scripted group (container) (typed FeaturePython)
  n = 2
  ref = Na_element
FEATURE [App::DocumentObjectGroupPython] O_element090  label="O_element : 050"  # scripted group (container) (typed FeaturePython)
  n = 1
  ref = O_element
FEATURE [App::DocumentObjectGroupPython] G4_SODIUM_MONOXIDE  # scripted group (container) (typed FeaturePython)
  Dunit = g/cm3
  Dvalue = 2.27
  Group = -> [Na_element016,O_element090]
  conduct = 2
  density = 1
  expand = 3
  formula = G4_SODIUM_MONOXIDE
  name = G4_SODIUM_MONOXIDE
  specific = 4
FEATURE [App::DocumentObjectGroupPython] Na_element017  label="Na_element : 004"  # scripted group (container) (typed FeaturePython)
  n = 1
  ref = Na_element
FEATURE [App::DocumentObjectGroupPython] N_element040  label="N_element : 018"  # scripted group (container) (typed FeaturePython)
  n = 1
  ref = N_element
FEATURE [App::DocumentObjectGroupPython] O_element091  label="O_element : 051"  # scripted group (container) (typed FeaturePython)
  n = 3
  ref = O_element
FEATURE [App::DocumentObjectGroupPython] G4_SODIUM_NITRATE  # scripted group (container) (typed FeaturePython)
  Dunit = g/cm3
  Dvalue = 2.261
  Group = -> [Na_element017,N_element040,O_element091]
  conduct = 2
  density = 1
  expand = 3
  formula = G4_SODIUM_NITRATE
  name = G4_SODIUM_NITRATE
  specific = 4
FEATURE [App::DocumentObjectGroupPython] C_element105  label="C_element : 059"  # scripted group (container) (typed FeaturePython)
  n = 14
  ref = C_element
FEATURE [App::DocumentObjectGroupPython] H_element096  label="H_element : 053"  # scripted group (container) (typed FeaturePython)
  n = 12
  ref = H_element
FEATURE [App::DocumentObjectGroupPython] G4_STILBENE  # scripted group (container) (typed FeaturePython)
  Dunit = g/cm3
  Dvalue = 0.9707
  Group = -> [C_element105,H_element096]
  conduct = 2
  density = 1
  expand = 3
  formula = G4_STILBENE
  name = G4_STILBENE
  specific = 4
FEATURE [App::DocumentObjectGroupPython] C_element106  label="C_element : 12"  # scripted group (container) (typed FeaturePython)
  n = 12
  ref = C_element
FEATURE [App::DocumentObjectGroupPython] H_element097  label="H_element : 22"  # scripted group (container) (typed FeaturePython)
  n = 22
  ref = H_element
FEATURE [App::DocumentObjectGroupPython] O_element092  label="O_element : 11"  # scripted group (container) (typed FeaturePython)
  n = 11
  ref = O_element
FEATURE [App::DocumentObjectGroupPython] G4_SUCROSE  # scripted group (container) (typed FeaturePython)
  Dunit = g/cm3
  Dvalue = 1.5805
  Group = -> [C_element106,H_element097,O_element092]
  conduct = 2
  density = 1
  expand = 3
  formula = G4_SUCROSE
  name = G4_SUCROSE
  specific = 4
FEATURE [App::DocumentObjectGroupPython] C_element107  label="C_element : 18"  # scripted group (container) (typed FeaturePython)
  n = 18
  ref = C_element
FEATURE [App::DocumentObjectGroupPython] H_element098  label="H_element : 054"  # scripted group (container) (typed FeaturePython)
  n = 14
  ref = H_element
FEATURE [App::DocumentObjectGroupPython] G4_TERPHENYL  # scripted group (container) (typed FeaturePython)
  Dunit = g/cm3
  Dvalue = 1.24
  Group = -> [C_element107,H_element098]
  conduct = 2
  density = 1
  expand = 3
  formula = G4_TERPHENYL
  name = G4_TERPHENYL
  specific = 4
FEATURE [App::DocumentObjectGroupPython] H_element099  label="H_element : 0.146"  # scripted group (container) (typed FeaturePython)
  n = 0.106
FEATURE [App::DocumentObjectGroupPython] C_element108  label="C_element : 0.883"  # scripted group (container) (typed FeaturePython)
  n = 0.099
FEATURE [App::DocumentObjectGroupPython] N_element041  label="N_element : 0.020"  # scripted group (container) (typed FeaturePython)
  n = 0.02
FEATURE [App::DocumentObjectGroupPython] O_element093  label="O_element : 0.766"  # scripted group (container) (typed FeaturePython)
  n = 0.766
FEATURE [App::DocumentObjectGroupPython] Na_element018  label="Na_element : 0.101"  # scripted group (container) (typed FeaturePython)
  n = 0.002
FEATURE [App::DocumentObjectGroupPython] P_element010  label="P_element : 0.108"  # scripted group (container) (typed FeaturePython)
  n = 0.001
FEATURE [App::DocumentObjectGroupPython] S_element021  label="S_element : 0.022"  # scripted group (container) (typed FeaturePython)
  n = 0.002
FEATURE [App::DocumentObjectGroupPython] Cl_element024  label="Cl_element : 0.002"  # scripted group (container) (typed FeaturePython)
  n = 0.002
FEATURE [App::DocumentObjectGroupPython] K_element011  label="K_element : 0.017"  # scripted group (container) (typed FeaturePython)
  n = 0.002
FEATURE [App::DocumentObjectGroupPython] G4_TESTIS_ICRP  # scripted group (container) (typed FeaturePython)
  Dunit = g/cm3
  Dvalue = 1.04
  Group = -> [H_element099,C_element108,N_element041,O_element093,Na_element018,P_element010,S_element021,Cl_element024,K_element011]
  conduct = 2
  density = 1
  expand = 3
  formula = G4_TESTIS_ICRP
  name = G4_TESTIS_ICRP
  specific = 4
FEATURE [App::DocumentObjectGroupPython] C_element109  label="C_element : 060"  # scripted group (container) (typed FeaturePython)
  n = 2
  ref = C_element
FEATURE [App::DocumentObjectGroupPython] Cl_element025  label="Cl_element : 012"  # scripted group (container) (typed FeaturePython)
  n = 4
  ref = Cl_element
FEATURE [App::DocumentObjectGroupPython] G4_TETRACHLOROETHYLENE  # scripted group (container) (typed FeaturePython)
  Dunit = g/cm3
  Dvalue = 1.625
  Group = -> [C_element109,Cl_element025]
  conduct = 2
  density = 1
  expand = 3
  formula = G4_TETRACHLOROETHYLENE
  name = G4_TETRACHLOROETHYLENE
  specific = 4
FEATURE [App::DocumentObjectGroupPython] Tl_element001  label="Tl_element : 1"  # scripted group (container) (typed FeaturePython)
  n = 1
  ref = Tl_element
FEATURE [App::DocumentObjectGroupPython] Cl_element026  label="Cl_element : 013"  # scripted group (container) (typed FeaturePython)
  n = 1
  ref = Cl_element
FEATURE [App::DocumentObjectGroupPython] G4_THALLIUM_CHLORIDE  # scripted group (container) (typed FeaturePython)
  Dunit = g/cm3
  Dvalue = 7.004
  Group = -> [Tl_element001,Cl_element026]
  conduct = 2
  density = 1
  expand = 3
  formula = G4_THALLIUM_CHLORIDE
  name = G4_THALLIUM_CHLORIDE
  specific = 4
FEATURE [App::DocumentObjectGroupPython] H_element100  label="H_element : 0.147"  # scripted group (container) (typed FeaturePython)
  n = 0.105
FEATURE [App::DocumentObjectGroupPython] C_element110  label="C_element : 0.256"  # scripted group (container) (typed FeaturePython)
  n = 0.256
FEATURE [App::DocumentObjectGroupPython] N_element042  label="N_element : 0.760"  # scripted group (container) (typed FeaturePython)
  n = 0.027
FEATURE [App::DocumentObjectGroupPython] O_element094  label="O_element : 0.602"  # scripted group (container) (typed FeaturePython)
  n = 0.602
FEATURE [App::DocumentObjectGroupPython] Na_element019  label="Na_element : 0.102"  # scripted group (container) (typed FeaturePython)
  n = 0.001
FEATURE [App::DocumentObjectGroupPython] P_element011  label="P_element : 0.109"  # scripted group (container) (typed FeaturePython)
  n = 0.002
FEATURE [App::DocumentObjectGroupPython] S_element022  label="S_element : 0.023"  # scripted group (container) (typed FeaturePython)
  n = 0.003
FEATURE [App::DocumentObjectGroupPython] Cl_element027  label="Cl_element : 0.591"  # scripted group (container) (typed FeaturePython)
  n = 0.002
FEATURE [App::DocumentObjectGroupPython] K_element012  label="K_element : 0.018"  # scripted group (container) (typed FeaturePython)
  n = 0.002
FEATURE [App::DocumentObjectGroupPython] G4_TISSUE_SOFT_ICRP  # scripted group (container) (typed FeaturePython)
  Dunit = g/cm3
  Dvalue = 1.03
  Group = -> [H_element100,C_element110,N_element042,O_element094,Na_element019,P_element011,S_element022,Cl_element027,K_element012]
  conduct = 2
  density = 1
  expand = 3
  formula = G4_TISSUE_SOFT_ICRP
  name = G4_TISSUE_SOFT_ICRP
  specific = 4
FEATURE [App::DocumentObjectGroupPython] H_element101  label="H_element : 0.148"  # scripted group (container) (typed FeaturePython)
  n = 0.101
FEATURE [App::DocumentObjectGroupPython] C_element111  label="C_element : 0.111"  # scripted group (container) (typed FeaturePython)
  n = 0.111
FEATURE [App::DocumentObjectGroupPython] N_element043  label="N_element : 0.026"  # scripted group (container) (typed FeaturePython)
  n = 0.026
FEATURE [App::DocumentObjectGroupPython] O_element095  label="O_element : 0.762"  # scripted group (container) (typed FeaturePython)
  n = 0.762
FEATURE [App::DocumentObjectGroupPython] G4_TISSUE_SOFT_ICRU_4  label="G4_TISSUE_SOFT_ICRU-4"  # scripted group (container) (typed FeaturePython)
  Dunit = g/cm3
  Dvalue = 1
  Group = -> [H_element101,C_element111,N_element043,O_element095]
  conduct = 2
  density = 1
  expand = 3
  formula = G4_TISSUE_SOFT_ICRU-4
  name = G4_TISSUE_SOFT_ICRU-4
  specific = 4
FEATURE [App::DocumentObjectGroupPython] H_element102  label="H_element : 0.149"  # scripted group (container) (typed FeaturePython)
  n = 0.101869
FEATURE [App::DocumentObjectGroupPython] C_element112  label="C_element : 0.456"  # scripted group (container) (typed FeaturePython)
  n = 0.456179
FEATURE [App::DocumentObjectGroupPython] N_element044  label="N_element : 0.761"  # scripted group (container) (typed FeaturePython)
  n = 0.035172
FEATURE [App::DocumentObjectGroupPython] O_element096  label="O_element : 0.407"  # scripted group (container) (typed FeaturePython)
  n = 0.40678
FEATURE [App::DocumentObjectGroupPython] G4_TISSUE_METHANE  label="G4_TISSUE-METHANE"  # scripted group (container) (typed FeaturePython)
  Dunit = g/cm3
  Dvalue = 0.00106409
  Group = -> [H_element102,C_element112,N_element044,O_element096]
  conduct = 2
  density = 1
  expand = 3
  formula = G4_TISSUE-METHANE
  name = G4_TISSUE-METHANE
  specific = 4
FEATURE [App::DocumentObjectGroupPython] H_element103  label="H_element : 0.103"  # scripted group (container) (typed FeaturePython)
  n = 0.102672
FEATURE [App::DocumentObjectGroupPython] C_element113  label="C_element : 0.569"  # scripted group (container) (typed FeaturePython)
  n = 0.56894
FEATURE [App::DocumentObjectGroupPython] N_element045  label="N_element : 0.762"  # scripted group (container) (typed FeaturePython)
  n = 0.035022
FEATURE [App::DocumentObjectGroupPython] O_element097  label="O_element : 0.293"  # scripted group (container) (typed FeaturePython)
  n = 0.293366
FEATURE [App::DocumentObjectGroupPython] G4_TISSUE_PROPANE  label="G4_TISSUE-PROPANE"  # scripted group (container) (typed FeaturePython)
  Dunit = g/cm3
  Dvalue = 0.00182628
  Group = -> [H_element103,C_element113,N_element045,O_element097]
  conduct = 2
  density = 1
  expand = 3
  formula = G4_TISSUE-PROPANE
  name = G4_TISSUE-PROPANE
  specific = 4
FEATURE [App::DocumentObjectGroupPython] Ti_element003  label="Ti_element : 1"  # scripted group (container) (typed FeaturePython)
  n = 1
  ref = Ti_element
FEATURE [App::DocumentObjectGroupPython] O_element098  label="O_element : 052"  # scripted group (container) (typed FeaturePython)
  n = 2
  ref = O_element
FEATURE [App::DocumentObjectGroupPython] G4_TITANIUM_DIOXIDE  # scripted group (container) (typed FeaturePython)
  Dunit = g/cm3
  Dvalue = 4.26
  Group = -> [Ti_element003,O_element098]
  conduct = 2
  density = 1
  expand = 3
  formula = G4_TITANIUM_DIOXIDE
  name = G4_TITANIUM_DIOXIDE
  specific = 4
FEATURE [App::DocumentObjectGroupPython] C_element114  label="C_element : 061"  # scripted group (container) (typed FeaturePython)
  n = 7
  ref = C_element
FEATURE [App::DocumentObjectGroupPython] H_element104  label="H_element : 055"  # scripted group (container) (typed FeaturePython)
  n = 8
  ref = H_element
FEATURE [App::DocumentObjectGroupPython] G4_TOLUENE  # scripted group (container) (typed FeaturePython)
  Dunit = g/cm3
  Dvalue = 0.8669
  Group = -> [C_element114,H_element104]
  conduct = 2
  density = 1
  expand = 3
  formula = G4_TOLUENE
  name = G4_TOLUENE
  specific = 4
FEATURE [App::DocumentObjectGroupPython] C_element115  label="C_element : 062"  # scripted group (container) (typed FeaturePython)
  n = 2
  ref = C_element
FEATURE [App::DocumentObjectGroupPython] H_element105  label="H_element : 056"  # scripted group (container) (typed FeaturePython)
  n = 1
  ref = H_element
FEATURE [App::DocumentObjectGroupPython] Cl_element028  label="Cl_element : 014"  # scripted group (container) (typed FeaturePython)
  n = 3
  ref = Cl_element
FEATURE [App::DocumentObjectGroupPython] G4_TRICHLOROETHYLENE  # scripted group (container) (typed FeaturePython)
  Dunit = g/cm3
  Dvalue = 1.46
  Group = -> [C_element115,H_element105,Cl_element028]
  conduct = 2
  density = 1
  expand = 3
  formula = G4_TRICHLOROETHYLENE
  name = G4_TRICHLOROETHYLENE
  specific = 4
FEATURE [App::DocumentObjectGroupPython] C_element116  label="C_element : 063"  # scripted group (container) (typed FeaturePython)
  n = 6
  ref = C_element
FEATURE [App::DocumentObjectGroupPython] H_element106  label="H_element : 15"  # scripted group (container) (typed FeaturePython)
  n = 15
  ref = H_element
FEATURE [App::DocumentObjectGroupPython] O_element099  label="O_element : 053"  # scripted group (container) (typed FeaturePython)
  n = 4
  ref = O_element
FEATURE [App::DocumentObjectGroupPython] P_element012  label="P_element : 1"  # scripted group (container) (typed FeaturePython)
  n = 1
  ref = P_element
FEATURE [App::DocumentObjectGroupPython] G4_TRIETHYL_PHOSPHATE  # scripted group (container) (typed FeaturePython)
  Dunit = g/cm3
  Dvalue = 1.07
  Group = -> [C_element116,H_element106,O_element099,P_element012]
  conduct = 2
  density = 1
  expand = 3
  formula = G4_TRIETHYL_PHOSPHATE
  name = G4_TRIETHYL_PHOSPHATE
  specific = 4
FEATURE [App::DocumentObjectGroupPython] W_element003  label="W_element : 003"  # scripted group (container) (typed FeaturePython)
  n = 1
  ref = W_element
FEATURE [App::DocumentObjectGroupPython] F_element017  label="F_element : 6"  # scripted group (container) (typed FeaturePython)
  n = 6
  ref = F_element
FEATURE [App::DocumentObjectGroupPython] G4_TUNGSTEN_HEXAFLUORIDE  # scripted group (container) (typed FeaturePython)
  Dunit = g/cm3
  Dvalue = 2.4
  Group = -> [W_element003,F_element017]
  conduct = 2
  density = 1
  expand = 3
  formula = G4_TUNGSTEN_HEXAFLUORIDE
  name = G4_TUNGSTEN_HEXAFLUORIDE
  specific = 4
FEATURE [App::DocumentObjectGroupPython] U_element001  label="U_element : 1"  # scripted group (container) (typed FeaturePython)
  n = 1
  ref = U_element
FEATURE [App::DocumentObjectGroupPython] C_element117  label="C_element : 064"  # scripted group (container) (typed FeaturePython)
  n = 2
  ref = C_element
FEATURE [App::DocumentObjectGroupPython] G4_URANIUM_DICARBIDE  # scripted group (container) (typed FeaturePython)
  Dunit = g/cm3
  Dvalue = 11.28
  Group = -> [U_element001,C_element117]
  conduct = 2
  density = 1
  expand = 3
  formula = G4_URANIUM_DICARBIDE
  name = G4_URANIUM_DICARBIDE
  specific = 4
FEATURE [App::DocumentObjectGroupPython] U_element002  label="U_element : 002"  # scripted group (container) (typed FeaturePython)
  n = 1
  ref = U_element
FEATURE [App::DocumentObjectGroupPython] C_element118  label="C_element : 065"  # scripted group (container) (typed FeaturePython)
  n = 1
  ref = C_element
FEATURE [App::DocumentObjectGroupPython] G4_URANIUM_MONOCARBIDE  # scripted group (container) (typed FeaturePython)
  Dunit = g/cm3
  Dvalue = 13.63
  Group = -> [U_element002,C_element118]
  conduct = 2
  density = 1
  expand = 3
  formula = G4_URANIUM_MONOCARBIDE
  name = G4_URANIUM_MONOCARBIDE
  specific = 4
FEATURE [App::DocumentObjectGroupPython] U_element003  label="U_element : 003"  # scripted group (container) (typed FeaturePython)
  n = 1
  ref = U_element
FEATURE [App::DocumentObjectGroupPython] O_element100  label="O_element : 054"  # scripted group (container) (typed FeaturePython)
  n = 2
  ref = O_element
FEATURE [App::DocumentObjectGroupPython] G4_URANIUM_OXIDE  # scripted group (container) (typed FeaturePython)
  Dunit = g/cm3
  Dvalue = 10.96
  Group = -> [U_element003,O_element100]
  conduct = 2
  density = 1
  expand = 3
  formula = G4_URANIUM_OXIDE
  name = G4_URANIUM_OXIDE
  specific = 4
FEATURE [App::DocumentObjectGroupPython] C_element119  label="C_element : 066"  # scripted group (container) (typed FeaturePython)
  n = 1
  ref = C_element
FEATURE [App::DocumentObjectGroupPython] H_element107  label="H_element : 057"  # scripted group (container) (typed FeaturePython)
  n = 4
  ref = H_element
FEATURE [App::DocumentObjectGroupPython] N_element046  label="N_element : 019"  # scripted group (container) (typed FeaturePython)
  n = 2
  ref = N_element
FEATURE [App::DocumentObjectGroupPython] O_element101  label="O_element : 055"  # scripted group (container) (typed FeaturePython)
  n = 1
  ref = O_element
FEATURE [App::DocumentObjectGroupPython] G4_UREA  # scripted group (container) (typed FeaturePython)
  Dunit = g/cm3
  Dvalue = 1.323
  Group = -> [C_element119,H_element107,N_element046,O_element101]
  conduct = 2
  density = 1
  expand = 3
  formula = G4_UREA
  name = G4_UREA
  specific = 4
FEATURE [App::DocumentObjectGroupPython] C_element120  label="C_element : 067"  # scripted group (container) (typed FeaturePython)
  n = 5
  ref = C_element
FEATURE [App::DocumentObjectGroupPython] H_element108  label="H_element : 058"  # scripted group (container) (typed FeaturePython)
  n = 11
  ref = H_element
FEATURE [App::DocumentObjectGroupPython] N_element047  label="N_element : 020"  # scripted group (container) (typed FeaturePython)
  n = 1
  ref = N_element
FEATURE [App::DocumentObjectGroupPython] O_element102  label="O_element : 056"  # scripted group (container) (typed FeaturePython)
  n = 2
  ref = O_element
FEATURE [App::DocumentObjectGroupPython] G4_VALINE  # scripted group (container) (typed FeaturePython)
  Dunit = g/cm3
  Dvalue = 1.23
  Group = -> [C_element120,H_element108,N_element047,O_element102]
  conduct = 2
  density = 1
  expand = 3
  formula = G4_VALINE
  name = G4_VALINE
  specific = 4
FEATURE [App::DocumentObjectGroupPython] H_element109  label="H_element : 0.009"  # scripted group (container) (typed FeaturePython)
  n = 0.009417
FEATURE [App::DocumentObjectGroupPython] C_element121  label="C_element : 0.281"  # scripted group (container) (typed FeaturePython)
  n = 0.280555
FEATURE [App::DocumentObjectGroupPython] F_element018  label="F_element : 0.710"  # scripted group (container) (typed FeaturePython)
  n = 0.710028
FEATURE [App::DocumentObjectGroupPython] G4_VITON  # scripted group (container) (typed FeaturePython)
  Dunit = g/cm3
  Dvalue = 1.8
  Group = -> [H_element109,C_element121,F_element018]
  conduct = 2
  density = 1
  expand = 3
  formula = G4_VITON
  name = G4_VITON
  specific = 4
FEATURE [App::DocumentObjectGroupPython] H_element110  label="H_element : 059"  # scripted group (container) (typed FeaturePython)
  n = 2
  ref = H_element
FEATURE [App::DocumentObjectGroupPython] O_element103  label="O_element : 057"  # scripted group (container) (typed FeaturePython)
  n = 1
  ref = O_element
FEATURE [App::DocumentObjectGroupPython] G4_WATER  # scripted group (container) (typed FeaturePython)
  Dunit = g/cm3
  Dvalue = 1
  Group = -> [H_element110,O_element103]
  conduct = 2
  density = 1
  expand = 3
  formula = G4_WATER
  name = G4_WATER
  specific = 4
FEATURE [App::DocumentObjectGroupPython] H_element111  label="H_element : 060"  # scripted group (container) (typed FeaturePython)
  n = 2
  ref = H_element
FEATURE [App::DocumentObjectGroupPython] O_element104  label="O_element : 058"  # scripted group (container) (typed FeaturePython)
  n = 1
  ref = O_element
FEATURE [App::DocumentObjectGroupPython] G4_WATER_VAPOR  # scripted group (container) (typed FeaturePython)
  Dunit = g/cm3
  Dvalue = 0.000756182
  Group = -> [H_element111,O_element104]
  conduct = 2
  density = 1
  expand = 3
  formula = G4_WATER_VAPOR
  name = G4_WATER_VAPOR
  specific = 4
FEATURE [App::DocumentObjectGroupPython] C_element122  label="C_element : 068"  # scripted group (container) (typed FeaturePython)
  n = 8
  ref = C_element
FEATURE [App::DocumentObjectGroupPython] H_element112  label="H_element : 061"  # scripted group (container) (typed FeaturePython)
  n = 10
  ref = H_element
FEATURE [App::DocumentObjectGroupPython] G4_XYLENE  # scripted group (container) (typed FeaturePython)
  Dunit = g/cm3
  Dvalue = 0.87
  Group = -> [C_element122,H_element112]
  conduct = 2
  density = 1
  expand = 3
  formula = G4_XYLENE
  name = G4_XYLENE
  specific = 4
FEATURE [App::DocumentObjectGroupPython] C_element123  label="C_element : 069"  # scripted group (container) (typed FeaturePython)
  n = 1
  ref = C_element
FEATURE [App::DocumentObjectGroupPython] G4_GRAPHITE  # scripted group (container) (typed FeaturePython)
  Dunit = g/cm3
  Dvalue = 2.21
  Group = -> [C_element123]
  conduct = 2
  density = 1
  expand = 3
  formula = G4_GRAPHITE
  name = G4_GRAPHITE
  specific = 4
FEATURE [App::DocumentObjectGroupPython] NIST  # scripted group (container) (typed FeaturePython)
  Group = -> [G4_A_150_TISSUE,G4_ACETONE,G4_ACETYLENE,G4_ADENINE,G4_ADIPOSE_TISSUE_ICRP,G4_AIR,G4_ALANINE,G4_ALUMINUM_OXIDE,G4_AMBER,G4_AMMONIA,G4_ANILINE,G4_ANTHRACENE,G4_B_100_BONE,G4_BAKELITE,G4_BARIUM_FLUORIDE,G4_BARIUM_SULFATE,G4_BENZENE,G4_BERYLLIUM_OXIDE,G4_BGO,G4_BLOOD_ICRP,G4_BONE_COMPACT_ICRU,G4_BONE_CORTICAL_ICRP,G4_BORON_CARBIDE,G4_BORON_OXIDE,G4_BRAIN_ICRP,G4_BUTANE,G4_N_BUTYL_ALCOHOL,G4_C_552,+152 more]
FEATURE [App::DocumentObjectGroupPython] H_element113  label="H_element : 062"  # scripted group (container) (typed FeaturePython)
  n = 1
  ref = H_element
FEATURE [App::DocumentObjectGroupPython] G4_H  # scripted group (container) (typed FeaturePython)
  Dunit = g/cm3
  Dvalue = 8.3748e-05
  Group = -> [H_element113]
  conduct = 2
  density = 1
  expand = 3
  formula = H
  name = G4_H
  specific = 4
FEATURE [App::DocumentObjectGroupPython] He_element001  label="He_element : 1"  # scripted group (container) (typed FeaturePython)
  n = 1
  ref = He_element
FEATURE [App::DocumentObjectGroupPython] G4_He  # scripted group (container) (typed FeaturePython)
  Dunit = g/cm3
  Dvalue = 0.000166322
  Group = -> [He_element001]
  conduct = 2
  density = 1
  expand = 3
  formula = He
  name = G4_He
  specific = 4
FEATURE [App::DocumentObjectGroupPython] Li_element008  label="Li_element : 008"  # scripted group (container) (typed FeaturePython)
  n = 1
  ref = Li_element
FEATURE [App::DocumentObjectGroupPython] G4_Li  # scripted group (container) (typed FeaturePython)
  Dunit = g/cm3
  Dvalue = 0.534
  Group = -> [Li_element008]
  conduct = 2
  density = 1
  expand = 3
  formula = Li
  name = G4_Li
  specific = 4
FEATURE [App::DocumentObjectGroupPython] Be_element002  label="Be_element : 002"  # scripted group (container) (typed FeaturePython)
  n = 1
  ref = Be_element
FEATURE [App::DocumentObjectGroupPython] G4_Be  # scripted group (container) (typed FeaturePython)
  Dunit = g/cm3
  Dvalue = 1.848
  Group = -> [Be_element002]
  conduct = 2
  density = 1
  expand = 3
  formula = Be
  name = G4_Be
  specific = 4
FEATURE [App::DocumentObjectGroupPython] B_element007  label="B_element : 007"  # scripted group (container) (typed FeaturePython)
  n = 1
  ref = B_element
FEATURE [App::DocumentObjectGroupPython] G4_B  # scripted group (container) (typed FeaturePython)
  Dunit = g/cm3
  Dvalue = 2.37
  Group = -> [B_element007]
  conduct = 2
  density = 1
  expand = 3
  formula = B
  name = G4_B
  specific = 4
FEATURE [App::DocumentObjectGroupPython] C_element124  label="C_element : 070"  # scripted group (container) (typed FeaturePython)
  n = 1
  ref = C_element
FEATURE [App::DocumentObjectGroupPython] G4_C  # scripted group (container) (typed FeaturePython)
  Dunit = g/cm3
  Dvalue = 2
  Group = -> [C_element124]
  conduct = 2
  density = 1
  expand = 3
  formula = C
  name = G4_C
  specific = 4
FEATURE [App::DocumentObjectGroupPython] N_element048  label="N_element : 021"  # scripted group (container) (typed FeaturePython)
  n = 1
  ref = N_element
FEATURE [App::DocumentObjectGroupPython] G4_N  # scripted group (container) (typed FeaturePython)
  Dunit = g/cm3
  Dvalue = 0.0011652
  Group = -> [N_element048]
  conduct = 2
  density = 1
  expand = 3
  formula = N
  name = G4_N
  specific = 4
FEATURE [App::DocumentObjectGroupPython] O_element105  label="O_element : 059"  # scripted group (container) (typed FeaturePython)
  n = 1
  ref = O_element
FEATURE [App::DocumentObjectGroupPython] G4_O  # scripted group (container) (typed FeaturePython)
  Dunit = g/cm3
  Dvalue = 0.00133151
  Group = -> [O_element105]
  conduct = 2
  density = 1
  expand = 3
  formula = O
  name = G4_O
  specific = 4
FEATURE [App::DocumentObjectGroupPython] F_element019  label="F_element : 008"  # scripted group (container) (typed FeaturePython)
  n = 1
  ref = F_element
FEATURE [App::DocumentObjectGroupPython] G4_F  # scripted group (container) (typed FeaturePython)
  Dunit = g/cm3
  Dvalue = 0.00158029
  Group = -> [F_element019]
  conduct = 2
  density = 1
  expand = 3
  formula = F
  name = G4_F
  specific = 4
FEATURE [App::DocumentObjectGroupPython] Ne_element001  label="Ne_element : 1"  # scripted group (container) (typed FeaturePython)
  n = 1
  ref = Ne_element
FEATURE [App::DocumentObjectGroupPython] G4_Ne  # scripted group (container) (typed FeaturePython)
  Dunit = g/cm3
  Dvalue = 0.000838505
  Group = -> [Ne_element001]
  conduct = 2
  density = 1
  expand = 3
  formula = Ne
  name = G4_Ne
  specific = 4
FEATURE [App::DocumentObjectGroupPython] Na_element020  label="Na_element : 005"  # scripted group (container) (typed FeaturePython)
  n = 1
  ref = Na_element
FEATURE [App::DocumentObjectGroupPython] G4_Na  # scripted group (container) (typed FeaturePython)
  Dunit = g/cm3
  Dvalue = 0.971
  Group = -> [Na_element020]
  conduct = 2
  density = 1
  expand = 3
  formula = Na
  name = G4_Na
  specific = 4
FEATURE [App::DocumentObjectGroupPython] Mg_element011  label="Mg_element : 005"  # scripted group (container) (typed FeaturePython)
  n = 1
  ref = Mg_element
FEATURE [App::DocumentObjectGroupPython] G4_Mg  # scripted group (container) (typed FeaturePython)
  Dunit = g/cm3
  Dvalue = 1.74
  Group = -> [Mg_element011]
  conduct = 2
  density = 1
  expand = 3
  formula = Mg
  name = G4_Mg
  specific = 4
FEATURE [App::DocumentObjectGroupPython] Al_element004  label="Al_element : 1"  # scripted group (container) (typed FeaturePython)
  n = 1
  ref = Al_element
FEATURE [App::DocumentObjectGroupPython] G4_Al  # scripted group (container) (typed FeaturePython)
  Dunit = g/cm3
  Dvalue = 2.699
  Group = -> [Al_element004]
  conduct = 2
  density = 1
  expand = 3
  formula = Al
  name = G4_Al
  specific = 4
FEATURE [App::DocumentObjectGroupPython] Si_element007  label="Si_element : 002"  # scripted group (container) (typed FeaturePython)
  n = 1
  ref = Si_element
FEATURE [App::DocumentObjectGroupPython] G4_Si  # scripted group (container) (typed FeaturePython)
  Dunit = g/cm3
  Dvalue = 2.33
  Group = -> [Si_element007]
  conduct = 2
  density = 1
  expand = 3
  formula = Si
  name = G4_Si
  specific = 4
FEATURE [App::DocumentObjectGroupPython] P_element013  label="P_element : 002"  # scripted group (container) (typed FeaturePython)
  n = 1
  ref = P_element
FEATURE [App::DocumentObjectGroupPython] G4_P  # scripted group (container) (typed FeaturePython)
  Dunit = g/cm3
  Dvalue = 2.2
  Group = -> [P_element013]
  conduct = 2
  density = 1
  expand = 3
  formula = P
  name = G4_P
  specific = 4
FEATURE [App::DocumentObjectGroupPython] S_element023  label="S_element : 007"  # scripted group (container) (typed FeaturePython)
  n = 1
  ref = S_element
FEATURE [App::DocumentObjectGroupPython] G4_S  # scripted group (container) (typed FeaturePython)
  Dunit = g/cm3
  Dvalue = 2
  Group = -> [S_element023]
  conduct = 2
  density = 1
  expand = 3
  formula = S
  name = G4_S
  specific = 4
FEATURE [App::DocumentObjectGroupPython] Cl_element029  label="Cl_element : 015"  # scripted group (container) (typed FeaturePython)
  n = 1
  ref = Cl_element
FEATURE [App::DocumentObjectGroupPython] G4_Cl  # scripted group (container) (typed FeaturePython)
  Dunit = g/cm3
  Dvalue = 0.00299473
  Group = -> [Cl_element029]
  conduct = 2
  density = 1
  expand = 3
  formula = Cl
  name = G4_Cl
  specific = 4
FEATURE [App::DocumentObjectGroupPython] Ar_element002  label="Ar_element : 1"  # scripted group (container) (typed FeaturePython)
  n = 1
  ref = Ar_element
FEATURE [App::DocumentObjectGroupPython] G4_Ar  # scripted group (container) (typed FeaturePython)
  Dunit = g/cm3
  Dvalue = 0.00166201
  Group = -> [Ar_element002]
  conduct = 2
  density = 1
  expand = 3
  formula = Ar
  name = G4_Ar
  specific = 4
FEATURE [App::DocumentObjectGroupPython] K_element013  label="K_element : 003"  # scripted group (container) (typed FeaturePython)
  n = 1
  ref = K_element
FEATURE [App::DocumentObjectGroupPython] G4_K  # scripted group (container) (typed FeaturePython)
  Dunit = g/cm3
  Dvalue = 0.862
  Group = -> [K_element013]
  conduct = 2
  density = 1
  expand = 3
  formula = K
  name = G4_K
  specific = 4
FEATURE [App::DocumentObjectGroupPython] Ca_element014  label="Ca_element : 007"  # scripted group (container) (typed FeaturePython)
  n = 1
  ref = Ca_element
FEATURE [App::DocumentObjectGroupPython] G4_Ca  # scripted group (container) (typed FeaturePython)
  Dunit = g/cm3
  Dvalue = 1.55
  Group = -> [Ca_element014]
  conduct = 2
  density = 1
  expand = 3
  formula = Ca
  name = G4_Ca
  specific = 4
FEATURE [App::DocumentObjectGroupPython] Sc_element001  label="Sc_element : 1"  # scripted group (container) (typed FeaturePython)
  n = 1
  ref = Sc_element
FEATURE [App::DocumentObjectGroupPython] G4_Sc  # scripted group (container) (typed FeaturePython)
  Dunit = g/cm3
  Dvalue = 2.989
  Group = -> [Sc_element001]
  conduct = 2
  density = 1
  expand = 3
  formula = Sc
  name = G4_Sc
  specific = 4
FEATURE [App::DocumentObjectGroupPython] Ti_element004  label="Ti_element : 002"  # scripted group (container) (typed FeaturePython)
  n = 1
  ref = Ti_element
FEATURE [App::DocumentObjectGroupPython] G4_Ti  # scripted group (container) (typed FeaturePython)
  Dunit = g/cm3
  Dvalue = 4.54
  Group = -> [Ti_element004]
  conduct = 2
  density = 1
  expand = 3
  formula = Ti
  name = G4_Ti
  specific = 4
FEATURE [App::DocumentObjectGroupPython] V_element001  label="V_element : 1"  # scripted group (container) (typed FeaturePython)
  n = 1
  ref = V_element
FEATURE [App::DocumentObjectGroupPython] G4_V  # scripted group (container) (typed FeaturePython)
  Dunit = g/cm3
  Dvalue = 6.11
  Group = -> [V_element001]
  conduct = 2
  density = 1
  expand = 3
  formula = V
  name = G4_V
  specific = 4
FEATURE [App::DocumentObjectGroupPython] Cr_element001  label="Cr_element : 1"  # scripted group (container) (typed FeaturePython)
  n = 1
  ref = Cr_element
FEATURE [App::DocumentObjectGroupPython] G4_Cr  # scripted group (container) (typed FeaturePython)
  Dunit = g/cm3
  Dvalue = 7.18
  Group = -> [Cr_element001]
  conduct = 2
  density = 1
  expand = 3
  formula = Cr
  name = G4_Cr
  specific = 4
FEATURE [App::DocumentObjectGroupPython] Mn_element001  label="Mn_element : 1"  # scripted group (container) (typed FeaturePython)
  n = 1
  ref = Mn_element
FEATURE [App::DocumentObjectGroupPython] G4_Mn  # scripted group (container) (typed FeaturePython)
  Dunit = g/cm3
  Dvalue = 7.44
  Group = -> [Mn_element001]
  conduct = 2
  density = 1
  expand = 3
  formula = Mn
  name = G4_Mn
  specific = 4
FEATURE [App::DocumentObjectGroupPython] Fe_element007  label="Fe_element : 004"  # scripted group (container) (typed FeaturePython)
  n = 1
  ref = Fe_element
FEATURE [App::DocumentObjectGroupPython] G4_Fe  # scripted group (container) (typed FeaturePython)
  Dunit = g/cm3
  Dvalue = 7.874
  Group = -> [Fe_element007]
  conduct = 2
  density = 1
  expand = 3
  formula = Fe
  name = G4_Fe
  specific = 4
FEATURE [App::DocumentObjectGroupPython] Co_element001  label="Co_element : 1"  # scripted group (container) (typed FeaturePython)
  n = 1
  ref = Co_element
FEATURE [App::DocumentObjectGroupPython] G4_Co  # scripted group (container) (typed FeaturePython)
  Dunit = g/cm3
  Dvalue = 8.9
  Group = -> [Co_element001]
  conduct = 2
  density = 1
  expand = 3
  formula = Co
  name = G4_Co
  specific = 4
FEATURE [App::DocumentObjectGroupPython] Ni_element001  label="Ni_element : 1"  # scripted group (container) (typed FeaturePython)
  n = 1
  ref = Ni_element
FEATURE [App::DocumentObjectGroupPython] G4_Ni  # scripted group (container) (typed FeaturePython)
  Dunit = g/cm3
  Dvalue = 8.902
  Group = -> [Ni_element001]
  conduct = 2
  density = 1
  expand = 3
  formula = Ni
  name = G4_Ni
  specific = 4
FEATURE [App::DocumentObjectGroupPython] Cu_element001  label="Cu_element : 1"  # scripted group (container) (typed FeaturePython)
  n = 1
  ref = Cu_element
FEATURE [App::DocumentObjectGroupPython] G4_Cu  # scripted group (container) (typed FeaturePython)
  Dunit = g/cm3
  Dvalue = 8.96
  Group = -> [Cu_element001]
  conduct = 2
  density = 1
  expand = 3
  formula = Cu
  name = G4_Cu
  specific = 4
FEATURE [App::DocumentObjectGroupPython] Zn_element001  label="Zn_element : 1"  # scripted group (container) (typed FeaturePython)
  n = 1
  ref = Zn_element
FEATURE [App::DocumentObjectGroupPython] G4_Zn  # scripted group (container) (typed FeaturePython)
  Dunit = g/cm3
  Dvalue = 7.133
  Group = -> [Zn_element001]
  conduct = 2
  density = 1
  expand = 3
  formula = Zn
  name = G4_Zn
  specific = 4
FEATURE [App::DocumentObjectGroupPython] Ga_element002  label="Ga_element : 002"  # scripted group (container) (typed FeaturePython)
  n = 1
  ref = Ga_element
FEATURE [App::DocumentObjectGroupPython] G4_Ga  # scripted group (container) (typed FeaturePython)
  Dunit = g/cm3
  Dvalue = 5.904
  Group = -> [Ga_element002]
  conduct = 2
  density = 1
  expand = 3
  formula = Ga
  name = G4_Ga
  specific = 4
FEATURE [App::DocumentObjectGroupPython] Ge_element002  label="Ge_element : 1"  # scripted group (container) (typed FeaturePython)
  n = 1
  ref = Ge_element
FEATURE [App::DocumentObjectGroupPython] G4_Ge  # scripted group (container) (typed FeaturePython)
  Dunit = g/cm3
  Dvalue = 5.323
  Group = -> [Ge_element002]
  conduct = 2
  density = 1
  expand = 3
  formula = Ge
  name = G4_Ge
  specific = 4
FEATURE [App::DocumentObjectGroupPython] As_element003  label="As_element : 002"  # scripted group (container) (typed FeaturePython)
  n = 1
  ref = As_element
FEATURE [App::DocumentObjectGroupPython] G4_As  # scripted group (container) (typed FeaturePython)
  Dunit = g/cm3
  Dvalue = 5.73
  Group = -> [As_element003]
  conduct = 2
  density = 1
  expand = 3
  formula = As
  name = G4_As
  specific = 4
FEATURE [App::DocumentObjectGroupPython] Se_element001  label="Se_element : 1"  # scripted group (container) (typed FeaturePython)
  n = 1
  ref = Se_element
FEATURE [App::DocumentObjectGroupPython] G4_Se  # scripted group (container) (typed FeaturePython)
  Dunit = g/cm3
  Dvalue = 4.5
  Group = -> [Se_element001]
  conduct = 2
  density = 1
  expand = 3
  formula = Se
  name = G4_Se
  specific = 4
FEATURE [App::DocumentObjectGroupPython] Br_element007  label="Br_element : 004"  # scripted group (container) (typed FeaturePython)
  n = 1
  ref = Br_element
FEATURE [App::DocumentObjectGroupPython] G4_Br  # scripted group (container) (typed FeaturePython)
  Dunit = g/cm3
  Dvalue = 0.0070721
  Group = -> [Br_element007]
  conduct = 2
  density = 1
  expand = 3
  formula = Br
  name = G4_Br
  specific = 4
FEATURE [App::DocumentObjectGroupPython] Kr_element001  label="Kr_element : 1"  # scripted group (container) (typed FeaturePython)
  n = 1
  ref = Kr_element
FEATURE [App::DocumentObjectGroupPython] G4_Kr  # scripted group (container) (typed FeaturePython)
  Dunit = g/cm3
  Dvalue = 0.00347832
  Group = -> [Kr_element001]
  conduct = 2
  density = 1
  expand = 3
  formula = Kr
  name = G4_Kr
  specific = 4
FEATURE [App::DocumentObjectGroupPython] Rb_element001  label="Rb_element : 1"  # scripted group (container) (typed FeaturePython)
  n = 1
  ref = Rb_element
FEATURE [App::DocumentObjectGroupPython] G4_Rb  # scripted group (container) (typed FeaturePython)
  Dunit = g/cm3
  Dvalue = 1.532
  Group = -> [Rb_element001]
  conduct = 2
  density = 1
  expand = 3
  formula = Rb
  name = G4_Rb
  specific = 4
FEATURE [App::DocumentObjectGroupPython] Sr_element001  label="Sr_element : 1"  # scripted group (container) (typed FeaturePython)
  n = 1
  ref = Sr_element
FEATURE [App::DocumentObjectGroupPython] G4_Sr  # scripted group (container) (typed FeaturePython)
  Dunit = g/cm3
  Dvalue = 2.54
  Group = -> [Sr_element001]
  conduct = 2
  density = 1
  expand = 3
  formula = Sr
  name = G4_Sr
  specific = 4
FEATURE [App::DocumentObjectGroupPython] Y_element001  label="Y_element : 1"  # scripted group (container) (typed FeaturePython)
  n = 1
  ref = Y_element
FEATURE [App::DocumentObjectGroupPython] G4_Y  # scripted group (container) (typed FeaturePython)
  Dunit = g/cm3
  Dvalue = 4.469
  Group = -> [Y_element001]
  conduct = 2
  density = 1
  expand = 3
  formula = Y
  name = G4_Y
  specific = 4
FEATURE [App::DocumentObjectGroupPython] Zr_element001  label="Zr_element : 1"  # scripted group (container) (typed FeaturePython)
  n = 1
  ref = Zr_element
FEATURE [App::DocumentObjectGroupPython] G4_Zr  # scripted group (container) (typed FeaturePython)
  Dunit = g/cm3
  Dvalue = 6.506
  Group = -> [Zr_element001]
  conduct = 2
  density = 1
  expand = 3
  formula = Zr
  name = G4_Zr
  specific = 4
FEATURE [App::DocumentObjectGroupPython] Nb_element001  label="Nb_element : 1"  # scripted group (container) (typed FeaturePython)
  n = 1
  ref = Nb_element
FEATURE [App::DocumentObjectGroupPython] G4_Nb  # scripted group (container) (typed FeaturePython)
  Dunit = g/cm3
  Dvalue = 8.57
  Group = -> [Nb_element001]
  conduct = 2
  density = 1
  expand = 3
  formula = Nb
  name = G4_Nb
  specific = 4
FEATURE [App::DocumentObjectGroupPython] Mo_element001  label="Mo_element : 1"  # scripted group (container) (typed FeaturePython)
  n = 1
  ref = Mo_element
FEATURE [App::DocumentObjectGroupPython] G4_Mo  # scripted group (container) (typed FeaturePython)
  Dunit = g/cm3
  Dvalue = 10.22
  Group = -> [Mo_element001]
  conduct = 2
  density = 1
  expand = 3
  formula = Mo
  name = G4_Mo
  specific = 4
FEATURE [App::DocumentObjectGroupPython] Tc_element001  label="Tc_element : 1"  # scripted group (container) (typed FeaturePython)
  n = 1
  ref = Tc_element
FEATURE [App::DocumentObjectGroupPython] G4_Tc  # scripted group (container) (typed FeaturePython)
  Dunit = g/cm3
  Dvalue = 11.5
  Group = -> [Tc_element001]
  conduct = 2
  density = 1
  expand = 3
  formula = Tc
  name = G4_Tc
  specific = 4
FEATURE [App::DocumentObjectGroupPython] Ru_element001  label="Ru_element : 1"  # scripted group (container) (typed FeaturePython)
  n = 1
  ref = Ru_element
FEATURE [App::DocumentObjectGroupPython] G4_Ru  # scripted group (container) (typed FeaturePython)
  Dunit = g/cm3
  Dvalue = 12.41
  Group = -> [Ru_element001]
  conduct = 2
  density = 1
  expand = 3
  formula = Ru
  name = G4_Ru
  specific = 4
FEATURE [App::DocumentObjectGroupPython] Rh_element001  label="Rh_element : 1"  # scripted group (container) (typed FeaturePython)
  n = 1
  ref = Rh_element
FEATURE [App::DocumentObjectGroupPython] G4_Rh  # scripted group (container) (typed FeaturePython)
  Dunit = g/cm3
  Dvalue = 12.41
  Group = -> [Rh_element001]
  conduct = 2
  density = 1
  expand = 3
  formula = Rh
  name = G4_Rh
  specific = 4
FEATURE [App::DocumentObjectGroupPython] Pd_element001  label="Pd_element : 1"  # scripted group (container) (typed FeaturePython)
  n = 1
  ref = Pd_element
FEATURE [App::DocumentObjectGroupPython] G4_Pd  # scripted group (container) (typed FeaturePython)
  Dunit = g/cm3
  Dvalue = 12.02
  Group = -> [Pd_element001]
  conduct = 2
  density = 1
  expand = 3
  formula = Pd
  name = G4_Pd
  specific = 4
FEATURE [App::DocumentObjectGroupPython] Ag_element006  label="Ag_element : 004"  # scripted group (container) (typed FeaturePython)
  n = 1
  ref = Ag_element
FEATURE [App::DocumentObjectGroupPython] G4_Ag  # scripted group (container) (typed FeaturePython)
  Dunit = g/cm3
  Dvalue = 10.5
  Group = -> [Ag_element006]
  conduct = 2
  density = 1
  expand = 3
  formula = Ag
  name = G4_Ag
  specific = 4
FEATURE [App::DocumentObjectGroupPython] Cd_element003  label="Cd_element : 003"  # scripted group (container) (typed FeaturePython)
  n = 1
  ref = Cd_element
FEATURE [App::DocumentObjectGroupPython] G4_Cd  # scripted group (container) (typed FeaturePython)
  Dunit = g/cm3
  Dvalue = 8.65
  Group = -> [Cd_element003]
  conduct = 2
  density = 1
  expand = 3
  formula = Cd
  name = G4_Cd
  specific = 4
FEATURE [App::DocumentObjectGroupPython] In_element001  label="In_element : 1"  # scripted group (container) (typed FeaturePython)
  n = 1
  ref = In_element
FEATURE [App::DocumentObjectGroupPython] G4_In  # scripted group (container) (typed FeaturePython)
  Dunit = g/cm3
  Dvalue = 7.31
  Group = -> [In_element001]
  conduct = 2
  density = 1
  expand = 3
  formula = In
  name = G4_In
  specific = 4
FEATURE [App::DocumentObjectGroupPython] Sn_element001  label="Sn_element : 1"  # scripted group (container) (typed FeaturePython)
  n = 1
  ref = Sn_element
FEATURE [App::DocumentObjectGroupPython] G4_Sn  # scripted group (container) (typed FeaturePython)
  Dunit = g/cm3
  Dvalue = 7.31
  Group = -> [Sn_element001]
  conduct = 2
  density = 1
  expand = 3
  formula = Sn
  name = G4_Sn
  specific = 4
FEATURE [App::DocumentObjectGroupPython] Sb_element001  label="Sb_element : 1"  # scripted group (container) (typed FeaturePython)
  n = 1
  ref = Sb_element
FEATURE [App::DocumentObjectGroupPython] G4_Sb  # scripted group (container) (typed FeaturePython)
  Dunit = g/cm3
  Dvalue = 6.691
  Group = -> [Sb_element001]
  conduct = 2
  density = 1
  expand = 3
  formula = Sb
  name = G4_Sb
  specific = 4
FEATURE [App::DocumentObjectGroupPython] Te_element002  label="Te_element : 002"  # scripted group (container) (typed FeaturePython)
  n = 1
  ref = Te_element
FEATURE [App::DocumentObjectGroupPython] G4_Te  # scripted group (container) (typed FeaturePython)
  Dunit = g/cm3
  Dvalue = 6.24
  Group = -> [Te_element002]
  conduct = 2
  density = 1
  expand = 3
  formula = Te
  name = G4_Te
  specific = 4
FEATURE [App::DocumentObjectGroupPython] I_element010  label="I_element : 006"  # scripted group (container) (typed FeaturePython)
  n = 1
  ref = I_element
FEATURE [App::DocumentObjectGroupPython] G4_I  # scripted group (container) (typed FeaturePython)
  Dunit = g/cm3
  Dvalue = 4.93
  Group = -> [I_element010]
  conduct = 2
  density = 1
  expand = 3
  formula = I
  name = G4_I
  specific = 4
FEATURE [App::DocumentObjectGroupPython] Xe_element001  label="Xe_element : 1"  # scripted group (container) (typed FeaturePython)
  n = 1
  ref = Xe_element
FEATURE [App::DocumentObjectGroupPython] G4_Xe  # scripted group (container) (typed FeaturePython)
  Dunit = g/cm3
  Dvalue = 0.00548536
  Group = -> [Xe_element001]
  conduct = 2
  density = 1
  expand = 3
  formula = Xe
  name = G4_Xe
  specific = 4
FEATURE [App::DocumentObjectGroupPython] Cs_element003  label="Cs_element : 003"  # scripted group (container) (typed FeaturePython)
  n = 1
  ref = Cs_element
FEATURE [App::DocumentObjectGroupPython] G4_Cs  # scripted group (container) (typed FeaturePython)
  Dunit = g/cm3
  Dvalue = 1.873
  Group = -> [Cs_element003]
  conduct = 2
  density = 1
  expand = 3
  formula = Cs
  name = G4_Cs
  specific = 4
FEATURE [App::DocumentObjectGroupPython] Ba_element003  label="Ba_element : 003"  # scripted group (container) (typed FeaturePython)
  n = 1
  ref = Ba_element
FEATURE [App::DocumentObjectGroupPython] G4_Ba  # scripted group (container) (typed FeaturePython)
  Dunit = g/cm3
  Dvalue = 3.5
  Group = -> [Ba_element003]
  conduct = 2
  density = 1
  expand = 3
  formula = Ba
  name = G4_Ba
  specific = 4
FEATURE [App::DocumentObjectGroupPython] La_element003  label="La_element : 003"  # scripted group (container) (typed FeaturePython)
  n = 1
  ref = La_element
FEATURE [App::DocumentObjectGroupPython] G4_La  # scripted group (container) (typed FeaturePython)
  Dunit = g/cm3
  Dvalue = 6.154
  Group = -> [La_element003]
  conduct = 2
  density = 1
  expand = 3
  formula = La
  name = G4_La
  specific = 4
FEATURE [App::DocumentObjectGroupPython] Ce_element002  label="Ce_element : 1"  # scripted group (container) (typed FeaturePython)
  n = 1
  ref = Ce_element
FEATURE [App::DocumentObjectGroupPython] G4_Ce  # scripted group (container) (typed FeaturePython)
  Dunit = g/cm3
  Dvalue = 6.657
  Group = -> [Ce_element002]
  conduct = 2
  density = 1
  expand = 3
  formula = Ce
  name = G4_Ce
  specific = 4
FEATURE [App::DocumentObjectGroupPython] Pr_element001  label="Pr_element : 1"  # scripted group (container) (typed FeaturePython)
  n = 1
  ref = Pr_element
FEATURE [App::DocumentObjectGroupPython] G4_Pr  # scripted group (container) (typed FeaturePython)
  Dunit = g/cm3
  Dvalue = 6.71
  Group = -> [Pr_element001]
  conduct = 2
  density = 1
  expand = 3
  formula = Pr
  name = G4_Pr
  specific = 4
FEATURE [App::DocumentObjectGroupPython] Nd_element001  label="Nd_element : 1"  # scripted group (container) (typed FeaturePython)
  n = 1
  ref = Nd_element
FEATURE [App::DocumentObjectGroupPython] G4_Nd  # scripted group (container) (typed FeaturePython)
  Dunit = g/cm3
  Dvalue = 6.9
  Group = -> [Nd_element001]
  conduct = 2
  density = 1
  expand = 3
  formula = Nd
  name = G4_Nd
  specific = 4
FEATURE [App::DocumentObjectGroupPython] Pm_element001  label="Pm_element : 1"  # scripted group (container) (typed FeaturePython)
  n = 1
  ref = Pm_element
FEATURE [App::DocumentObjectGroupPython] G4_Pm  # scripted group (container) (typed FeaturePython)
  Dunit = g/cm3
  Dvalue = 7.22
  Group = -> [Pm_element001]
  conduct = 2
  density = 1
  expand = 3
  formula = Pm
  name = G4_Pm
  specific = 4
FEATURE [App::DocumentObjectGroupPython] Sm_element001  label="Sm_element : 1"  # scripted group (container) (typed FeaturePython)
  n = 1
  ref = Sm_element
FEATURE [App::DocumentObjectGroupPython] G4_Sm  # scripted group (container) (typed FeaturePython)
  Dunit = g/cm3
  Dvalue = 7.46
  Group = -> [Sm_element001]
  conduct = 2
  density = 1
  expand = 3
  formula = Sm
  name = G4_Sm
  specific = 4
FEATURE [App::DocumentObjectGroupPython] Eu_element001  label="Eu_element : 1"  # scripted group (container) (typed FeaturePython)
  n = 1
  ref = Eu_element
FEATURE [App::DocumentObjectGroupPython] G4_Eu  # scripted group (container) (typed FeaturePython)
  Dunit = g/cm3
  Dvalue = 5.243
  Group = -> [Eu_element001]
  conduct = 2
  density = 1
  expand = 3
  formula = Eu
  name = G4_Eu
  specific = 4
FEATURE [App::DocumentObjectGroupPython] Gd_element002  label="Gd_element : 1"  # scripted group (container) (typed FeaturePython)
  n = 1
  ref = Gd_element
FEATURE [App::DocumentObjectGroupPython] G4_Gd  # scripted group (container) (typed FeaturePython)
  Dunit = g/cm3
  Dvalue = 7.9004
  Group = -> [Gd_element002]
  conduct = 2
  density = 1
  expand = 3
  formula = Gd
  name = G4_Gd
  specific = 4
FEATURE [App::DocumentObjectGroupPython] Tb_element001  label="Tb_element : 1"  # scripted group (container) (typed FeaturePython)
  n = 1
  ref = Tb_element
FEATURE [App::DocumentObjectGroupPython] G4_Tb  # scripted group (container) (typed FeaturePython)
  Dunit = g/cm3
  Dvalue = 8.229
  Group = -> [Tb_element001]
  conduct = 2
  density = 1
  expand = 3
  formula = Tb
  name = G4_Tb
  specific = 4
FEATURE [App::DocumentObjectGroupPython] Dy_element001  label="Dy_element : 1"  # scripted group (container) (typed FeaturePython)
  n = 1
  ref = Dy_element
FEATURE [App::DocumentObjectGroupPython] G4_Dy  # scripted group (container) (typed FeaturePython)
  Dunit = g/cm3
  Dvalue = 8.55
  Group = -> [Dy_element001]
  conduct = 2
  density = 1
  expand = 3
  formula = Dy
  name = G4_Dy
  specific = 4
FEATURE [App::DocumentObjectGroupPython] Ho_element001  label="Ho_element : 1"  # scripted group (container) (typed FeaturePython)
  n = 1
  ref = Ho_element
FEATURE [App::DocumentObjectGroupPython] G4_Ho  # scripted group (container) (typed FeaturePython)
  Dunit = g/cm3
  Dvalue = 8.795
  Group = -> [Ho_element001]
  conduct = 2
  density = 1
  expand = 3
  formula = Ho
  name = G4_Ho
  specific = 4
FEATURE [App::DocumentObjectGroupPython] Er_element001  label="Er_element : 1"  # scripted group (container) (typed FeaturePython)
  n = 1
  ref = Er_element
FEATURE [App::DocumentObjectGroupPython] G4_Er  # scripted group (container) (typed FeaturePython)
  Dunit = g/cm3
  Dvalue = 9.066
  Group = -> [Er_element001]
  conduct = 2
  density = 1
  expand = 3
  formula = Er
  name = G4_Er
  specific = 4
FEATURE [App::DocumentObjectGroupPython] Tm_element001  label="Tm_element : 1"  # scripted group (container) (typed FeaturePython)
  n = 1
  ref = Tm_element
FEATURE [App::DocumentObjectGroupPython] G4_Tm  # scripted group (container) (typed FeaturePython)
  Dunit = g/cm3
  Dvalue = 9.321
  Group = -> [Tm_element001]
  conduct = 2
  density = 1
  expand = 3
  formula = Tm
  name = G4_Tm
  specific = 4
FEATURE [App::DocumentObjectGroupPython] Yb_element001  label="Yb_element : 1"  # scripted group (container) (typed FeaturePython)
  n = 1
  ref = Yb_element
FEATURE [App::DocumentObjectGroupPython] G4_Yb  # scripted group (container) (typed FeaturePython)
  Dunit = g/cm3
  Dvalue = 6.73
  Group = -> [Yb_element001]
  conduct = 2
  density = 1
  expand = 3
  formula = Yb
  name = G4_Yb
  specific = 4
FEATURE [App::DocumentObjectGroupPython] Lu_element001  label="Lu_element : 1"  # scripted group (container) (typed FeaturePython)
  n = 1
  ref = Lu_element
FEATURE [App::DocumentObjectGroupPython] G4_Lu  # scripted group (container) (typed FeaturePython)
  Dunit = g/cm3
  Dvalue = 9.84
  Group = -> [Lu_element001]
  conduct = 2
  density = 1
  expand = 3
  formula = Lu
  name = G4_Lu
  specific = 4
FEATURE [App::DocumentObjectGroupPython] Hf_element001  label="Hf_element : 1"  # scripted group (container) (typed FeaturePython)
  n = 1
  ref = Hf_element
FEATURE [App::DocumentObjectGroupPython] G4_Hf  # scripted group (container) (typed FeaturePython)
  Dunit = g/cm3
  Dvalue = 13.31
  Group = -> [Hf_element001]
  conduct = 2
  density = 1
  expand = 3
  formula = Hf
  name = G4_Hf
  specific = 4
FEATURE [App::DocumentObjectGroupPython] Ta_element001  label="Ta_element : 1"  # scripted group (container) (typed FeaturePython)
  n = 1
  ref = Ta_element
FEATURE [App::DocumentObjectGroupPython] G4_Ta  # scripted group (container) (typed FeaturePython)
  Dunit = g/cm3
  Dvalue = 16.654
  Group = -> [Ta_element001]
  conduct = 2
  density = 1
  expand = 3
  formula = Ta
  name = G4_Ta
  specific = 4
FEATURE [App::DocumentObjectGroupPython] W_element004  label="W_element : 004"  # scripted group (container) (typed FeaturePython)
  n = 1
  ref = W_element
FEATURE [App::DocumentObjectGroupPython] G4_W  # scripted group (container) (typed FeaturePython)
  Dunit = g/cm3
  Dvalue = 19.3
  Group = -> [W_element004]
  conduct = 2
  density = 1
  expand = 3
  formula = W
  name = G4_W
  specific = 4
FEATURE [App::DocumentObjectGroupPython] Re_element001  label="Re_element : 1"  # scripted group (container) (typed FeaturePython)
  n = 1
  ref = Re_element
FEATURE [App::DocumentObjectGroupPython] G4_Re  # scripted group (container) (typed FeaturePython)
  Dunit = g/cm3
  Dvalue = 21.02
  Group = -> [Re_element001]
  conduct = 2
  density = 1
  expand = 3
  formula = Re
  name = G4_Re
  specific = 4
FEATURE [App::DocumentObjectGroupPython] Os_element001  label="Os_element : 1"  # scripted group (container) (typed FeaturePython)
  n = 1
  ref = Os_element
FEATURE [App::DocumentObjectGroupPython] G4_Os  # scripted group (container) (typed FeaturePython)
  Dunit = g/cm3
  Dvalue = 22.57
  Group = -> [Os_element001]
  conduct = 2
  density = 1
  expand = 3
  formula = Os
  name = G4_Os
  specific = 4
FEATURE [App::DocumentObjectGroupPython] Ir_element001  label="Ir_element : 1"  # scripted group (container) (typed FeaturePython)
  n = 1
  ref = Ir_element
FEATURE [App::DocumentObjectGroupPython] G4_Ir  # scripted group (container) (typed FeaturePython)
  Dunit = g/cm3
  Dvalue = 22.42
  Group = -> [Ir_element001]
  conduct = 2
  density = 1
  expand = 3
  formula = Ir
  name = G4_Ir
  specific = 4
FEATURE [App::DocumentObjectGroupPython] Pt_element001  label="Pt_element : 1"  # scripted group (container) (typed FeaturePython)
  n = 1
  ref = Pt_element
FEATURE [App::DocumentObjectGroupPython] G4_Pt  # scripted group (container) (typed FeaturePython)
  Dunit = g/cm3
  Dvalue = 21.45
  Group = -> [Pt_element001]
  conduct = 2
  density = 1
  expand = 3
  formula = Pt
  name = G4_Pt
  specific = 4
FEATURE [App::DocumentObjectGroupPython] Au_element001  label="Au_element : 1"  # scripted group (container) (typed FeaturePython)
  n = 1
  ref = Au_element
FEATURE [App::DocumentObjectGroupPython] G4_Au  # scripted group (container) (typed FeaturePython)
  Dunit = g/cm3
  Dvalue = 19.32
  Group = -> [Au_element001]
  conduct = 2
  density = 1
  expand = 3
  formula = Au
  name = G4_Au
  specific = 4
FEATURE [App::DocumentObjectGroupPython] Hg_element002  label="Hg_element : 002"  # scripted group (container) (typed FeaturePython)
  n = 1
  ref = Hg_element
FEATURE [App::DocumentObjectGroupPython] G4_Hg  # scripted group (container) (typed FeaturePython)
  Dunit = g/cm3
  Dvalue = 13.546
  Group = -> [Hg_element002]
  conduct = 2
  density = 1
  expand = 3
  formula = Hg
  name = G4_Hg
  specific = 4
FEATURE [App::DocumentObjectGroupPython] Tl_element002  label="Tl_element : 002"  # scripted group (container) (typed FeaturePython)
  n = 1
  ref = Tl_element
FEATURE [App::DocumentObjectGroupPython] G4_Tl  # scripted group (container) (typed FeaturePython)
  Dunit = g/cm3
  Dvalue = 11.72
  Group = -> [Tl_element002]
  conduct = 2
  density = 1
  expand = 3
  formula = Tl
  name = G4_Tl
  specific = 4
FEATURE [App::DocumentObjectGroupPython] Pb_element003  label="Pb_element : 1"  # scripted group (container) (typed FeaturePython)
  n = 1
  ref = Pb_element
FEATURE [App::DocumentObjectGroupPython] G4_Pb  # scripted group (container) (typed FeaturePython)
  Dunit = g/cm3
  Dvalue = 11.35
  Group = -> [Pb_element003]
  conduct = 2
  density = 1
  expand = 3
  formula = Pb
  name = G4_Pb
  specific = 4
FEATURE [App::DocumentObjectGroupPython] Bi_element002  label="Bi_element : 1"  # scripted group (container) (typed FeaturePython)
  n = 1
  ref = Bi_element
FEATURE [App::DocumentObjectGroupPython] G4_Bi  # scripted group (container) (typed FeaturePython)
  Dunit = g/cm3
  Dvalue = 9.747
  Group = -> [Bi_element002]
  conduct = 2
  density = 1
  expand = 3
  formula = Bi
  name = G4_Bi
  specific = 4
FEATURE [App::DocumentObjectGroupPython] Po_element001  label="Po_element : 1"  # scripted group (container) (typed FeaturePython)
  n = 1
  ref = Po_element
FEATURE [App::DocumentObjectGroupPython] G4_Po  # scripted group (container) (typed FeaturePython)
  Dunit = g/cm3
  Dvalue = 9.32
  Group = -> [Po_element001]
  conduct = 2
  density = 1
  expand = 3
  formula = Po
  name = G4_Po
  specific = 4
FEATURE [App::DocumentObjectGroupPython] At_element001  label="At_element : 1"  # scripted group (container) (typed FeaturePython)
  n = 1
  ref = At_element
FEATURE [App::DocumentObjectGroupPython] G4_At  # scripted group (container) (typed FeaturePython)
  Dunit = g/cm3
  Dvalue = 9.32
  Group = -> [At_element001]
  conduct = 2
  density = 1
  expand = 3
  formula = At
  name = G4_At
  specific = 4
FEATURE [App::DocumentObjectGroupPython] Rn_element001  label="Rn_element : 1"  # scripted group (container) (typed FeaturePython)
  n = 1
  ref = Rn_element
FEATURE [App::DocumentObjectGroupPython] G4_Rn  # scripted group (container) (typed FeaturePython)
  Dunit = g/cm3
  Dvalue = 0.00900662
  Group = -> [Rn_element001]
  conduct = 2
  density = 1
  expand = 3
  formula = Rn
  name = G4_Rn
  specific = 4
FEATURE [App::DocumentObjectGroupPython] Fr_element001  label="Fr_element : 1"  # scripted group (container) (typed FeaturePython)
  n = 1
  ref = Fr_element
FEATURE [App::DocumentObjectGroupPython] G4_Fr  # scripted group (container) (typed FeaturePython)
  Dunit = g/cm3
  Dvalue = 1
  Group = -> [Fr_element001]
  conduct = 2
  density = 1
  expand = 3
  formula = Fr
  name = G4_Fr
  specific = 4
FEATURE [App::DocumentObjectGroupPython] Ra_element001  label="Ra_element : 1"  # scripted group (container) (typed FeaturePython)
  n = 1
  ref = Ra_element
FEATURE [App::DocumentObjectGroupPython] G4_Ra  # scripted group (container) (typed FeaturePython)
  Dunit = g/cm3
  Dvalue = 5
  Group = -> [Ra_element001]
  conduct = 2
  density = 1
  expand = 3
  formula = Ra
  name = G4_Ra
  specific = 4
FEATURE [App::DocumentObjectGroupPython] Ac_element001  label="Ac_element : 1"  # scripted group (container) (typed FeaturePython)
  n = 1
  ref = Ac_element
FEATURE [App::DocumentObjectGroupPython] G4_Ac  # scripted group (container) (typed FeaturePython)
  Dunit = g/cm3
  Dvalue = 10.07
  Group = -> [Ac_element001]
  conduct = 2
  density = 1
  expand = 3
  formula = Ac
  name = G4_Ac
  specific = 4
FEATURE [App::DocumentObjectGroupPython] Th_element001  label="Th_element : 1"  # scripted group (container) (typed FeaturePython)
  n = 1
  ref = Th_element
FEATURE [App::DocumentObjectGroupPython] G4_Th  # scripted group (container) (typed FeaturePython)
  Dunit = g/cm3
  Dvalue = 11.72
  Group = -> [Th_element001]
  conduct = 2
  density = 1
  expand = 3
  formula = Th
  name = G4_Th
  specific = 4
FEATURE [App::DocumentObjectGroupPython] Pa_element001  label="Pa_element : 1"  # scripted group (container) (typed FeaturePython)
  n = 1
  ref = Pa_element
FEATURE [App::DocumentObjectGroupPython] G4_Pa  # scripted group (container) (typed FeaturePython)
  Dunit = g/cm3
  Dvalue = 15.37
  Group = -> [Pa_element001]
  conduct = 2
  density = 1
  expand = 3
  formula = Pa
  name = G4_Pa
  specific = 4
FEATURE [App::DocumentObjectGroupPython] U_element004  label="U_element : 004"  # scripted group (container) (typed FeaturePython)
  n = 1
  ref = U_element
FEATURE [App::DocumentObjectGroupPython] G4_U  # scripted group (container) (typed FeaturePython)
  Dunit = g/cm3
  Dvalue = 18.95
  Group = -> [U_element004]
  conduct = 2
  density = 1
  expand = 3
  formula = U
  name = G4_U
  specific = 4
FEATURE [App::DocumentObjectGroupPython] Np_element001  label="Np_element : 1"  # scripted group (container) (typed FeaturePython)
  n = 1
  ref = Np_element
FEATURE [App::DocumentObjectGroupPython] G4_Np  # scripted group (container) (typed FeaturePython)
  Dunit = g/cm3
  Dvalue = 20.25
  Group = -> [Np_element001]
  conduct = 2
  density = 1
  expand = 3
  formula = Np
  name = G4_Np
  specific = 4
FEATURE [App::DocumentObjectGroupPython] Pu_element002  label="Pu_element : 002"  # scripted group (container) (typed FeaturePython)
  n = 1
  ref = Pu_element
FEATURE [App::DocumentObjectGroupPython] G4_Pu  # scripted group (container) (typed FeaturePython)
  Dunit = g/cm3
  Dvalue = 19.84
  Group = -> [Pu_element002]
  conduct = 2
  density = 1
  expand = 3
  formula = Pu
  name = G4_Pu
  specific = 4
FEATURE [App::DocumentObjectGroupPython] Am_element001  label="Am_element : 1"  # scripted group (container) (typed FeaturePython)
  n = 1
  ref = Am_element
FEATURE [App::DocumentObjectGroupPython] G4_Am  # scripted group (container) (typed FeaturePython)
  Dunit = g/cm3
  Dvalue = 13.67
  Group = -> [Am_element001]
  conduct = 2
  density = 1
  expand = 3
  formula = Am
  name = G4_Am
  specific = 4
FEATURE [App::DocumentObjectGroupPython] Cm_element001  label="Cm_element : 1"  # scripted group (container) (typed FeaturePython)
  n = 1
  ref = Cm_element
FEATURE [App::DocumentObjectGroupPython] G4_Cm  # scripted group (container) (typed FeaturePython)
  Dunit = g/cm3
  Dvalue = 13.51
  Group = -> [Cm_element001]
  conduct = 2
  density = 1
  expand = 3
  formula = Cm
  name = G4_Cm
  specific = 4
FEATURE [App::DocumentObjectGroupPython] Bk_element001  label="Bk_element : 1"  # scripted group (container) (typed FeaturePython)
  n = 1
  ref = Bk_element
FEATURE [App::DocumentObjectGroupPython] G4_Bk  # scripted group (container) (typed FeaturePython)
  Dunit = g/cm3
  Dvalue = 14
  Group = -> [Bk_element001]
  conduct = 2
  density = 1
  expand = 3
  formula = Bk
  name = G4_Bk
  specific = 4
FEATURE [App::DocumentObjectGroupPython] Cf_element001  label="Cf_element : 1"  # scripted group (container) (typed FeaturePython)
  n = 1
  ref = Cf_element
FEATURE [App::DocumentObjectGroupPython] G4_Cf  # scripted group (container) (typed FeaturePython)
  Dunit = g/cm3
  Dvalue = 10
  Group = -> [Cf_element001]
  conduct = 2
  density = 1
  expand = 3
  formula = Cf
  name = G4_Cf
  specific = 4
FEATURE [App::DocumentObjectGroupPython] Element  # scripted group (container) (typed FeaturePython)
  Group = -> [G4_H,G4_He,G4_Li,G4_Be,G4_B,G4_C,G4_N,G4_O,G4_F,G4_Ne,G4_Na,G4_Mg,G4_Al,G4_Si,G4_P,G4_S,G4_Cl,G4_Ar,G4_K,G4_Ca,G4_Sc,G4_Ti,G4_V,G4_Cr,G4_Mn,G4_Fe,G4_Co,G4_Ni,G4_Cu,G4_Zn,G4_Ga,G4_Ge,G4_As,G4_Se,G4_Br,G4_Kr,G4_Rb,G4_Sr,G4_Y,G4_Zr,G4_Nb,G4_Mo,G4_Tc,G4_Ru,G4_Rh,G4_Pd,G4_Ag,G4_Cd,G4_In,G4_Sn,G4_Sb,G4_Te,G4_I,G4_Xe,G4_Cs,G4_Ba,G4_La,G4_Ce,G4_Pr,G4_Nd,G4_Pm,G4_Sm,G4_Eu,G4_Gd,G4_Tb,G4_Dy,G4_Ho,G4_Er,+30 more]
FEATURE [App::DocumentObjectGroupPython] H_element114  label="H_element : 063"  # scripted group (container) (typed FeaturePython)
  n = 2
  ref = H_element
FEATURE [App::DocumentObjectGroupPython] G4_lH2  # scripted group (container) (typed FeaturePython)
  Dunit = g/cm3
  Dvalue = 0.0708
  Group = -> [H_element114]
  conduct = 2
  density = 1
  expand = 3
  formula = G4_lH2
  name = G4_lH2
  specific = 4
FEATURE [App::DocumentObjectGroupPython] N_element049  label="N_element : 022"  # scripted group (container) (typed FeaturePython)
  n = 2
  ref = N_element
FEATURE [App::DocumentObjectGroupPython] G4_lN2  # scripted group (container) (typed FeaturePython)
  Dunit = g/cm3
  Dvalue = 0.807
  Group = -> [N_element049]
  conduct = 2
  density = 1
  expand = 3
  formula = G4_lN2
  name = G4_lN2
  specific = 4
FEATURE [App::DocumentObjectGroupPython] O_element106  label="O_element : 060"  # scripted group (container) (typed FeaturePython)
  n = 2
  ref = O_element
FEATURE [App::DocumentObjectGroupPython] G4_lO2  # scripted group (container) (typed FeaturePython)
  Dunit = g/cm3
  Dvalue = 1.141
  Group = -> [O_element106]
  conduct = 2
  density = 1
  expand = 3
  formula = G4_lO2
  name = G4_lO2
  specific = 4
FEATURE [App::DocumentObjectGroupPython] Ar_element003  label="Ar_element : 002"  # scripted group (container) (typed FeaturePython)
  n = 1
  ref = Ar_element
FEATURE [App::DocumentObjectGroupPython] G4_lAr  # scripted group (container) (typed FeaturePython)
  Dunit = g/cm3
  Dvalue = 1.396
  Group = -> [Ar_element003]
  conduct = 2
  density = 1
  expand = 3
  formula = G4_lAr
  name = G4_lAr
  specific = 4
FEATURE [App::DocumentObjectGroupPython] Br_element008  label="Br_element : 005"  # scripted group (container) (typed FeaturePython)
  n = 1
  ref = Br_element
FEATURE [App::DocumentObjectGroupPython] G4_lBr  # scripted group (container) (typed FeaturePython)
  Dunit = g/cm3
  Dvalue = 3.1028
  Group = -> [Br_element008]
  conduct = 2
  density = 1
  expand = 3
  formula = G4_lBr
  name = G4_lBr
  specific = 4
FEATURE [App::DocumentObjectGroupPython] Kr_element002  label="Kr_element : 002"  # scripted group (container) (typed FeaturePython)
  n = 1
  ref = Kr_element
FEATURE [App::DocumentObjectGroupPython] G4_lKr  # scripted group (container) (typed FeaturePython)
  Dunit = g/cm3
  Dvalue = 2.418
  Group = -> [Kr_element002]
  conduct = 2
  density = 1
  expand = 3
  formula = G4_lKr
  name = G4_lKr
  specific = 4
FEATURE [App::DocumentObjectGroupPython] Xe_element002  label="Xe_element : 002"  # scripted group (container) (typed FeaturePython)
  n = 1
  ref = Xe_element
FEATURE [App::DocumentObjectGroupPython] G4_lXe  # scripted group (container) (typed FeaturePython)
  Dunit = g/cm3
  Dvalue = 2.953
  Group = -> [Xe_element002]
  conduct = 2
  density = 1
  expand = 3
  formula = G4_lXe
  name = G4_lXe
  specific = 4
FEATURE [App::DocumentObjectGroupPython] O_element107  label="O_element : 061"  # scripted group (container) (typed FeaturePython)
  n = 4
  ref = O_element
FEATURE [App::DocumentObjectGroupPython] Pb_element004  label="Pb_element : 002"  # scripted group (container) (typed FeaturePython)
  n = 1
  ref = Pb_element
FEATURE [App::DocumentObjectGroupPython] W_element005  label="W_element : 005"  # scripted group (container) (typed FeaturePython)
  n = 1
  ref = W_element
FEATURE [App::DocumentObjectGroupPython] G4_PbWO4  # scripted group (container) (typed FeaturePython)
  Dunit = g/cm3
  Dvalue = 8.28
  Group = -> [O_element107,Pb_element004,W_element005]
  conduct = 2
  density = 1
  expand = 3
  formula = G4_PbWO4
  name = G4_PbWO4
  specific = 4
FEATURE [App::DocumentObjectGroupPython] H_element115  label="H_element : 064"  # scripted group (container) (typed FeaturePython)
  n = 1
  ref = H_element
FEATURE [App::DocumentObjectGroupPython] G4_Galactic  # scripted group (container) (typed FeaturePython)
  Dunit = g/cm3
  Dvalue = 0
  Group = -> [H_element115]
  conduct = 2
  density = 1
  expand = 3
  formula = G4_Galactic
  name = G4_Galactic
  specific = 4
FEATURE [App::DocumentObjectGroupPython] C_element125  label="C_element : 071"  # scripted group (container) (typed FeaturePython)
  n = 1
  ref = C_element
FEATURE [App::DocumentObjectGroupPython] G4_GRAPHITE_POROUS  # scripted group (container) (typed FeaturePython)
  Dunit = g/cm3
  Dvalue = 1.7
  Group = -> [C_element125]
  conduct = 2
  density = 1
  expand = 3
  formula = G4_GRAPHITE_POROUS
  name = G4_GRAPHITE_POROUS
  specific = 4
FEATURE [App::DocumentObjectGroupPython] H_element116  label="H_element : 0.150"  # scripted group (container) (typed FeaturePython)
  n = 0.080538
FEATURE [App::DocumentObjectGroupPython] C_element126  label="C_element : 0.600"  # scripted group (container) (typed FeaturePython)
  n = 0.599848
FEATURE [App::DocumentObjectGroupPython] O_element108  label="O_element : 0.320"  # scripted group (container) (typed FeaturePython)
  n = 0.319614
FEATURE [App::DocumentObjectGroupPython] G4_LUCITE  # scripted group (container) (typed FeaturePython)
  Dunit = g/cm3
  Dvalue = 1.19
  Group = -> [H_element116,C_element126,O_element108]
  conduct = 2
  density = 1
  expand = 3
  formula = G4_LUCITE
  name = G4_LUCITE
  specific = 4
FEATURE [App::DocumentObjectGroupPython] Cu_element002  label="Cu_element : 62"  # scripted group (container) (typed FeaturePython)
  n = 62
  ref = Cu_element
FEATURE [App::DocumentObjectGroupPython] Zn_element002  label="Zn_element : 35"  # scripted group (container) (typed FeaturePython)
  n = 35
  ref = Zn_element
FEATURE [App::DocumentObjectGroupPython] Pb_element005  label="Pb_element : 3"  # scripted group (container) (typed FeaturePython)
  n = 3
  ref = Pb_element
FEATURE [App::DocumentObjectGroupPython] G4_BRASS  # scripted group (container) (typed FeaturePython)
  Dunit = g/cm3
  Dvalue = 8.52
  Group = -> [Cu_element002,Zn_element002,Pb_element005]
  conduct = 2
  density = 1
  expand = 3
  formula = G4_BRASS
  name = G4_BRASS
  specific = 4
FEATURE [App::DocumentObjectGroupPython] Cu_element003  label="Cu_element : 89"  # scripted group (container) (typed FeaturePython)
  n = 89
  ref = Cu_element
FEATURE [App::DocumentObjectGroupPython] Zn_element003  label="Zn_element : 9"  # scripted group (container) (typed FeaturePython)
  n = 9
  ref = Zn_element
FEATURE [App::DocumentObjectGroupPython] Pb_element006  label="Pb_element : 2"  # scripted group (container) (typed FeaturePython)
  n = 2
  ref = Pb_element
FEATURE [App::DocumentObjectGroupPython] G4_BRONZE  # scripted group (container) (typed FeaturePython)
  Dunit = g/cm3
  Dvalue = 8.82
  Group = -> [Cu_element003,Zn_element003,Pb_element006]
  conduct = 2
  density = 1
  expand = 3
  formula = G4_BRONZE
  name = G4_BRONZE
  specific = 4
FEATURE [App::DocumentObjectGroupPython] Fe_element008  label="Fe_element : 74"  # scripted group (container) (typed FeaturePython)
  n = 74
  ref = Fe_element
FEATURE [App::DocumentObjectGroupPython] Cr_element002  label="Cr_element : 18"  # scripted group (container) (typed FeaturePython)
  n = 18
  ref = Cr_element
FEATURE [App::DocumentObjectGroupPython] Ni_element002  label="Ni_element : 8"  # scripted group (container) (typed FeaturePython)
  n = 8
  ref = Ni_element
FEATURE [App::DocumentObjectGroupPython] G4_STAINLESS_STEEL  label="G4_STAINLESS-STEEL"  # scripted group (container) (typed FeaturePython)
  Dunit = g/cm3
  Dvalue = 8
  Group = -> [Fe_element008,Cr_element002,Ni_element002]
  conduct = 2
  density = 1
  expand = 3
  formula = G4_STAINLESS-STEEL
  name = G4_STAINLESS-STEEL
  specific = 4
FEATURE [App::DocumentObjectGroupPython] H_element117  label="H_element : 065"  # scripted group (container) (typed FeaturePython)
  n = 18
  ref = H_element
FEATURE [App::DocumentObjectGroupPython] C_element127  label="C_element : 072"  # scripted group (container) (typed FeaturePython)
  n = 12
  ref = C_element
FEATURE [App::DocumentObjectGroupPython] O_element109  label="O_element : 062"  # scripted group (container) (typed FeaturePython)
  n = 7
  ref = O_element
FEATURE [App::DocumentObjectGroupPython] G4_CR39  # scripted group (container) (typed FeaturePython)
  Dunit = g/cm3
  Dvalue = 1.32
  Group = -> [H_element117,C_element127,O_element109]
  conduct = 2
  density = 1
  expand = 3
  formula = G4_CR39
  name = G4_CR39
  specific = 4
FEATURE [App::DocumentObjectGroupPython] H_element118  label="H_element : 38"  # scripted group (container) (typed FeaturePython)
  n = 38
  ref = H_element
FEATURE [App::DocumentObjectGroupPython] C_element128  label="C_element : 073"  # scripted group (container) (typed FeaturePython)
  n = 18
  ref = C_element
FEATURE [App::DocumentObjectGroupPython] O_element110  label="O_element : 063"  # scripted group (container) (typed FeaturePython)
  n = 1
  ref = O_element
FEATURE [App::DocumentObjectGroupPython] G4_OCTADECANOL  # scripted group (container) (typed FeaturePython)
  Dunit = g/cm3
  Dvalue = 0.812
  Group = -> [H_element118,C_element128,O_element110]
  conduct = 2
  density = 1
  expand = 3
  formula = G4_OCTADECANOL
  name = G4_OCTADECANOL
  specific = 4
FEATURE [App::DocumentObjectGroupPython] HEP  # scripted group (container) (typed FeaturePython)
  Group = -> [G4_lH2,G4_lN2,G4_lO2,G4_lAr,G4_lBr,G4_lKr,G4_lXe,G4_PbWO4,G4_Galactic,G4_GRAPHITE_POROUS,G4_LUCITE,G4_BRASS,G4_BRONZE,G4_STAINLESS_STEEL,G4_CR39,G4_OCTADECANOL]
FEATURE [App::DocumentObjectGroupPython] C_element129  label="C_element : 074"  # scripted group (container) (typed FeaturePython)
  n = 14
  ref = C_element
FEATURE [App::DocumentObjectGroupPython] H_element119  label="H_element : 066"  # scripted group (container) (typed FeaturePython)
  n = 10
  ref = H_element
FEATURE [App::DocumentObjectGroupPython] O_element111  label="O_element : 064"  # scripted group (container) (typed FeaturePython)
  n = 2
  ref = O_element
FEATURE [App::DocumentObjectGroupPython] N_element050  label="N_element : 023"  # scripted group (container) (typed FeaturePython)
  n = 2
  ref = N_element
FEATURE [App::DocumentObjectGroupPython] G4_KEVLAR  # scripted group (container) (typed FeaturePython)
  Dunit = g/cm3
  Dvalue = 1.44
  Group = -> [C_element129,H_element119,O_element111,N_element050]
  conduct = 2
  density = 1
  expand = 3
  formula = G4_KEVLAR
  name = G4_KEVLAR
  specific = 4
FEATURE [App::DocumentObjectGroupPython] C_element130  label="C_element : 075"  # scripted group (container) (typed FeaturePython)
  n = 10
  ref = C_element
FEATURE [App::DocumentObjectGroupPython] H_element120  label="H_element : 067"  # scripted group (container) (typed FeaturePython)
  n = 8
  ref = H_element
FEATURE [App::DocumentObjectGroupPython] O_element112  label="O_element : 065"  # scripted group (container) (typed FeaturePython)
  n = 4
  ref = O_element
FEATURE [App::DocumentObjectGroupPython] G4_DACRON  # scripted group (container) (typed FeaturePython)
  Dunit = g/cm3
  Dvalue = 1.4
  Group = -> [C_element130,H_element120,O_element112]
  conduct = 2
  density = 1
  expand = 3
  formula = G4_DACRON
  name = G4_DACRON
  specific = 4
FEATURE [App::DocumentObjectGroupPython] C_element131  label="C_element : 076"  # scripted group (container) (typed FeaturePython)
  n = 4
  ref = C_element
FEATURE [App::DocumentObjectGroupPython] H_element121  label="H_element : 068"  # scripted group (container) (typed FeaturePython)
  n = 5
  ref = H_element
FEATURE [App::DocumentObjectGroupPython] Cl_element030  label="Cl_element : 016"  # scripted group (container) (typed FeaturePython)
  n = 1
  ref = Cl_element
FEATURE [App::DocumentObjectGroupPython] G4_NEOPRENE  # scripted group (container) (typed FeaturePython)
  Dunit = g/cm3
  Dvalue = 1.23
  Group = -> [C_element131,H_element121,Cl_element030]
  conduct = 2
  density = 1
  expand = 3
  formula = G4_NEOPRENE
  name = G4_NEOPRENE
  specific = 4
FEATURE [App::DocumentObjectGroupPython] Space  # scripted group (container) (typed FeaturePython)
  Group = -> [G4_KEVLAR,G4_DACRON,G4_NEOPRENE]
FEATURE [App::DocumentObjectGroupPython] H_element122  label="H_element : 069"  # scripted group (container) (typed FeaturePython)
  n = 5
  ref = H_element
FEATURE [App::DocumentObjectGroupPython] C_element132  label="C_element : 077"  # scripted group (container) (typed FeaturePython)
  n = 4
  ref = C_element
FEATURE [App::DocumentObjectGroupPython] N_element051  label="N_element : 3"  # scripted group (container) (typed FeaturePython)
  n = 3
  ref = N_element
FEATURE [App::DocumentObjectGroupPython] O_element113  label="O_element : 066"  # scripted group (container) (typed FeaturePython)
  n = 1
  ref = O_element
FEATURE [App::DocumentObjectGroupPython] G4_CYTOSINE  # scripted group (container) (typed FeaturePython)
  Dunit = g/cm3
  Dvalue = 1.55
  Group = -> [H_element122,C_element132,N_element051,O_element113]
  conduct = 2
  density = 1
  expand = 3
  formula = G4_CYTOSINE
  name = G4_CYTOSINE
  specific = 4
FEATURE [App::DocumentObjectGroupPython] H_element123  label="H_element : 070"  # scripted group (container) (typed FeaturePython)
  n = 6
  ref = H_element
FEATURE [App::DocumentObjectGroupPython] C_element133  label="C_element : 078"  # scripted group (container) (typed FeaturePython)
  n = 5
  ref = C_element
FEATURE [App::DocumentObjectGroupPython] N_element052  label="N_element : 024"  # scripted group (container) (typed FeaturePython)
  n = 2
  ref = N_element
FEATURE [App::DocumentObjectGroupPython] O_element114  label="O_element : 067"  # scripted group (container) (typed FeaturePython)
  n = 2
  ref = O_element
FEATURE [App::DocumentObjectGroupPython] G4_THYMINE  # scripted group (container) (typed FeaturePython)
  Dunit = g/cm3
  Dvalue = 1.23
  Group = -> [H_element123,C_element133,N_element052,O_element114]
  conduct = 2
  density = 1
  expand = 3
  formula = G4_THYMINE
  name = G4_THYMINE
  specific = 4
FEATURE [App::DocumentObjectGroupPython] H_element124  label="H_element : 071"  # scripted group (container) (typed FeaturePython)
  n = 4
  ref = H_element
FEATURE [App::DocumentObjectGroupPython] C_element134  label="C_element : 079"  # scripted group (container) (typed FeaturePython)
  n = 4
  ref = C_element
FEATURE [App::DocumentObjectGroupPython] N_element053  label="N_element : 025"  # scripted group (container) (typed FeaturePython)
  n = 2
  ref = N_element
FEATURE [App::DocumentObjectGroupPython] O_element115  label="O_element : 068"  # scripted group (container) (typed FeaturePython)
  n = 2
  ref = O_element
FEATURE [App::DocumentObjectGroupPython] G4_URACIL  # scripted group (container) (typed FeaturePython)
  Dunit = g/cm3
  Dvalue = 1.32
  Group = -> [H_element124,C_element134,N_element053,O_element115]
  conduct = 2
  density = 1
  expand = 3
  formula = G4_URACIL
  name = G4_URACIL
  specific = 4
FEATURE [App::DocumentObjectGroupPython] H_element125  label="H_element : 072"  # scripted group (container) (typed FeaturePython)
  n = 4
  ref = H_element
FEATURE [App::DocumentObjectGroupPython] C_element135  label="C_element : 080"  # scripted group (container) (typed FeaturePython)
  n = 5
  ref = C_element
FEATURE [App::DocumentObjectGroupPython] N_element054  label="N_element : 026"  # scripted group (container) (typed FeaturePython)
  n = 5
  ref = N_element
FEATURE [App::DocumentObjectGroupPython] G4_DNA_ADENINE  # scripted group (container) (typed FeaturePython)
  Dunit = g/cm3
  Dvalue = 1
  Group = -> [H_element125,C_element135,N_element054]
  conduct = 2
  density = 1
  expand = 3
  formula = G4_DNA_ADENINE
  name = G4_DNA_ADENINE
  specific = 4
FEATURE [App::DocumentObjectGroupPython] H_element126  label="H_element : 073"  # scripted group (container) (typed FeaturePython)
  n = 4
  ref = H_element
FEATURE [App::DocumentObjectGroupPython] C_element136  label="C_element : 081"  # scripted group (container) (typed FeaturePython)
  n = 5
  ref = C_element
FEATURE [App::DocumentObjectGroupPython] N_element055  label="N_element : 027"  # scripted group (container) (typed FeaturePython)
  n = 5
  ref = N_element
FEATURE [App::DocumentObjectGroupPython] O_element116  label="O_element : 069"  # scripted group (container) (typed FeaturePython)
  n = 1
  ref = O_element
FEATURE [App::DocumentObjectGroupPython] G4_DNA_GUANINE  # scripted group (container) (typed FeaturePython)
  Dunit = g/cm3
  Dvalue = 1
  Group = -> [H_element126,C_element136,N_element055,O_element116]
  conduct = 2
  density = 1
  expand = 3
  formula = G4_DNA_GUANINE
  name = G4_DNA_GUANINE
  specific = 4
FEATURE [App::DocumentObjectGroupPython] H_element127  label="H_element : 074"  # scripted group (container) (typed FeaturePython)
  n = 4
  ref = H_element
FEATURE [App::DocumentObjectGroupPython] C_element137  label="C_element : 082"  # scripted group (container) (typed FeaturePython)
  n = 4
  ref = C_element
FEATURE [App::DocumentObjectGroupPython] N_element056  label="N_element : 028"  # scripted group (container) (typed FeaturePython)
  n = 3
  ref = N_element
FEATURE [App::DocumentObjectGroupPython] O_element117  label="O_element : 070"  # scripted group (container) (typed FeaturePython)
  n = 1
  ref = O_element
FEATURE [App::DocumentObjectGroupPython] G4_DNA_CYTOSINE  # scripted group (container) (typed FeaturePython)
  Dunit = g/cm3
  Dvalue = 1
  Group = -> [H_element127,C_element137,N_element056,O_element117]
  conduct = 2
  density = 1
  expand = 3
  formula = G4_DNA_CYTOSINE
  name = G4_DNA_CYTOSINE
  specific = 4
FEATURE [App::DocumentObjectGroupPython] H_element128  label="H_element : 075"  # scripted group (container) (typed FeaturePython)
  n = 5
  ref = H_element
FEATURE [App::DocumentObjectGroupPython] C_element138  label="C_element : 083"  # scripted group (container) (typed FeaturePython)
  n = 5
  ref = C_element
FEATURE [App::DocumentObjectGroupPython] N_element057  label="N_element : 029"  # scripted group (container) (typed FeaturePython)
  n = 2
  ref = N_element
FEATURE [App::DocumentObjectGroupPython] O_element118  label="O_element : 071"  # scripted group (container) (typed FeaturePython)
  n = 2
  ref = O_element
FEATURE [App::DocumentObjectGroupPython] G4_DNA_THYMINE  # scripted group (container) (typed FeaturePython)
  Dunit = g/cm3
  Dvalue = 1
  Group = -> [H_element128,C_element138,N_element057,O_element118]
  conduct = 2
  density = 1
  expand = 3
  formula = G4_DNA_THYMINE
  name = G4_DNA_THYMINE
  specific = 4
FEATURE [App::DocumentObjectGroupPython] H_element129  label="H_element : 076"  # scripted group (container) (typed FeaturePython)
  n = 3
  ref = H_element
FEATURE [App::DocumentObjectGroupPython] C_element139  label="C_element : 084"  # scripted group (container) (typed FeaturePython)
  n = 4
  ref = C_element
FEATURE [App::DocumentObjectGroupPython] N_element058  label="N_element : 030"  # scripted group (container) (typed FeaturePython)
  n = 2
  ref = N_element
FEATURE [App::DocumentObjectGroupPython] O_element119  label="O_element : 072"  # scripted group (container) (typed FeaturePython)
  n = 2
  ref = O_element
FEATURE [App::DocumentObjectGroupPython] G4_DNA_URACIL  # scripted group (container) (typed FeaturePython)
  Dunit = g/cm3
  Dvalue = 1
  Group = -> [H_element129,C_element139,N_element058,O_element119]
  conduct = 2
  density = 1
  expand = 3
  formula = G4_DNA_URACIL
  name = G4_DNA_URACIL
  specific = 4
FEATURE [App::DocumentObjectGroupPython] H_element130  label="H_element : 077"  # scripted group (container) (typed FeaturePython)
  n = 10
  ref = H_element
FEATURE [App::DocumentObjectGroupPython] C_element140  label="C_element : 085"  # scripted group (container) (typed FeaturePython)
  n = 10
  ref = C_element
FEATURE [App::DocumentObjectGroupPython] N_element059  label="N_element : 031"  # scripted group (container) (typed FeaturePython)
  n = 5
  ref = N_element
FEATURE [App::DocumentObjectGroupPython] O_element120  label="O_element : 073"  # scripted group (container) (typed FeaturePython)
  n = 4
  ref = O_element
FEATURE [App::DocumentObjectGroupPython] G4_DNA_ADENOSINE  # scripted group (container) (typed FeaturePython)
  Dunit = g/cm3
  Dvalue = 1
  Group = -> [H_element130,C_element140,N_element059,O_element120]
  conduct = 2
  density = 1
  expand = 3
  formula = G4_DNA_ADENOSINE
  name = G4_DNA_ADENOSINE
  specific = 4
FEATURE [App::DocumentObjectGroupPython] H_element131  label="H_element : 078"  # scripted group (container) (typed FeaturePython)
  n = 10
  ref = H_element
FEATURE [App::DocumentObjectGroupPython] C_element141  label="C_element : 086"  # scripted group (container) (typed FeaturePython)
  n = 10
  ref = C_element
FEATURE [App::DocumentObjectGroupPython] N_element060  label="N_element : 032"  # scripted group (container) (typed FeaturePython)
  n = 5
  ref = N_element
FEATURE [App::DocumentObjectGroupPython] O_element121  label="O_element : 074"  # scripted group (container) (typed FeaturePython)
  n = 5
  ref = O_element
FEATURE [App::DocumentObjectGroupPython] G4_DNA_GUANOSINE  # scripted group (container) (typed FeaturePython)
  Dunit = g/cm3
  Dvalue = 1
  Group = -> [H_element131,C_element141,N_element060,O_element121]
  conduct = 2
  density = 1
  expand = 3
  formula = G4_DNA_GUANOSINE
  name = G4_DNA_GUANOSINE
  specific = 4
FEATURE [App::DocumentObjectGroupPython] H_element132  label="H_element : 079"  # scripted group (container) (typed FeaturePython)
  n = 10
  ref = H_element
FEATURE [App::DocumentObjectGroupPython] C_element142  label="C_element : 087"  # scripted group (container) (typed FeaturePython)
  n = 9
  ref = C_element
FEATURE [App::DocumentObjectGroupPython] N_element061  label="N_element : 033"  # scripted group (container) (typed FeaturePython)
  n = 3
  ref = N_element
FEATURE [App::DocumentObjectGroupPython] O_element122  label="O_element : 075"  # scripted group (container) (typed FeaturePython)
  n = 5
  ref = O_element
FEATURE [App::DocumentObjectGroupPython] G4_DNA_CYTIDINE  # scripted group (container) (typed FeaturePython)
  Dunit = g/cm3
  Dvalue = 1
  Group = -> [H_element132,C_element142,N_element061,O_element122]
  conduct = 2
  density = 1
  expand = 3
  formula = G4_DNA_CYTIDINE
  name = G4_DNA_CYTIDINE
  specific = 4
FEATURE [App::DocumentObjectGroupPython] H_element133  label="H_element : 080"  # scripted group (container) (typed FeaturePython)
  n = 9
  ref = H_element
FEATURE [App::DocumentObjectGroupPython] C_element143  label="C_element : 088"  # scripted group (container) (typed FeaturePython)
  n = 9
  ref = C_element
FEATURE [App::DocumentObjectGroupPython] N_element062  label="N_element : 034"  # scripted group (container) (typed FeaturePython)
  n = 2
  ref = N_element
FEATURE [App::DocumentObjectGroupPython] O_element123  label="O_element : 076"  # scripted group (container) (typed FeaturePython)
  n = 6
  ref = O_element
FEATURE [App::DocumentObjectGroupPython] G4_DNA_URIDINE  # scripted group (container) (typed FeaturePython)
  Dunit = g/cm3
  Dvalue = 1
  Group = -> [H_element133,C_element143,N_element062,O_element123]
  conduct = 2
  density = 1
  expand = 3
  formula = G4_DNA_URIDINE
  name = G4_DNA_URIDINE
  specific = 4
FEATURE [App::DocumentObjectGroupPython] H_element134  label="H_element : 081"  # scripted group (container) (typed FeaturePython)
  n = 11
  ref = H_element
FEATURE [App::DocumentObjectGroupPython] C_element144  label="C_element : 089"  # scripted group (container) (typed FeaturePython)
  n = 10
  ref = C_element
FEATURE [App::DocumentObjectGroupPython] N_element063  label="N_element : 035"  # scripted group (container) (typed FeaturePython)
  n = 2
  ref = N_element
FEATURE [App::DocumentObjectGroupPython] O_element124  label="O_element : 077"  # scripted group (container) (typed FeaturePython)
  n = 6
  ref = O_element
FEATURE [App::DocumentObjectGroupPython] G4_DNA_METHYLURIDINE  # scripted group (container) (typed FeaturePython)
  Dunit = g/cm3
  Dvalue = 1
  Group = -> [H_element134,C_element144,N_element063,O_element124]
  conduct = 2
  density = 1
  expand = 3
  formula = G4_DNA_METHYLURIDINE
  name = G4_DNA_METHYLURIDINE
  specific = 4
FEATURE [App::DocumentObjectGroupPython] P_element014  label="P_element : 003"  # scripted group (container) (typed FeaturePython)
  n = 1
  ref = P_element
FEATURE [App::DocumentObjectGroupPython] O_element125  label="O_element : 078"  # scripted group (container) (typed FeaturePython)
  n = 3
  ref = O_element
FEATURE [App::DocumentObjectGroupPython] G4_DNA_MONOPHOSPHATE  # scripted group (container) (typed FeaturePython)
  Dunit = g/cm3
  Dvalue = 1
  Group = -> [P_element014,O_element125]
  conduct = 2
  density = 1
  expand = 3
  formula = G4_DNA_MONOPHOSPHATE
  name = G4_DNA_MONOPHOSPHATE
  specific = 4
FEATURE [App::DocumentObjectGroupPython] H_element135  label="H_element : 082"  # scripted group (container) (typed FeaturePython)
  n = 10
  ref = H_element
FEATURE [App::DocumentObjectGroupPython] C_element145  label="C_element : 090"  # scripted group (container) (typed FeaturePython)
  n = 10
  ref = C_element
FEATURE [App::DocumentObjectGroupPython] N_element064  label="N_element : 036"  # scripted group (container) (typed FeaturePython)
  n = 5
  ref = N_element
FEATURE [App::DocumentObjectGroupPython] O_element126  label="O_element : 079"  # scripted group (container) (typed FeaturePython)
  n = 7
  ref = O_element
FEATURE [App::DocumentObjectGroupPython] P_element015  label="P_element : 004"  # scripted group (container) (typed FeaturePython)
  n = 1
  ref = P_element
FEATURE [App::DocumentObjectGroupPython] G4_DNA_A  # scripted group (container) (typed FeaturePython)
  Dunit = g/cm3
  Dvalue = 1
  Group = -> [H_element135,C_element145,N_element064,O_element126,P_element015]
  conduct = 2
  density = 1
  expand = 3
  formula = G4_DNA_A
  name = G4_DNA_A
  specific = 4
FEATURE [App::DocumentObjectGroupPython] H_element136  label="H_element : 083"  # scripted group (container) (typed FeaturePython)
  n = 10
  ref = H_element
FEATURE [App::DocumentObjectGroupPython] C_element146  label="C_element : 091"  # scripted group (container) (typed FeaturePython)
  n = 10
  ref = C_element
FEATURE [App::DocumentObjectGroupPython] N_element065  label="N_element : 037"  # scripted group (container) (typed FeaturePython)
  n = 5
  ref = N_element
FEATURE [App::DocumentObjectGroupPython] O_element127  label="O_element : 8"  # scripted group (container) (typed FeaturePython)
  n = 8
  ref = O_element
FEATURE [App::DocumentObjectGroupPython] P_element016  label="P_element : 005"  # scripted group (container) (typed FeaturePython)
  n = 1
  ref = P_element
FEATURE [App::DocumentObjectGroupPython] G4_DNA_G  # scripted group (container) (typed FeaturePython)
  Dunit = g/cm3
  Dvalue = 1
  Group = -> [H_element136,C_element146,N_element065,O_element127,P_element016]
  conduct = 2
  density = 1
  expand = 3
  formula = G4_DNA_G
  name = G4_DNA_G
  specific = 4
FEATURE [App::DocumentObjectGroupPython] H_element137  label="H_element : 084"  # scripted group (container) (typed FeaturePython)
  n = 10
  ref = H_element
FEATURE [App::DocumentObjectGroupPython] C_element147  label="C_element : 092"  # scripted group (container) (typed FeaturePython)
  n = 9
  ref = C_element
FEATURE [App::DocumentObjectGroupPython] N_element066  label="N_element : 038"  # scripted group (container) (typed FeaturePython)
  n = 3
  ref = N_element
FEATURE [App::DocumentObjectGroupPython] O_element128  label="O_element : 080"  # scripted group (container) (typed FeaturePython)
  n = 8
  ref = O_element
FEATURE [App::DocumentObjectGroupPython] P_element017  label="P_element : 006"  # scripted group (container) (typed FeaturePython)
  n = 1
  ref = P_element
FEATURE [App::DocumentObjectGroupPython] G4_DNA_C  # scripted group (container) (typed FeaturePython)
  Dunit = g/cm3
  Dvalue = 1
  Group = -> [H_element137,C_element147,N_element066,O_element128,P_element017]
  conduct = 2
  density = 1
  expand = 3
  formula = G4_DNA_C
  name = G4_DNA_C
  specific = 4
FEATURE [App::DocumentObjectGroupPython] H_element138  label="H_element : 085"  # scripted group (container) (typed FeaturePython)
  n = 9
  ref = H_element
FEATURE [App::DocumentObjectGroupPython] C_element148  label="C_element : 093"  # scripted group (container) (typed FeaturePython)
  n = 9
  ref = C_element
FEATURE [App::DocumentObjectGroupPython] N_element067  label="N_element : 039"  # scripted group (container) (typed FeaturePython)
  n = 2
  ref = N_element
FEATURE [App::DocumentObjectGroupPython] O_element129  label="O_element : 9"  # scripted group (container) (typed FeaturePython)
  n = 9
  ref = O_element
FEATURE [App::DocumentObjectGroupPython] P_element018  label="P_element : 007"  # scripted group (container) (typed FeaturePython)
  n = 1
  ref = P_element
FEATURE [App::DocumentObjectGroupPython] G4_DNA_U  # scripted group (container) (typed FeaturePython)
  Dunit = g/cm3
  Dvalue = 1
  Group = -> [H_element138,C_element148,N_element067,O_element129,P_element018]
  conduct = 2
  density = 1
  expand = 3
  formula = G4_DNA_U
  name = G4_DNA_U
  specific = 4
FEATURE [App::DocumentObjectGroupPython] H_element139  label="H_element : 086"  # scripted group (container) (typed FeaturePython)
  n = 11
  ref = H_element
FEATURE [App::DocumentObjectGroupPython] C_element149  label="C_element : 094"  # scripted group (container) (typed FeaturePython)
  n = 10
  ref = C_element
FEATURE [App::DocumentObjectGroupPython] N_element068  label="N_element : 040"  # scripted group (container) (typed FeaturePython)
  n = 2
  ref = N_element
FEATURE [App::DocumentObjectGroupPython] O_element130  label="O_element : 081"  # scripted group (container) (typed FeaturePython)
  n = 9
  ref = O_element
FEATURE [App::DocumentObjectGroupPython] P_element019  label="P_element : 008"  # scripted group (container) (typed FeaturePython)
  n = 1
  ref = P_element
FEATURE [App::DocumentObjectGroupPython] G4_DNA_MU  # scripted group (container) (typed FeaturePython)
  Dunit = g/cm3
  Dvalue = 1
  Group = -> [H_element139,C_element149,N_element068,O_element130,P_element019]
  conduct = 2
  density = 1
  expand = 3
  formula = G4_DNA_MU
  name = G4_DNA_MU
  specific = 4
FEATURE [App::DocumentObjectGroupPython] BioChemical  # scripted group (container) (typed FeaturePython)
  Group = -> [G4_CYTOSINE,G4_THYMINE,G4_URACIL,G4_DNA_ADENINE,G4_DNA_GUANINE,G4_DNA_CYTOSINE,G4_DNA_THYMINE,G4_DNA_URACIL,G4_DNA_ADENOSINE,G4_DNA_GUANOSINE,G4_DNA_CYTIDINE,G4_DNA_URIDINE,G4_DNA_METHYLURIDINE,G4_DNA_MONOPHOSPHATE,G4_DNA_A,G4_DNA_G,G4_DNA_C,G4_DNA_U,G4_DNA_MU]
FEATURE [App::DocumentObjectGroupPython] G4Materials  # scripted group (container) (typed FeaturePython)
  Group = -> [NIST,Element,HEP,Space,BioChemical]
  version = 1
FEATURE [App::DocumentObjectGroupPython] Geant4  # scripted group (container) (typed FeaturePython)
  Group = -> [G4Isotopes,G4Elements,G4Materials]
FEATURE [App::DocumentObjectGroupPython] Materials  # scripted group (container) (typed FeaturePython)
  Group = -> [Geant4]
FEATURE [Part::FeaturePython] GDMLBox_WorldBox  # WARN: FeaturePython — macro-defined, semantics opaque (R4)
  lunit = 2
  material = 5
  x = 130
  y = 130
  z = 130
FEATURE [Part::Cylinder] Cylinder
  Angle = 360
  AttacherType = Attacher::AttachEngine3D
  FirstAngle = 0
  Height = 10
  Radius = 2
  SecondAngle = 0
FEATURE [Part::Box] Box  label="Cube"
  AttacherType = Attacher::AttachEngine3D
  Height = 10
  Length = 10
  Width = 10
FEATURE [Part::Sphere] Sphere
  Angle1 = -90
  Angle2 = 90
  Angle3 = 360
  AttacherType = Attacher::AttachEngine3D
  Radius = 5
FEATURE [Part::Cone] Cone
  Angle = 360
  AttacherType = Attacher::AttachEngine3D
  Height = 10
  Radius1 = 2
  Radius2 = 4
FEATURE [Part::Box] Box001  label="Cube001"
  AttacherType = Attacher::AttachEngine3D
  Height = 10
  Length = 10
  Width = 10
FEATURE [Part::Common] Common001
  Base = -> Cone
  Placement = pos=(8,0,0) rot=(0,0,1;0rad)
  Tool = -> Box001
FEATURE [App::Part] Part  label="Common002"
  Group = -> [Cone,Box001,Common001]
  Origin = -> Origin001
FEATURE [Part::MultiCommon] Common
  Shapes = -> [Sphere,Cylinder,Box]
FEATURE [App::Part] Part001  label="MultiCommon"
  Group = -> [Sphere,Cylinder,Box,Common]
  Origin = -> Origin002
FEATURE [App::Part] worldVOL
  Group = -> [GDMLBox_WorldBox,Part001,Part]
  Origin = -> Origin
